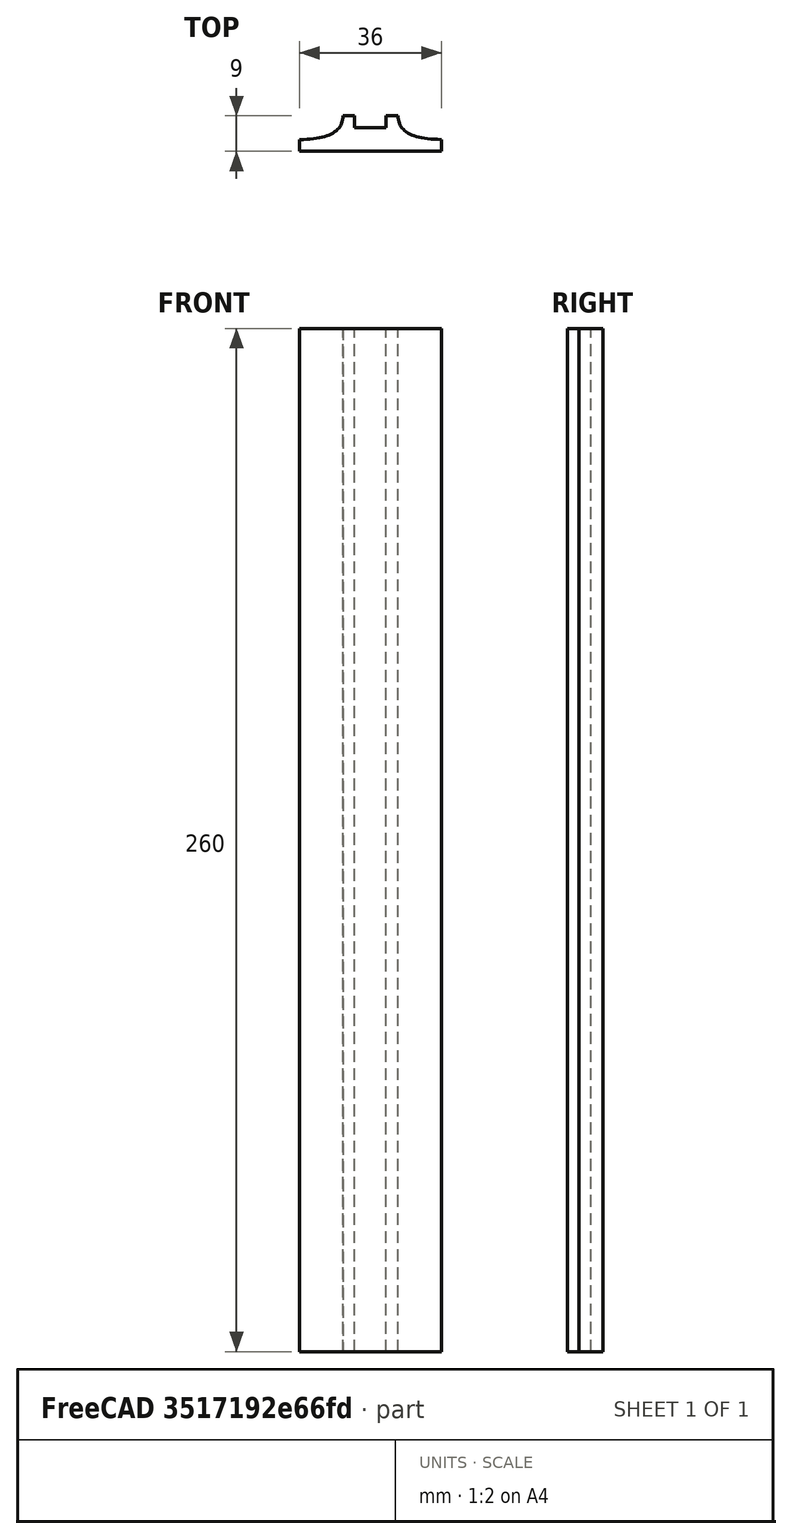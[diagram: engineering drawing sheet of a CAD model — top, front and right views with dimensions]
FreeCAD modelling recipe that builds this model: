
FCSTD DOCUMENT  (FreeCAD 0.19R0.19.2)
Label: laptopStand295.FCStd
License: All rights reserved
LicenseURL: http://en.wikipedia.org/wiki/All_rights_reserved
objects: Sketcher::SketchObject×10, Part::Extrusion×1
note: 11 computed .brp shape members not serialized (recipe doc carries the construction recipe); baked Part::Feature solids carry a one-line shape summary decoded from their .brp

FEATURE [Sketcher::SketchObject] Sketch001  label="legTop"
  FullyConstrained = true
  MapMode = 4
  Placement = pos=(0,0,0) rot=(0.57735,0.57735,0.57735;2.0944rad)
  sketch-geometry (41):
    g0: BSplineCurve PolesCount=3 KnotsCount=2 Degree=2 IsPeriodic=0
    g1: ArcOfCircle CenterX=73.1223 CenterY=-32.291 CenterZ=0 NormalX=0 NormalY=0 NormalZ=1 AngleXU=0 Radius=13 StartAngle=5.92268 EndAngle=9.06428
    g2: ArcOfCircle CenterX=66.7816 CenterY=-49.1439 CenterZ=0 NormalX=0 NormalY=0 NormalZ=1 AngleXU=0 Radius=13 StartAngle=2.78068 EndAngle=5.92131
    g3-g6: Circle x4 (B-spline internal-alignment scaffolding for g7; pole/knot coordinates omitted)
    g7: BSplineCurve PolesCount=4 KnotsCount=2 Degree=3 IsPeriodic=0
    g8: GeomPoint X=28.8094 Y=-19.0875 Z=0
    g9: GeomPoint X=47.0443 Y=-50.4712 Z=0
    g10: Circle CenterX=53.5586 CenterY=-23.2695 CenterZ=0 NormalX=0 NormalY=0 NormalZ=1 AngleXU=0 Radius=3.24518
    g11: LineSegment StartX=117.223 StartY=-19.0875 StartZ=0 EndX=117.223 EndY=-16.0875 EndZ=0
    g12: LineSegment StartX=117.223 StartY=-16.0875 StartZ=0 EndX=17.2232 EndY=-16.0875 EndZ=0
    g13: LineSegment StartX=17.2232 StartY=-16.0875 StartZ=0 EndX=17.2232 EndY=-19.0875 EndZ=0
    g14: LineSegment StartX=28.8094 StartY=-19.0875 StartZ=0 EndX=17.2232 EndY=-19.0875 EndZ=0
    g15: LineSegment StartX=85.2866 StartY=-36.8766 StartZ=0 EndX=78.9396 EndY=-53.7463 EndZ=0
    g16: LineSegment StartX=60.9579 StartY=-27.7053 StartZ=0 EndX=54.6191 EndY=-44.5532 EndZ=0
    g17: ArcOfCircle CenterX=17.2475 CenterY=-181.166 CenterZ=0 NormalX=0 NormalY=0 NormalZ=1 AngleXU=0 Radius=13 StartAngle=5.92268 EndAngle=7.49361
    g18: ArcOfCircle CenterX=29.5716 CenterY=-148.408 CenterZ=0 NormalX=0 NormalY=0 NormalZ=1 AngleXU=0 Radius=13 StartAngle=4.35228 EndAngle=5.92131
    g19: ArcOfCircle CenterX=35.8967 CenterY=-131.555 CenterZ=0 NormalX=0 NormalY=0 NormalZ=1 AngleXU=0 Radius=13 StartAngle=5.92268 EndAngle=7.49902
    g20: ArcOfCircle CenterX=48.1805 CenterY=-98.7782 CenterZ=0 NormalX=0 NormalY=0 NormalZ=1 AngleXU=0 Radius=13 StartAngle=4.34921 EndAngle=5.92131
    g21: ArcOfCircle CenterX=54.5183 CenterY=-81.9247 CenterZ=0 NormalX=0 NormalY=0 NormalZ=1 AngleXU=0 Radius=13 StartAngle=5.92268 EndAngle=8.70432
    g22: LineSegment StartX=66.6827 StartY=-86.5104 StartZ=0 EndX=60.3386 EndY=-103.381 EndZ=0
    g23: LineSegment StartX=48.061 StartY=-136.14 StartZ=0 EndX=41.7296 EndY=-153.01 EndZ=0
    g24: ArcOfCircle CenterX=20.184 CenterY=-217.506 CenterZ=0 NormalX=0 NormalY=0 NormalZ=1 AngleXU=0 Radius=3.81084 StartAngle=1.88136 EndAngle=6.80465
    g25: LineSegment StartX=38.4753 StartY=-115.966 StartZ=0 EndX=41.2852 EndY=-117.017 EndZ=0
    g26: ArcOfCircle CenterX=36.3663 CenterY=-113.042 CenterZ=0 NormalX=0 NormalY=0 NormalZ=1 AngleXU=0 Radius=3.60555 StartAngle=0.230024 EndAngle=5.3372
    g27: LineSegment StartX=39.8769 StartY=-112.22 StartZ=0 EndX=42.6867 EndY=-113.271 EndZ=0
    g28: LineSegment StartX=42.6867 StartY=-113.271 StartZ=0 EndX=43.5628 EndY=-110.929 EndZ=0
    g29: LineSegment StartX=19.9036 StartY=-165.61 StartZ=0 EndX=22.7134 EndY=-166.661 EndZ=0
    g30: ArcOfCircle CenterX=17.7945 CenterY=-162.686 CenterZ=0 NormalX=0 NormalY=0 NormalZ=1 AngleXU=0 Radius=3.60555 StartAngle=0.230024 EndAngle=5.3372
    g31: LineSegment StartX=21.3051 StartY=-161.864 StartZ=0 EndX=24.1149 EndY=-162.915 EndZ=0
    g32: LineSegment StartX=24.1149 StartY=-162.915 StartZ=0 EndX=24.991 EndY=-160.573 EndZ=0
    g33: LineSegment StartX=41.085 StartY=-66.3176 StartZ=0 EndX=46.0385 EndY=-62.5254 EndZ=0
    g34: LineSegment StartX=48.9563 StartY=-66.3367 StartZ=0 EndX=44.7488 EndY=-73.3482 EndZ=0
    g35: ArcOfCircle CenterX=49.8795 CenterY=-62.6074 CenterZ=0 NormalX=0 NormalY=0 NormalZ=1 AngleXU=0 Radius=3.84187 StartAngle=4.46973 EndAngle=9.40343
    g36: LineSegment StartX=41.085 StartY=-66.3176 StartZ=0 EndX=47.0443 EndY=-50.4712 EndZ=0
    g37: LineSegment StartX=29.4118 StartY=-185.752 StartZ=0 EndX=19.0195 EndY=-213.878 EndZ=0
    g38: LineSegment StartX=41.2852 StartY=-117.017 StartZ=0 EndX=40.4148 EndY=-119.365 EndZ=0
    g39: LineSegment StartX=21.8316 StartY=-169.001 StartZ=0 EndX=22.7134 EndY=-166.661 EndZ=0
    g40: LineSegment StartX=23.4884 StartY=-215.608 StartZ=0 EndX=94.6579 EndY=-26.1359 EndZ=0
  constraints (70):
    c: Block(g0)
    c: Block(g1)
    c: Block(g2)
    c: Weight(g3) = 1
    c: Equal(g3,g4)
    c: Equal(g3,g5)
    c: Equal(g3,g6)
    c: InternalAlignment(g3-g6 -> g7) x4
    c: InternalAlignment(g8,g7)
    c: InternalAlignment(g9,g7)
    c: Block(g10)
    c: Block(g7)
    c: Coincident(g11,g0)
    c: Vertical(g11)
    c: Coincident(g12,g11)
    c: Horizontal(g12)
    c: Coincident(g13,g12)
    c: Vertical(g13)
    c: Block(g12)
    c: Coincident(g14,g7)
    c: Coincident(g14,g13)
    c: Horizontal(g14)
    c: Coincident(g15,g1)
    c: Coincident(g15,g2)
    c: Coincident(g16,g1)
    c: Coincident(g16,g2)
    c: Distance(g12) = 100
    c: Block(g17)
    c: Block(g18)
    c: Block(g19)
    c: Block(g20)
    c: Block(g21)
    c: Coincident(g22,g21)
    c: Coincident(g22,g20)
    c: Coincident(g23,g19)
    c: Coincident(g23,g18)
    c: Block(g24)
    c: Block(g26)
    c: Coincident(g27,g26)
    c: Coincident(g25,g26)
    c: Parallel(g27,g25)
    c: Coincident(g28,g27)
    c: Block(g28)
    c: Block(g25)
    c: Block(g27)
    c: Block(g30)
    c: Coincident(g31,g30)
    c: Coincident(g29,g30)
    c: Parallel(g31,g29)
    c: Coincident(g32,g31)
    c: Block(g32)
    c: Block(g29)
    c: Block(g31)
    c: Block(g33)
    c: Coincident(g35,g33)
    c: Coincident(g35,g34)
    c: Block(g35)
    c: Coincident(g36,g33)
    c: Coincident(g36,g7)
    c: Coincident(g37,g17)
    c: Coincident(g37,g24)
    c: PointOnObject(g20,g28)
    c: PointOnObject(g18,g32)
    c: Coincident(g38,g25)
    c: Coincident(g38,g19)
    c: Coincident(g39,g29)
    c: Coincident(g17,g39)
    c: Coincident(g40,g24)
    c: Coincident(g40,g0)
    c: Coincident(g21,g34)
FEATURE [Sketcher::SketchObject] Sketch002
  FullyConstrained = true
  sketch-geometry (20):
    g0: LineSegment StartX=-2.77179 StartY=-200.304 StartZ=0 EndX=5.22821 EndY=-200.304 EndZ=0
    g1: LineSegment StartX=5.22821 StartY=-200.304 StartZ=0 EndX=5.22821 EndY=-197.304 EndZ=0
    g2: LineSegment StartX=-2.77179 StartY=-200.304 StartZ=0 EndX=-2.77179 EndY=-197.304 EndZ=0
    g3: LineSegment StartX=5.22821 StartY=-197.304 StartZ=0 EndX=8.22821 EndY=-197.304 EndZ=0
    g4: LineSegment StartX=-2.77179 StartY=-197.304 StartZ=0 EndX=-5.77179 EndY=-197.304 EndZ=0
    g5: LineSegment StartX=19.2282 StartY=-203.304 StartZ=0 EndX=19.2282 EndY=-206.304 EndZ=0
    g6: LineSegment StartX=-16.7718 StartY=-203.304 StartZ=0 EndX=-16.7718 EndY=-206.304 EndZ=0
    g7: LineSegment StartX=-16.7718 StartY=-206.304 StartZ=0 EndX=19.2282 EndY=-206.304 EndZ=0
    g8: Circle CenterX=-16.7718 CenterY=-203.304 CenterZ=0 NormalX=0 NormalY=0 NormalZ=1 AngleXU=0 Radius=1
    g9: Circle CenterX=-5.77179 CenterY=-203.304 CenterZ=0 NormalX=0 NormalY=0 NormalZ=1 AngleXU=0 Radius=1
    g10: Circle CenterX=-5.77179 CenterY=-197.304 CenterZ=0 NormalX=0 NormalY=0 NormalZ=1 AngleXU=0 Radius=1
    g11: BSplineCurve PolesCount=3 KnotsCount=2 Degree=2 IsPeriodic=0
    g12: GeomPoint X=-16.7718 Y=-203.304 Z=0
    g13: GeomPoint X=-5.77179 Y=-197.304 Z=0
    g14: Circle CenterX=19.2282 CenterY=-203.304 CenterZ=0 NormalX=0 NormalY=0 NormalZ=1 AngleXU=0 Radius=1
    g15: Circle CenterX=8.22821 CenterY=-203.304 CenterZ=0 NormalX=0 NormalY=0 NormalZ=1 AngleXU=0 Radius=1
    g16: Circle CenterX=8.22821 CenterY=-197.304 CenterZ=0 NormalX=0 NormalY=0 NormalZ=1 AngleXU=0 Radius=1
    g17: BSplineCurve PolesCount=3 KnotsCount=2 Degree=2 IsPeriodic=0
    g18: GeomPoint X=19.2282 Y=-203.304 Z=0
    g19: GeomPoint X=8.22821 Y=-197.304 Z=0
  constraints (41):
    c: Horizontal(g0)
    c: Distance(g0) = 8
    c: Coincident(g1,g0)
    c: Vertical(g1)
    c: Distance(g1) = 3
    c: Coincident(g2,g0)
    c: Vertical(g2)
    c: Distance(g2) = 3
    c: Coincident(g3,g1)
    c: Horizontal(g3)
    c: Distance(g3) = 3
    c: Coincident(g4,g2)
    c: Horizontal(g4)
    c: Distance(g4) = 3
    c: Vertical(g5)
    c: Vertical(g6)
    c: Coincident(g7,g6)
    c: Coincident(g7,g5)
    c: Weight(g8) = 1
    c: Equal(g8,g9)
    c: Equal(g8,g10)
    c: Coincident(g11,g4)
    c: InternalAlignment(g8,g11)
    c: InternalAlignment(g9,g11)
    c: InternalAlignment(g10,g11)
    c: InternalAlignment(g12,g11)
    c: InternalAlignment(g13,g11)
    c: Coincident(g17,g5)
    c: Weight(g14) = 1
    c: Equal(g14,g15)
    c: Equal(g14,g16)
    c: Coincident(g17,g3)
    c: InternalAlignment(g14,g17)
    c: InternalAlignment(g15,g17)
    c: InternalAlignment(g16,g17)
    c: InternalAlignment(g18,g17)
    c: InternalAlignment(g19,g17)
    c: Block(g7)
    c: Block(g17)
    c: Block(g11)
    c: Block(g6)
FEATURE [Part::Extrusion] Extrude003
  Base = -> Sketch002
  Dir = (0,0,1)
  DirMode = 2
  FaceMakerClass = Part::FaceMakerBullseye
  LengthFwd = 260
  LengthRev = 0
  Solid = true
  Symmetric = false
FEATURE [Sketcher::SketchObject] Sketch003  label="original"
  FullyConstrained = false
  sketch-geometry (469):
    g0: LineSegment StartX=-42.9272 StartY=136.221 StartZ=0 EndX=-42.9272 EndY=-103.779 EndZ=0
    g1: LineSegment StartX=407.073 StartY=136.221 StartZ=0 EndX=407.073 EndY=-103.779 EndZ=0
    g2: ArcOfCircle CenterX=-26.9272 CenterY=-83.7794 CenterZ=0 NormalX=0 NormalY=0 NormalZ=1 AngleXU=0 Radius=8 StartAngle=3.14159 EndAngle=6.28319
    g3: ArcOfCircle CenterX=391.073 CenterY=-83.7794 CenterZ=0 NormalX=0 NormalY=0 NormalZ=1 AngleXU=0 Radius=8 StartAngle=3.14159 EndAngle=6.28319
    g4: Circle CenterX=175.022 CenterY=27.0628 CenterZ=0 NormalX=0 NormalY=0 NormalZ=1 AngleXU=0 Radius=1
    g5: Circle CenterX=179.022 CenterY=24.8665 CenterZ=0 NormalX=0 NormalY=0 NormalZ=1 AngleXU=0 Radius=1
    g6: Circle CenterX=179.022 CenterY=27.0628 CenterZ=0 NormalX=0 NormalY=0 NormalZ=1 AngleXU=0 Radius=1
    g7: BSplineCurve PolesCount=3 KnotsCount=2 Degree=2 IsPeriodic=0
    g8: GeomPoint X=175.022 Y=27.0628 Z=0
    g9: GeomPoint X=179.022 Y=27.0628 Z=0
    g10: Circle CenterX=189.124 CenterY=27.0628 CenterZ=0 NormalX=0 NormalY=0 NormalZ=1 AngleXU=0 Radius=1
    g11: Circle CenterX=185.124 CenterY=24.8665 CenterZ=0 NormalX=0 NormalY=0 NormalZ=1 AngleXU=0 Radius=1
    g12: Circle CenterX=185.124 CenterY=27.0628 CenterZ=0 NormalX=0 NormalY=0 NormalZ=1 AngleXU=0 Radius=1
    g13: BSplineCurve PolesCount=3 KnotsCount=2 Degree=2 IsPeriodic=0
    g14: GeomPoint X=189.124 Y=27.0628 Z=0
    g15: GeomPoint X=185.124 Y=27.0628 Z=0
    g16: Circle CenterX=175.022 CenterY=5.37834 CenterZ=0 NormalX=0 NormalY=0 NormalZ=1 AngleXU=0 Radius=1
    g17: Circle CenterX=179.022 CenterY=7.57463 CenterZ=0 NormalX=0 NormalY=0 NormalZ=1 AngleXU=0 Radius=1
    g18: Circle CenterX=179.022 CenterY=5.34704 CenterZ=0 NormalX=0 NormalY=0 NormalZ=1 AngleXU=0 Radius=1
    g19: BSplineCurve PolesCount=3 KnotsCount=2 Degree=2 IsPeriodic=0
    g20: GeomPoint X=175.022 Y=5.37834 Z=0
    g21: GeomPoint X=179.022 Y=5.34704 Z=0
    g22: Circle CenterX=189.124 CenterY=5.37834 CenterZ=0 NormalX=0 NormalY=0 NormalZ=1 AngleXU=0 Radius=1
    g23: Circle CenterX=185.124 CenterY=7.57463 CenterZ=0 NormalX=0 NormalY=0 NormalZ=1 AngleXU=0 Radius=1
    g24: Circle CenterX=185.124 CenterY=5.34704 CenterZ=0 NormalX=0 NormalY=0 NormalZ=1 AngleXU=0 Radius=1
    g25: BSplineCurve PolesCount=3 KnotsCount=2 Degree=2 IsPeriodic=0
    g26: GeomPoint X=189.124 Y=5.37834 Z=0
    g27: GeomPoint X=185.124 Y=5.34704 Z=0
    g28: Circle CenterX=165.871 CenterY=18.1458 CenterZ=0 NormalX=0 NormalY=0 NormalZ=1 AngleXU=0 Radius=1
    g29: Circle CenterX=169.377 CenterY=16.2206 CenterZ=0 NormalX=0 NormalY=0 NormalZ=1 AngleXU=0 Radius=1
    g30: Circle CenterX=165.871 CenterY=14.2956 CenterZ=0 NormalX=0 NormalY=0 NormalZ=1 AngleXU=0 Radius=1
    g31: BSplineCurve PolesCount=3 KnotsCount=2 Degree=2 IsPeriodic=0
    g32: GeomPoint X=165.871 Y=18.1458 Z=0
    g33: GeomPoint X=165.871 Y=14.2956 Z=0
    g34: Circle CenterX=198.275 CenterY=18.1318 CenterZ=0 NormalX=0 NormalY=0 NormalZ=1 AngleXU=0 Radius=1
    g35: Circle CenterX=194.768 CenterY=16.2206 CenterZ=0 NormalX=0 NormalY=0 NormalZ=1 AngleXU=0 Radius=1
    g36: Circle CenterX=198.264 CenterY=14.2963 CenterZ=0 NormalX=0 NormalY=0 NormalZ=1 AngleXU=0 Radius=1
    g37: BSplineCurve PolesCount=3 KnotsCount=2 Degree=2 IsPeriodic=0
    g38: GeomPoint X=198.275 Y=18.1318 Z=0
    g39: GeomPoint X=198.264 Y=14.2963 Z=0
    g40: LineSegment StartX=407.073 StartY=-103.779 StartZ=0 EndX=-42.9272 EndY=-103.779 EndZ=0
    g41: Circle CenterX=125.607 CenterY=54.1951 CenterZ=0 NormalX=0 NormalY=0 NormalZ=1 AngleXU=0 Radius=1
    g42: Circle CenterX=139.632 CenterY=46.4944 CenterZ=0 NormalX=0 NormalY=0 NormalZ=1 AngleXU=0 Radius=1
    g43: Circle CenterX=127.326 CenterY=56.7187 CenterZ=0 NormalX=0 NormalY=0 NormalZ=1 AngleXU=0 Radius=1
    g44: BSplineCurve PolesCount=3 KnotsCount=2 Degree=2 IsPeriodic=0
    g45: GeomPoint X=125.607 Y=54.1951 Z=0
    g46: GeomPoint X=127.326 Y=56.7187 Z=0
    g47: Circle CenterX=236.824 CenterY=56.7187 CenterZ=0 NormalX=0 NormalY=0 NormalZ=1 AngleXU=0 Radius=1
    g48: Circle CenterX=224.513 CenterY=46.4944 CenterZ=0 NormalX=0 NormalY=0 NormalZ=1 AngleXU=0 Radius=1
    g49: Circle CenterX=238.538 CenterY=54.1951 CenterZ=0 NormalX=0 NormalY=0 NormalZ=1 AngleXU=0 Radius=1
    g50: BSplineCurve PolesCount=3 KnotsCount=2 Degree=2 IsPeriodic=0
    g51: GeomPoint X=236.824 Y=56.7187 Z=0
    g52: GeomPoint X=238.538 Y=54.1951 Z=0
    g53: Circle CenterX=238.538 CenterY=-21.7516 CenterZ=0 NormalX=0 NormalY=0 NormalZ=1 AngleXU=0 Radius=1
    g54: Circle CenterX=224.513 CenterY=-14.0532 CenterZ=0 NormalX=0 NormalY=0 NormalZ=1 AngleXU=0 Radius=1
    g55: Circle CenterX=236.584 CenterY=-24.2775 CenterZ=0 NormalX=0 NormalY=0 NormalZ=1 AngleXU=0 Radius=1
    g56: BSplineCurve PolesCount=3 KnotsCount=2 Degree=2 IsPeriodic=0
    g57: GeomPoint X=238.538 Y=-21.7516 Z=0
    g58: GeomPoint X=236.584 Y=-24.2775 Z=0
    g59: Circle CenterX=125.607 CenterY=-21.7539 CenterZ=0 NormalX=0 NormalY=0 NormalZ=1 AngleXU=0 Radius=1
    g60: Circle CenterX=139.632 CenterY=-14.0532 CenterZ=0 NormalX=0 NormalY=0 NormalZ=1 AngleXU=0 Radius=1
    g61: Circle CenterX=127.325 CenterY=-24.2775 CenterZ=0 NormalX=0 NormalY=0 NormalZ=1 AngleXU=0 Radius=1
    g62: BSplineCurve PolesCount=3 KnotsCount=2 Degree=2 IsPeriodic=0
    g63: GeomPoint X=125.607 Y=-21.7539 Z=0
    g64: GeomPoint X=127.325 Y=-24.2775 Z=0
    g65: Circle CenterX=302.996 CenterY=111.695 CenterZ=0 NormalX=0 NormalY=0 NormalZ=1 AngleXU=0 Radius=1
    g66: Circle CenterX=306.073 CenterY=114.251 CenterZ=0 NormalX=0 NormalY=0 NormalZ=1 AngleXU=0 Radius=1
    g67: Circle CenterX=306.073 CenterY=110.251 CenterZ=0 NormalX=0 NormalY=0 NormalZ=1 AngleXU=0 Radius=1
    g68: BSplineCurve PolesCount=3 KnotsCount=2 Degree=2 IsPeriodic=0
    g69: GeomPoint X=302.996 Y=111.695 Z=0
    g70: GeomPoint X=306.073 Y=110.251 Z=0
    g71: Circle CenterX=306.073 CenterY=95.2763 CenterZ=0 NormalX=0 NormalY=0 NormalZ=1 AngleXU=0 Radius=1
    g72: Circle CenterX=306.073 CenterY=91.2763 CenterZ=0 NormalX=0 NormalY=0 NormalZ=1 AngleXU=0 Radius=1
    g73: Circle CenterX=302.567 CenterY=89.3511 CenterZ=0 NormalX=0 NormalY=0 NormalZ=1 AngleXU=0 Radius=1
    g74: BSplineCurve PolesCount=3 KnotsCount=2 Degree=2 IsPeriodic=0
    g75: GeomPoint X=306.073 Y=95.2763 Z=0
    g76: GeomPoint X=302.567 Y=89.3511 Z=0
    g77: LineSegment StartX=306.073 StartY=110.251 StartZ=0 EndX=306.073 EndY=95.2763 EndZ=0
    g78: LineSegment StartX=302.996 StartY=111.695 StartZ=0 EndX=236.824 EndY=56.7187 EndZ=0
    g79: LineSegment StartX=238.538 StartY=54.1951 StartZ=0 EndX=302.567 EndY=89.3511 EndZ=0
    g80: Circle CenterX=61.1496 CenterY=111.695 CenterZ=0 NormalX=0 NormalY=0 NormalZ=1 AngleXU=0 Radius=1
    g81: Circle CenterX=58.0728 CenterY=114.251 CenterZ=0 NormalX=0 NormalY=0 NormalZ=1 AngleXU=0 Radius=1
    g82: Circle CenterX=58.0728 CenterY=110.251 CenterZ=0 NormalX=0 NormalY=0 NormalZ=1 AngleXU=0 Radius=1
    g83: BSplineCurve PolesCount=3 KnotsCount=2 Degree=2 IsPeriodic=0
    g84: GeomPoint X=61.1496 Y=111.695 Z=0
    g85: GeomPoint X=58.0728 Y=110.251 Z=0
    g86: Circle CenterX=61.5791 CenterY=89.3511 CenterZ=0 NormalX=0 NormalY=0 NormalZ=1 AngleXU=0 Radius=1
    g87: Circle CenterX=58.0728 CenterY=91.2763 CenterZ=0 NormalX=0 NormalY=0 NormalZ=1 AngleXU=0 Radius=1
    g88: Circle CenterX=58.0728 CenterY=95.2763 CenterZ=0 NormalX=0 NormalY=0 NormalZ=1 AngleXU=0 Radius=1
    g89: BSplineCurve PolesCount=3 KnotsCount=2 Degree=2 IsPeriodic=0
    g90: GeomPoint X=61.5791 Y=89.3511 Z=0
    g91: GeomPoint X=58.0728 Y=95.2763 Z=0
    g92: LineSegment StartX=58.0728 StartY=110.251 StartZ=0 EndX=58.0728 EndY=95.2763 EndZ=0
    g93: LineSegment StartX=61.1496 StartY=111.695 StartZ=0 EndX=127.326 EndY=56.7187 EndZ=0
    g94: LineSegment StartX=125.607 StartY=54.1951 StartZ=0 EndX=61.5791 EndY=89.3511 EndZ=0
    g95: Circle CenterX=61.5791 CenterY=-56.9099 CenterZ=0 NormalX=0 NormalY=0 NormalZ=1 AngleXU=0 Radius=1
    g96: Circle CenterX=58.0728 CenterY=-58.8351 CenterZ=0 NormalX=0 NormalY=0 NormalZ=1 AngleXU=0 Radius=1
    g97: Circle CenterX=58.0728 CenterY=-62.8351 CenterZ=0 NormalX=0 NormalY=0 NormalZ=1 AngleXU=0 Radius=1
    g98: BSplineCurve PolesCount=3 KnotsCount=2 Degree=2 IsPeriodic=0
    g99: GeomPoint X=61.5791 Y=-56.9099 Z=0
    g100: GeomPoint X=58.0728 Y=-62.8351 Z=0
    g101: Circle CenterX=58.0728 CenterY=-77.8102 CenterZ=0 NormalX=0 NormalY=0 NormalZ=1 AngleXU=0 Radius=1
    g102: Circle CenterX=58.0728 CenterY=-81.8102 CenterZ=0 NormalX=0 NormalY=0 NormalZ=1 AngleXU=0 Radius=1
    g103: Circle CenterX=61.1496 CenterY=-79.2541 CenterZ=0 NormalX=0 NormalY=0 NormalZ=1 AngleXU=0 Radius=1
    g104: BSplineCurve PolesCount=3 KnotsCount=2 Degree=2 IsPeriodic=0
    g105: GeomPoint X=58.0728 Y=-77.8102 Z=0
    g106: GeomPoint X=61.1496 Y=-79.2541 Z=0
    g107: LineSegment StartX=58.0728 StartY=-62.8351 StartZ=0 EndX=58.0728 EndY=-77.8102 EndZ=0
    g108: LineSegment StartX=61.1496 StartY=-79.2541 StartZ=0 EndX=127.325 EndY=-24.2775 EndZ=0
    g109: LineSegment StartX=125.607 StartY=-21.7539 StartZ=0 EndX=61.5791 EndY=-56.9099 EndZ=0
    g110: Circle CenterX=302.567 CenterY=-56.9099 CenterZ=0 NormalX=0 NormalY=0 NormalZ=1 AngleXU=0 Radius=1
    g111: Circle CenterX=306.073 CenterY=-58.8351 CenterZ=0 NormalX=0 NormalY=0 NormalZ=1 AngleXU=0 Radius=1
    g112: Circle CenterX=306.073 CenterY=-62.8351 CenterZ=0 NormalX=0 NormalY=0 NormalZ=1 AngleXU=0 Radius=1
    g113: BSplineCurve PolesCount=3 KnotsCount=2 Degree=2 IsPeriodic=0
    g114: GeomPoint X=302.567 Y=-56.9099 Z=0
    g115: GeomPoint X=306.073 Y=-62.8351 Z=0
    g116: Circle CenterX=302.996 CenterY=-79.2541 CenterZ=0 NormalX=0 NormalY=0 NormalZ=1 AngleXU=0 Radius=1
    g117: Circle CenterX=306.073 CenterY=-81.8102 CenterZ=0 NormalX=0 NormalY=0 NormalZ=1 AngleXU=0 Radius=1
    g118: Circle CenterX=306.073 CenterY=-77.8102 CenterZ=0 NormalX=0 NormalY=0 NormalZ=1 AngleXU=0 Radius=1
    g119: BSplineCurve PolesCount=3 KnotsCount=2 Degree=2 IsPeriodic=0
    g120: GeomPoint X=302.996 Y=-79.2541 Z=0
    g121: GeomPoint X=306.073 Y=-77.8102 Z=0
    g122: LineSegment StartX=306.073 StartY=-62.8351 StartZ=0 EndX=306.073 EndY=-77.8102 EndZ=0
    g123: LineSegment StartX=302.996 StartY=-79.2541 StartZ=0 EndX=236.584 EndY=-24.2775 EndZ=0
    g124: LineSegment StartX=238.538 StartY=-21.7516 StartZ=0 EndX=302.567 EndY=-56.9099 EndZ=0
    g125: Circle CenterX=61.6457 CenterY=-88.8112 CenterZ=0 NormalX=0 NormalY=0 NormalZ=1 AngleXU=0 Radius=1
    g126: Circle CenterX=58.0728 CenterY=-91.7794 CenterZ=0 NormalX=0 NormalY=0 NormalZ=1 AngleXU=0 Radius=1
    g127: Circle CenterX=63.9135 CenterY=-91.7791 CenterZ=0 NormalX=0 NormalY=0 NormalZ=1 AngleXU=0 Radius=1
    g128: BSplineCurve PolesCount=3 KnotsCount=2 Degree=2 IsPeriodic=0
    g129: GeomPoint X=61.6457 Y=-88.8112 Z=0
    g130: GeomPoint X=63.9135 Y=-91.7791 Z=0
    g131: Circle CenterX=179.022 CenterY=-85.8163 CenterZ=0 NormalX=0 NormalY=0 NormalZ=1 AngleXU=0 Radius=1
    g132: Circle CenterX=179.022 CenterY=-91.7794 CenterZ=0 NormalX=0 NormalY=0 NormalZ=1 AngleXU=0 Radius=1
    g133: Circle CenterX=171.895 CenterY=-91.7791 CenterZ=0 NormalX=0 NormalY=0 NormalZ=1 AngleXU=0 Radius=1
    g134: BSplineCurve PolesCount=3 KnotsCount=2 Degree=2 IsPeriodic=0
    g135: GeomPoint X=179.022 Y=-85.8163 Z=0
    g136: GeomPoint X=171.895 Y=-91.7791 Z=0
    g137: Circle CenterX=185.124 CenterY=-86.2028 CenterZ=0 NormalX=0 NormalY=0 NormalZ=1 AngleXU=0 Radius=1
    g138: Circle CenterX=185.124 CenterY=-91.7794 CenterZ=0 NormalX=0 NormalY=0 NormalZ=1 AngleXU=0 Radius=1
    g139: Circle CenterX=191.747 CenterY=-91.7794 CenterZ=0 NormalX=0 NormalY=0 NormalZ=1 AngleXU=0 Radius=1
    g140: BSplineCurve PolesCount=3 KnotsCount=2 Degree=2 IsPeriodic=0
    g141: GeomPoint X=185.124 Y=-86.2028 Z=0
    g142: GeomPoint X=191.747 Y=-91.7794 Z=0
    g143: Circle CenterX=299.888 CenterY=-86.6413 CenterZ=0 NormalX=0 NormalY=0 NormalZ=1 AngleXU=0 Radius=1
    g144: Circle CenterX=306.073 CenterY=-91.7794 CenterZ=0 NormalX=0 NormalY=0 NormalZ=1 AngleXU=0 Radius=1
    g145: Circle CenterX=298.776 CenterY=-91.7794 CenterZ=0 NormalX=0 NormalY=0 NormalZ=1 AngleXU=0 Radius=1
    g146: BSplineCurve PolesCount=3 KnotsCount=2 Degree=2 IsPeriodic=0
    g147: GeomPoint X=299.888 Y=-86.6413 Z=0
    g148: GeomPoint X=298.776 Y=-91.7794 Z=0
    g149: LineSegment StartX=189.124 StartY=5.37834 StartZ=0 EndX=299.888 EndY=-86.6413 EndZ=0
    g150: LineSegment StartX=298.776 StartY=-91.7794 StartZ=0 EndX=191.747 EndY=-91.7794 EndZ=0
    g151: LineSegment StartX=185.124 StartY=-86.2028 StartZ=0 EndX=185.124 EndY=5.34704 EndZ=0
    g152: LineSegment StartX=179.022 StartY=5.34704 StartZ=0 EndX=179.022 EndY=-85.8163 EndZ=0
    g153: LineSegment StartX=171.895 StartY=-91.7791 StartZ=0 EndX=63.9135 EndY=-91.7791 EndZ=0
    g154: LineSegment StartX=61.6457 StartY=-88.8112 StartZ=0 EndX=175.022 EndY=5.37834 EndZ=0
    g155: Circle CenterX=302.073 CenterY=124.221 CenterZ=0 NormalX=0 NormalY=0 NormalZ=1 AngleXU=0 Radius=1
    g156: Circle CenterX=306.073 CenterY=124.221 CenterZ=0 NormalX=0 NormalY=0 NormalZ=1 AngleXU=0 Radius=1
    g157: Circle CenterX=302.996 CenterY=121.665 CenterZ=0 NormalX=0 NormalY=0 NormalZ=1 AngleXU=0 Radius=1
    g158: BSplineCurve PolesCount=3 KnotsCount=2 Degree=2 IsPeriodic=0
    g159: GeomPoint X=302.073 Y=124.221 Z=0
    g160: GeomPoint X=302.996 Y=121.665 Z=0
    g161: Circle CenterX=189.124 CenterY=124.221 CenterZ=0 NormalX=0 NormalY=0 NormalZ=1 AngleXU=0 Radius=1
    g162: Circle CenterX=185.124 CenterY=124.221 CenterZ=0 NormalX=0 NormalY=0 NormalZ=1 AngleXU=0 Radius=1
    g163: Circle CenterX=185.124 CenterY=120.221 CenterZ=0 NormalX=0 NormalY=0 NormalZ=1 AngleXU=0 Radius=1
    g164: BSplineCurve PolesCount=3 KnotsCount=2 Degree=2 IsPeriodic=0
    g165: GeomPoint X=189.124 Y=124.221 Z=0
    g166: GeomPoint X=185.124 Y=120.221 Z=0
    g167: Circle CenterX=175.022 CenterY=124.221 CenterZ=0 NormalX=0 NormalY=0 NormalZ=1 AngleXU=0 Radius=1
    g168: Circle CenterX=179.022 CenterY=124.221 CenterZ=0 NormalX=0 NormalY=0 NormalZ=1 AngleXU=0 Radius=1
    g169: Circle CenterX=179.022 CenterY=120.221 CenterZ=0 NormalX=0 NormalY=0 NormalZ=1 AngleXU=0 Radius=1
    g170: BSplineCurve PolesCount=3 KnotsCount=2 Degree=2 IsPeriodic=0
    g171: GeomPoint X=175.022 Y=124.221 Z=0
    g172: GeomPoint X=179.022 Y=120.221 Z=0
    g173: Circle CenterX=62.0728 CenterY=124.221 CenterZ=0 NormalX=0 NormalY=0 NormalZ=1 AngleXU=0 Radius=1
    g174: Circle CenterX=58.0728 CenterY=124.221 CenterZ=0 NormalX=0 NormalY=0 NormalZ=1 AngleXU=0 Radius=1
    g175: Circle CenterX=61.1496 CenterY=121.665 CenterZ=0 NormalX=0 NormalY=0 NormalZ=1 AngleXU=0 Radius=1
    g176: BSplineCurve PolesCount=3 KnotsCount=2 Degree=2 IsPeriodic=0
    g177: GeomPoint X=62.0728 Y=124.221 Z=0
    g178: GeomPoint X=61.1496 Y=121.665 Z=0
    g179: LineSegment StartX=179.022 StartY=120.221 StartZ=0 EndX=179.022 EndY=27.0628 EndZ=0
    g180: LineSegment StartX=185.124 StartY=27.0628 StartZ=0 EndX=185.124 EndY=120.221 EndZ=0
    g181: LineSegment StartX=302.996 StartY=121.665 StartZ=0 EndX=189.124 EndY=27.0628 EndZ=0
    g182: LineSegment StartX=175.022 StartY=27.0628 StartZ=0 EndX=61.1496 EndY=121.665 EndZ=0
    g183: Circle CenterX=61.5791 CenterY=75.4095 CenterZ=0 NormalX=0 NormalY=0 NormalZ=1 AngleXU=0 Radius=1
    g184: Circle CenterX=58.0728 CenterY=77.3346 CenterZ=0 NormalX=0 NormalY=0 NormalZ=1 AngleXU=0 Radius=1
    g185: Circle CenterX=58.0728 CenterY=73.3346 CenterZ=0 NormalX=0 NormalY=0 NormalZ=1 AngleXU=0 Radius=1
    g186: BSplineCurve PolesCount=3 KnotsCount=2 Degree=2 IsPeriodic=0
    g187: GeomPoint X=61.5791 Y=75.4095 Z=0
    g188: GeomPoint X=58.0728 Y=73.3346 Z=0
    g189: Circle CenterX=58.0728 CenterY=-40.8935 CenterZ=0 NormalX=0 NormalY=0 NormalZ=1 AngleXU=0 Radius=1
    g190: Circle CenterX=58.0728 CenterY=-44.8935 CenterZ=0 NormalX=0 NormalY=0 NormalZ=1 AngleXU=0 Radius=1
    g191: Circle CenterX=61.5791 CenterY=-42.9683 CenterZ=0 NormalX=0 NormalY=0 NormalZ=1 AngleXU=0 Radius=1
    g192: BSplineCurve PolesCount=3 KnotsCount=2 Degree=2 IsPeriodic=0
    g193: GeomPoint X=58.0728 Y=-40.8935 Z=0
    g194: GeomPoint X=61.5791 Y=-42.9683 Z=0
    g195: LineSegment StartX=61.5791 StartY=-42.9683 StartZ=0 EndX=165.871 EndY=14.2956 EndZ=0
    g196: LineSegment StartX=165.871 StartY=18.1458 StartZ=0 EndX=61.5791 EndY=75.4095 EndZ=0
    g197: LineSegment StartX=58.0728 StartY=73.3346 StartZ=0 EndX=58.0728 EndY=-40.8935 EndZ=0
    g198: Circle CenterX=302.567 CenterY=-42.9683 CenterZ=0 NormalX=0 NormalY=0 NormalZ=1 AngleXU=0 Radius=1
    g199: Circle CenterX=306.073 CenterY=-44.8935 CenterZ=0 NormalX=0 NormalY=0 NormalZ=1 AngleXU=0 Radius=1
    g200: Circle CenterX=306.073 CenterY=-40.8935 CenterZ=0 NormalX=0 NormalY=0 NormalZ=1 AngleXU=0 Radius=1
    g201: BSplineCurve PolesCount=3 KnotsCount=2 Degree=2 IsPeriodic=0
    g202: GeomPoint X=302.567 Y=-42.9683 Z=0
    g203: GeomPoint X=306.073 Y=-40.8935 Z=0
    g204: Circle CenterX=306.073 CenterY=73.3346 CenterZ=0 NormalX=0 NormalY=0 NormalZ=1 AngleXU=0 Radius=1
    g205: Circle CenterX=306.073 CenterY=77.3346 CenterZ=0 NormalX=0 NormalY=0 NormalZ=1 AngleXU=0 Radius=1
    g206: Circle CenterX=302.535 CenterY=75.4095 CenterZ=0 NormalX=0 NormalY=0 NormalZ=1 AngleXU=0 Radius=1
    g207: BSplineCurve PolesCount=3 KnotsCount=2 Degree=2 IsPeriodic=0
    g208: GeomPoint X=306.073 Y=73.3346 Z=0
    g209: GeomPoint X=302.535 Y=75.4095 Z=0
    g210: LineSegment StartX=302.567 StartY=-42.9683 StartZ=0 EndX=198.264 EndY=14.2963 EndZ=0
    g211: LineSegment StartX=198.275 StartY=18.1318 StartZ=0 EndX=302.535 EndY=75.4095 EndZ=0
    g212: LineSegment StartX=306.073 StartY=73.3346 StartZ=0 EndX=306.073 EndY=-40.8935 EndZ=0
    g213: LineSegment StartX=322.073 StartY=105.865 StartZ=0 EndX=328.643 EndY=105.865 EndZ=0
    g214: LineSegment StartX=318.073 StartY=120.221 StartZ=0 EndX=318.073 EndY=109.865 EndZ=0
    g215: LineSegment StartX=336.157 StartY=107.779 StartZ=0 EndX=362.567 EndY=122.294 EndZ=0
    g216: Circle CenterX=362.073 CenterY=124.221 CenterZ=0 NormalX=0 NormalY=0 NormalZ=1 AngleXU=0 Radius=1
    g217: Circle CenterX=366.073 CenterY=124.221 CenterZ=0 NormalX=0 NormalY=0 NormalZ=1 AngleXU=0 Radius=1
    g218: Circle CenterX=362.567 CenterY=122.294 CenterZ=0 NormalX=0 NormalY=0 NormalZ=1 AngleXU=0 Radius=1
    g219: BSplineCurve PolesCount=3 KnotsCount=2 Degree=2 IsPeriodic=0
    g220: GeomPoint X=362.073 Y=124.221 Z=0
    g221: GeomPoint X=362.567 Y=122.294 Z=0
    g222: Circle CenterX=322.073 CenterY=124.221 CenterZ=0 NormalX=0 NormalY=0 NormalZ=1 AngleXU=0 Radius=1
    g223: Circle CenterX=318.073 CenterY=124.221 CenterZ=0 NormalX=0 NormalY=0 NormalZ=1 AngleXU=0 Radius=1
    g224: Circle CenterX=318.073 CenterY=120.221 CenterZ=0 NormalX=0 NormalY=0 NormalZ=1 AngleXU=0 Radius=1
    g225: BSplineCurve PolesCount=3 KnotsCount=2 Degree=2 IsPeriodic=0
    g226: GeomPoint X=322.073 Y=124.221 Z=0
    g227: GeomPoint X=318.073 Y=120.221 Z=0
    g228: Circle CenterX=322.073 CenterY=105.865 CenterZ=0 NormalX=0 NormalY=0 NormalZ=1 AngleXU=0 Radius=1
    g229: Circle CenterX=318.073 CenterY=105.865 CenterZ=0 NormalX=0 NormalY=0 NormalZ=1 AngleXU=0 Radius=1
    g230: Circle CenterX=318.073 CenterY=109.865 CenterZ=0 NormalX=0 NormalY=0 NormalZ=1 AngleXU=0 Radius=1
    g231: BSplineCurve PolesCount=3 KnotsCount=2 Degree=2 IsPeriodic=0
    g232: GeomPoint X=322.073 Y=105.865 Z=0
    g233: GeomPoint X=318.073 Y=109.865 Z=0
    g234: Circle CenterX=336.157 CenterY=107.779 CenterZ=0 NormalX=0 NormalY=0 NormalZ=1 AngleXU=0 Radius=1
    g235: Circle CenterX=332.651 CenterY=105.853 CenterZ=0 NormalX=0 NormalY=0 NormalZ=1 AngleXU=0 Radius=1
    g236: Circle CenterX=328.643 CenterY=105.865 CenterZ=0 NormalX=0 NormalY=0 NormalZ=1 AngleXU=0 Radius=1
    g237: BSplineCurve PolesCount=3 KnotsCount=2 Degree=2 IsPeriodic=0
    g238: GeomPoint X=336.157 Y=107.779 Z=0
    g239: GeomPoint X=328.643 Y=105.865 Z=0
    g240: LineSegment StartX=322.073 StartY=124.221 StartZ=0 EndX=362.073 EndY=124.221 EndZ=0
    g241: Circle CenterX=371.567 CenterY=-80.8644 CenterZ=0 NormalX=0 NormalY=0 NormalZ=1 AngleXU=0 Radius=1
    g242: Circle CenterX=375.073 CenterY=-82.7896 CenterZ=0 NormalX=0 NormalY=0 NormalZ=1 AngleXU=0 Radius=1
    g243: Circle CenterX=375.073 CenterY=-78.7896 CenterZ=0 NormalX=0 NormalY=0 NormalZ=1 AngleXU=0 Radius=1
    g244: BSplineCurve PolesCount=3 KnotsCount=2 Degree=2 IsPeriodic=0
    g245: GeomPoint X=371.567 Y=-80.8644 Z=0
    g246: GeomPoint X=375.073 Y=-78.7896 Z=0
    g247: Circle CenterX=321.579 CenterY=-53.4075 CenterZ=0 NormalX=0 NormalY=0 NormalZ=1 AngleXU=0 Radius=1
    g248: Circle CenterX=318.073 CenterY=-51.4823 CenterZ=0 NormalX=0 NormalY=0 NormalZ=1 AngleXU=0 Radius=1
    g249: Circle CenterX=318.073 CenterY=-47.4805 CenterZ=0 NormalX=0 NormalY=0 NormalZ=1 AngleXU=0 Radius=1
    g250: BSplineCurve PolesCount=3 KnotsCount=2 Degree=2 IsPeriodic=0
    g251: GeomPoint X=321.579 Y=-53.4075 Z=0
    g252: GeomPoint X=318.073 Y=-47.4805 Z=0
    g253: LineSegment StartX=371.567 StartY=-80.8644 StartZ=0 EndX=321.579 EndY=-53.4075 EndZ=0
    g254: Circle CenterX=321.579 CenterY=-67.3492 CenterZ=0 NormalX=0 NormalY=0 NormalZ=1 AngleXU=0 Radius=1
    g255: Circle CenterX=318.073 CenterY=-65.424 CenterZ=0 NormalX=0 NormalY=0 NormalZ=1 AngleXU=0 Radius=1
    g256: Circle CenterX=318.073 CenterY=-69.424 CenterZ=0 NormalX=0 NormalY=0 NormalZ=1 AngleXU=0 Radius=1
    g257: BSplineCurve PolesCount=3 KnotsCount=2 Degree=2 IsPeriodic=0
    g258: GeomPoint X=321.579 Y=-67.3492 Z=0
    g259: GeomPoint X=318.073 Y=-69.424 Z=0
    g260: Circle CenterX=362.567 CenterY=-89.8542 CenterZ=0 NormalX=0 NormalY=0 NormalZ=1 AngleXU=0 Radius=1
    g261: Circle CenterX=366.073 CenterY=-91.7794 CenterZ=0 NormalX=0 NormalY=0 NormalZ=1 AngleXU=0 Radius=1
    g262: Circle CenterX=362.073 CenterY=-91.7794 CenterZ=0 NormalX=0 NormalY=0 NormalZ=1 AngleXU=0 Radius=1
    g263: BSplineCurve PolesCount=3 KnotsCount=2 Degree=2 IsPeriodic=0
    g264: GeomPoint X=362.567 Y=-89.8542 Z=0
    g265: GeomPoint X=362.073 Y=-91.7794 Z=0
    g266: Circle CenterX=322.073 CenterY=-91.7794 CenterZ=0 NormalX=0 NormalY=0 NormalZ=1 AngleXU=0 Radius=1
    g267: Circle CenterX=318.073 CenterY=-91.7794 CenterZ=0 NormalX=0 NormalY=0 NormalZ=1 AngleXU=0 Radius=1
    g268: Circle CenterX=318.073 CenterY=-87.7794 CenterZ=0 NormalX=0 NormalY=0 NormalZ=1 AngleXU=0 Radius=1
    g269: BSplineCurve PolesCount=3 KnotsCount=2 Degree=2 IsPeriodic=0
    g270: GeomPoint X=322.073 Y=-91.7794 Z=0
    g271: GeomPoint X=318.073 Y=-87.7794 Z=0
    g272: LineSegment StartX=362.567 StartY=-89.8542 StartZ=0 EndX=321.579 EndY=-67.3492 EndZ=0
    g273: LineSegment StartX=318.073 StartY=-69.424 StartZ=0 EndX=318.073 EndY=-87.7794 EndZ=0
    g274: LineSegment StartX=322.073 StartY=-91.7794 StartZ=0 EndX=362.073 EndY=-91.7794 EndZ=0
    g275: Circle CenterX=2.07281 CenterY=124.221 CenterZ=0 NormalX=0 NormalY=0 NormalZ=1 AngleXU=0 Radius=1
    g276: Circle CenterX=1.57905 CenterY=122.295 CenterZ=0 NormalX=0 NormalY=0 NormalZ=1 AngleXU=0 Radius=1
    g277: BSplineCurve PolesCount=3 KnotsCount=2 Degree=2 IsPeriodic=0
    g278: GeomPoint X=2.07281 Y=124.221 Z=0
    g279: GeomPoint X=1.57905 Y=122.295 Z=0
    g280: Circle CenterX=42.0728 CenterY=124.221 CenterZ=0 NormalX=0 NormalY=0 NormalZ=1 AngleXU=0 Radius=1
    g281: Circle CenterX=46.0728 CenterY=124.221 CenterZ=0 NormalX=0 NormalY=0 NormalZ=1 AngleXU=0 Radius=1
    g282: Circle CenterX=46.0728 CenterY=120.221 CenterZ=0 NormalX=0 NormalY=0 NormalZ=1 AngleXU=0 Radius=1
    g283: BSplineCurve PolesCount=3 KnotsCount=2 Degree=2 IsPeriodic=0
    g284: GeomPoint X=42.0728 Y=124.221 Z=0
    g285: GeomPoint X=46.0728 Y=120.221 Z=0
    g286: Circle CenterX=46.0728 CenterY=109.865 CenterZ=0 NormalX=0 NormalY=0 NormalZ=1 AngleXU=0 Radius=1
    g287: Circle CenterX=46.0728 CenterY=105.865 CenterZ=0 NormalX=0 NormalY=0 NormalZ=1 AngleXU=0 Radius=1
    g288: Circle CenterX=42.0728 CenterY=105.865 CenterZ=0 NormalX=0 NormalY=0 NormalZ=1 AngleXU=0 Radius=1
    g289: BSplineCurve PolesCount=3 KnotsCount=2 Degree=2 IsPeriodic=0
    g290: GeomPoint X=46.0728 Y=109.865 Z=0
    g291: GeomPoint X=42.0728 Y=105.865 Z=0
    g292: Circle CenterX=35.5028 CenterY=105.865 CenterZ=0 NormalX=0 NormalY=0 NormalZ=1 AngleXU=0 Radius=1
    g293: Circle CenterX=31.5028 CenterY=105.865 CenterZ=0 NormalX=0 NormalY=0 NormalZ=1 AngleXU=0 Radius=1
    g294: Circle CenterX=27.9965 CenterY=107.79 CenterZ=0 NormalX=0 NormalY=0 NormalZ=1 AngleXU=0 Radius=1
    g295: BSplineCurve PolesCount=3 KnotsCount=2 Degree=2 IsPeriodic=0
    g296: GeomPoint X=35.5028 Y=105.865 Z=0
    g297: GeomPoint X=27.9965 Y=107.79 Z=0
    g298: LineSegment StartX=2.07281 StartY=124.221 StartZ=0 EndX=42.0728 EndY=124.221 EndZ=0
    g299: LineSegment StartX=46.0728 StartY=120.221 StartZ=0 EndX=46.0728 EndY=109.865 EndZ=0
    g300: LineSegment StartX=42.0728 StartY=105.865 StartZ=0 EndX=35.5028 EndY=105.865 EndZ=0
    g301: LineSegment StartX=27.9965 StartY=107.79 StartZ=0 EndX=1.57905 EndY=122.295 EndZ=0
    g302: Circle CenterX=42.5666 CenterY=-67.3492 CenterZ=0 NormalX=0 NormalY=0 NormalZ=1 AngleXU=0 Radius=1
    g303: Circle CenterX=46.0728 CenterY=-65.424 CenterZ=0 NormalX=0 NormalY=0 NormalZ=1 AngleXU=0 Radius=1
    g304: Circle CenterX=46.0728 CenterY=-69.424 CenterZ=0 NormalX=0 NormalY=0 NormalZ=1 AngleXU=0 Radius=1
    g305: BSplineCurve PolesCount=3 KnotsCount=2 Degree=2 IsPeriodic=0
    g306: GeomPoint X=42.5666 Y=-67.3492 Z=0
    g307: GeomPoint X=46.0728 Y=-69.424 Z=0
    g308: Circle CenterX=46.0728 CenterY=-87.7794 CenterZ=0 NormalX=0 NormalY=0 NormalZ=1 AngleXU=0 Radius=1
    g309: Circle CenterX=46.0728 CenterY=-91.7794 CenterZ=0 NormalX=0 NormalY=0 NormalZ=1 AngleXU=0 Radius=1
    g310: Circle CenterX=42.0728 CenterY=-91.7794 CenterZ=0 NormalX=0 NormalY=0 NormalZ=1 AngleXU=0 Radius=1
    g311: BSplineCurve PolesCount=3 KnotsCount=2 Degree=2 IsPeriodic=0
    g312: GeomPoint X=46.0728 Y=-87.7794 Z=0
    g313: GeomPoint X=42.0728 Y=-91.7794 Z=0
    g314: Circle CenterX=2.07281 CenterY=-91.7794 CenterZ=0 NormalX=0 NormalY=0 NormalZ=1 AngleXU=0 Radius=1
    g315: Circle CenterX=-1.92719 CenterY=-91.7794 CenterZ=0 NormalX=0 NormalY=0 NormalZ=1 AngleXU=0 Radius=1
    g316: Circle CenterX=1.57905 CenterY=-89.8542 CenterZ=0 NormalX=0 NormalY=0 NormalZ=1 AngleXU=0 Radius=1
    g317: BSplineCurve PolesCount=3 KnotsCount=2 Degree=2 IsPeriodic=0
    g318: GeomPoint X=2.07281 Y=-91.7794 Z=0
    g319: GeomPoint X=1.57905 Y=-89.8542 Z=0
    g320: LineSegment StartX=2.07281 StartY=-91.7794 StartZ=0 EndX=42.0728 EndY=-91.7794 EndZ=0
    g321: LineSegment StartX=46.0728 StartY=-87.7794 StartZ=0 EndX=46.0728 EndY=-69.424 EndZ=0
    g322: LineSegment StartX=42.5666 StartY=-67.3492 StartZ=0 EndX=1.57905 EndY=-89.8542 EndZ=0
    g323: Circle CenterX=322.073 CenterY=76.4095 CenterZ=0 NormalX=0 NormalY=0 NormalZ=1 AngleXU=0 Radius=4
    g324: BSplineCurve PolesCount=3 KnotsCount=2 Degree=2 IsPeriodic=0
    g325: GeomPoint X=318.073 Y=72.4095 Z=0
    g326: GeomPoint X=322.073 Y=76.4095 Z=0
    g327: Circle CenterX=375.073 CenterY=72.4095 CenterZ=0 NormalX=0 NormalY=0 NormalZ=1 AngleXU=0 Radius=1
    g328: Circle CenterX=375.073 CenterY=76.4095 CenterZ=0 NormalX=0 NormalY=0 NormalZ=1 AngleXU=0 Radius=1
    g329: Circle CenterX=371.073 CenterY=76.4095 CenterZ=0 NormalX=0 NormalY=0 NormalZ=1 AngleXU=0 Radius=1
    g330: BSplineCurve PolesCount=3 KnotsCount=2 Degree=2 IsPeriodic=0
    g331: GeomPoint X=375.073 Y=72.4095 Z=0
    g332: GeomPoint X=371.073 Y=76.4095 Z=0
    g333: LineSegment StartX=322.073 StartY=76.4095 StartZ=0 EndX=371.073 EndY=76.4095 EndZ=0
    g334: LineSegment StartX=318.073 StartY=72.4095 StartZ=0 EndX=318.073 EndY=-47.4805 EndZ=0
    g335: LineSegment StartX=375.073 StartY=72.4095 StartZ=0 EndX=375.073 EndY=-78.7896 EndZ=0
    g336: ArcOfCircle CenterX=-26.9272 CenterY=22.1087 CenterZ=0 NormalX=0 NormalY=0 NormalZ=1 AngleXU=0 Radius=4 StartAngle=5e-16 EndAngle=3.14159
    g337: LineSegment StartX=-22.9272 StartY=22.1087 StartZ=0 EndX=-18.9272 EndY=-83.7794 EndZ=0
    g338: LineSegment StartX=-34.9272 StartY=-83.7794 StartZ=0 EndX=-30.9272 EndY=22.1087 EndZ=0
    g339: ArcOfCircle CenterX=391.073 CenterY=22.1087 CenterZ=0 NormalX=0 NormalY=0 NormalZ=1 AngleXU=0 Radius=4 StartAngle=0 EndAngle=3.14159
    g340: LineSegment StartX=387.073 StartY=22.1087 StartZ=0 EndX=383.073 EndY=-83.7794 EndZ=0
    g341: LineSegment StartX=395.073 StartY=22.1087 StartZ=0 EndX=399.073 EndY=-83.7794 EndZ=0
    g342: Circle CenterX=-10.9272 CenterY=-78.7794 CenterZ=0 NormalX=0 NormalY=0 NormalZ=1 AngleXU=0 Radius=1
    g343: Circle CenterX=-10.9272 CenterY=-82.7794 CenterZ=0 NormalX=0 NormalY=0 NormalZ=1 AngleXU=0 Radius=1
    g344: Circle CenterX=-7.42095 CenterY=-80.8542 CenterZ=0 NormalX=0 NormalY=0 NormalZ=1 AngleXU=0 Radius=1
    g345: BSplineCurve PolesCount=3 KnotsCount=2 Degree=2 IsPeriodic=0
    g346: GeomPoint X=-10.9272 Y=-78.7794 Z=0
    g347: GeomPoint X=-7.42095 Y=-80.8542 Z=0
    g348: Circle CenterX=42.5666 CenterY=-53.4075 CenterZ=0 NormalX=0 NormalY=0 NormalZ=1 AngleXU=0 Radius=1
    g349: Circle CenterX=46.0728 CenterY=-51.4823 CenterZ=0 NormalX=0 NormalY=0 NormalZ=1 AngleXU=0 Radius=1
    g350: Circle CenterX=46.0728 CenterY=-47.4823 CenterZ=0 NormalX=0 NormalY=0 NormalZ=1 AngleXU=0 Radius=1
    g351: BSplineCurve PolesCount=3 KnotsCount=2 Degree=2 IsPeriodic=0
    g352: GeomPoint X=42.5666 Y=-53.4075 Z=0
    g353: GeomPoint X=46.0728 Y=-47.4823 Z=0
    g354: Circle CenterX=46.0728 CenterY=72.4095 CenterZ=0 NormalX=0 NormalY=0 NormalZ=1 AngleXU=0 Radius=1
    g355: Circle CenterX=46.0728 CenterY=76.4095 CenterZ=0 NormalX=0 NormalY=0 NormalZ=1 AngleXU=0 Radius=1
    g356: Circle CenterX=42.0728 CenterY=76.4095 CenterZ=0 NormalX=0 NormalY=0 NormalZ=1 AngleXU=0 Radius=1
    g357: BSplineCurve PolesCount=3 KnotsCount=2 Degree=2 IsPeriodic=0
    g358: GeomPoint X=46.0728 Y=72.4095 Z=0
    g359: GeomPoint X=42.0728 Y=76.4095 Z=0
    g360: Circle CenterX=-6.92719 CenterY=76.4095 CenterZ=0 NormalX=0 NormalY=0 NormalZ=1 AngleXU=0 Radius=1
    g361: Circle CenterX=-10.9272 CenterY=76.4095 CenterZ=0 NormalX=0 NormalY=0 NormalZ=1 AngleXU=0 Radius=1
    g362: Circle CenterX=-10.9272 CenterY=72.4095 CenterZ=0 NormalX=0 NormalY=0 NormalZ=1 AngleXU=0 Radius=1
    g363: BSplineCurve PolesCount=3 KnotsCount=2 Degree=2 IsPeriodic=0
    g364: GeomPoint X=-6.92719 Y=76.4095 Z=0
    g365: GeomPoint X=-10.9272 Y=72.4095 Z=0
    g366: LineSegment StartX=-10.9272 StartY=72.4095 StartZ=0 EndX=-10.9272 EndY=-78.7794 EndZ=0
    g367: LineSegment StartX=-7.42095 StartY=-80.8542 StartZ=0 EndX=42.5666 EndY=-53.4075 EndZ=0
    g368: LineSegment StartX=46.0728 StartY=-47.4823 StartZ=0 EndX=46.0728 EndY=72.4095 EndZ=0
    g369: LineSegment StartX=42.0728 StartY=76.4095 StartZ=0 EndX=-6.92719 EndY=76.4095 EndZ=0
    g370: LineSegment StartX=-42.9272 StartY=136.221 StartZ=0 EndX=407.073 EndY=136.221 EndZ=0
    g371: LineSegment StartX=232.072 StartY=136.221 StartZ=0 EndX=220.072 EndY=136.221 EndZ=0
    g372: LineSegment StartX=232.072 StartY=136.221 StartZ=0 EndX=232.072 EndY=124.221 EndZ=0
    g373: LineSegment StartX=220.072 StartY=136.221 StartZ=0 EndX=220.072 EndY=124.221 EndZ=0
    g374: LineSegment StartX=220.072 StartY=136.221 StartZ=0 EndX=226.072 EndY=136.221 EndZ=0
    g375: LineSegment StartX=220.072 StartY=136.221 StartZ=0 EndX=220.072 EndY=130.221 EndZ=0
    g376: LineSegment StartX=220.072 StartY=124.221 StartZ=0 EndX=226.072 EndY=124.221 EndZ=0
    g377: LineSegment StartX=232.072 StartY=124.221 StartZ=0 EndX=232.072 EndY=127.221 EndZ=0
    g378: LineSegment StartX=232.072 StartY=136.221 StartZ=0 EndX=232.072 EndY=133.221 EndZ=0
    g379-g383: Circle x5 (B-spline internal-alignment scaffolding for g384; pole/knot coordinates omitted)
    g384: BSplineCurve PolesCount=5 KnotsCount=3 Degree=3 IsPeriodic=0
    g385: GeomPoint X=232.072 Y=133.221 Z=0
    g386: GeomPoint X=223.072 Y=130.221 Z=0
    g387: GeomPoint X=232.072 Y=127.221 Z=0
    g388: LineSegment StartX=189.124 StartY=124.221 StartZ=0 EndX=302.073 EndY=124.221 EndZ=0
    g389: LineSegment StartX=132.072 StartY=136.221 StartZ=0 EndX=132.072 EndY=124.221 EndZ=0
    g390: LineSegment StartX=132.072 StartY=136.221 StartZ=0 EndX=144.072 EndY=136.221 EndZ=0
    g391: LineSegment StartX=144.072 StartY=136.221 StartZ=0 EndX=144.072 EndY=124.221 EndZ=0
    g392: LineSegment StartX=144.072 StartY=136.221 StartZ=0 EndX=138.072 EndY=136.221 EndZ=0
    g393: LineSegment StartX=144.072 StartY=136.221 StartZ=0 EndX=144.072 EndY=130.221 EndZ=0
    g394: LineSegment StartX=132.072 StartY=136.221 StartZ=0 EndX=132.072 EndY=133.221 EndZ=0
    g395: LineSegment StartX=132.072 StartY=133.221 StartZ=0 EndX=132.072 EndY=127.221 EndZ=0
    g396-g400: Circle x5 (B-spline internal-alignment scaffolding for g401; pole/knot coordinates omitted)
    g401: BSplineCurve PolesCount=5 KnotsCount=3 Degree=3 IsPeriodic=0
    g402: GeomPoint X=132.072 Y=133.221 Z=0
    g403: GeomPoint X=141.072 Y=130.221 Z=0
    g404: GeomPoint X=132.072 Y=127.221 Z=0
    g405: LineSegment StartX=132.072 StartY=124.221 StartZ=0 EndX=175.022 EndY=124.221 EndZ=0
    g406: LineSegment StartX=62.0728 StartY=124.221 StartZ=0 EndX=132.072 EndY=124.221 EndZ=0
    g407: LineSegment StartX=132.072 StartY=136.221 StartZ=0 EndX=131.457 EndY=138.832 EndZ=0
    ... +61 more geometry lines
  constraints (808):
    c: Vertical(g0)
    c: Vertical(g1)
    c: Block(g1)
    c: Block(g0)
    c: Weight(g4) = 1
    c: Equal(g4,g5)
    c: Equal(g4,g6)
    c: InternalAlignment(g4,g7)
    c: InternalAlignment(g5,g7)
    c: InternalAlignment(g6,g7)
    c: InternalAlignment(g8,g7)
    c: InternalAlignment(g9,g7)
    c: Weight(g10) = 1
    c: Equal(g10,g11)
    c: Equal(g10,g12)
    c: InternalAlignment(g10,g13)
    c: InternalAlignment(g11,g13)
    c: InternalAlignment(g12,g13)
    c: InternalAlignment(g14,g13)
    c: InternalAlignment(g15,g13)
    c: Block(g13)
    c: Block(g7)
    c: Weight(g16) = 1
    c: Equal(g16,g17)
    c: Equal(g16,g18)
    c: InternalAlignment(g16,g19)
    c: InternalAlignment(g17,g19)
    c: InternalAlignment(g18,g19)
    c: InternalAlignment(g20,g19)
    c: InternalAlignment(g21,g19)
    c: Weight(g22) = 1
    c: Equal(g22,g23)
    c: Equal(g22,g24)
    c: InternalAlignment(g22,g25)
    c: InternalAlignment(g23,g25)
    c: InternalAlignment(g24,g25)
    c: InternalAlignment(g26,g25)
    c: InternalAlignment(g27,g25)
    c: Block(g25)
    c: Block(g19)
    c: Weight(g28) = 1
    c: Equal(g28,g29)
    c: Equal(g28,g30)
    c: InternalAlignment(g28,g31)
    c: InternalAlignment(g29,g31)
    c: InternalAlignment(g30,g31)
    c: InternalAlignment(g32,g31)
    c: InternalAlignment(g33,g31)
    c: Weight(g34) = 1
    c: Equal(g34,g35)
    c: Equal(g34,g36)
    c: InternalAlignment(g34,g37)
    c: InternalAlignment(g35,g37)
    c: InternalAlignment(g36,g37)
    c: InternalAlignment(g38,g37)
    c: InternalAlignment(g39,g37)
    c: Block(g31)
    c: Block(g37)
    c: Coincident(g40,g1)
    c: Coincident(g40,g0)
    c: Horizontal(g40)
    c: Distance(g40) = 450
    c: Weight(g41) = 1
    c: Equal(g41,g42)
    c: Equal(g41,g43)
    c: InternalAlignment(g41,g44)
    c: InternalAlignment(g42,g44)
    c: InternalAlignment(g43,g44)
    c: InternalAlignment(g45,g44)
    c: InternalAlignment(g46,g44)
    c: Block(g44)
    c: Weight(g47) = 1
    c: Equal(g47,g48)
    c: Equal(g47,g49)
    c: InternalAlignment(g47,g50)
    c: InternalAlignment(g48,g50)
    c: InternalAlignment(g49,g50)
    c: InternalAlignment(g51,g50)
    c: InternalAlignment(g52,g50)
    c: Block(g50)
    c: Weight(g53) = 1
    c: Equal(g53,g54)
    c: Equal(g53,g55)
    c: InternalAlignment(g53,g56)
    c: InternalAlignment(g54,g56)
    c: InternalAlignment(g55,g56)
    c: InternalAlignment(g57,g56)
    c: InternalAlignment(g58,g56)
    c: Block(g56)
    c: Weight(g59) = 1
    c: Equal(g59,g60)
    c: Equal(g59,g61)
    c: InternalAlignment(g59,g62)
    c: InternalAlignment(g60,g62)
    c: InternalAlignment(g61,g62)
    c: InternalAlignment(g63,g62)
    c: InternalAlignment(g64,g62)
    c: Block(g62)
    c: Weight(g65) = 1
    c: Equal(g65,g66)
    c: Equal(g65,g67)
    c: InternalAlignment(g65,g68)
    c: InternalAlignment(g66,g68)
    c: InternalAlignment(g67,g68)
    c: InternalAlignment(g69,g68)
    c: InternalAlignment(g70,g68)
    c: Weight(g71) = 1
    c: Equal(g71,g72)
    c: Equal(g71,g73)
    c: InternalAlignment(g71,g74)
    c: InternalAlignment(g72,g74)
    c: InternalAlignment(g73,g74)
    c: InternalAlignment(g75,g74)
    c: InternalAlignment(g76,g74)
    c: Block(g68)
    c: Block(g74)
    c: Coincident(g77,g68)
    c: Coincident(g77,g74)
    c: Vertical(g77)
    c: Coincident(g78,g68)
    c: Coincident(g78,g50)
    c: Coincident(g79,g50)
    c: Coincident(g79,g74)
    c: Weight(g80) = 1
    c: Equal(g80,g81)
    c: Equal(g80,g82)
    c: InternalAlignment(g80,g83)
    c: InternalAlignment(g81,g83)
    c: InternalAlignment(g82,g83)
    c: InternalAlignment(g84,g83)
    c: InternalAlignment(g85,g83)
    c: Weight(g86) = 1
    c: Equal(g86,g87)
    c: Equal(g86,g88)
    c: InternalAlignment(g86,g89)
    c: InternalAlignment(g87,g89)
    c: InternalAlignment(g88,g89)
    c: InternalAlignment(g90,g89)
    c: InternalAlignment(g91,g89)
    c: Block(g83)
    c: Block(g89)
    c: Coincident(g92,g83)
    c: Coincident(g92,g89)
    c: Vertical(g92)
    c: Coincident(g93,g83)
    c: Coincident(g93,g44)
    c: Coincident(g94,g44)
    c: Coincident(g94,g89)
    c: Weight(g95) = 1
    c: Equal(g95,g96)
    c: Equal(g95,g97)
    c: InternalAlignment(g95,g98)
    c: InternalAlignment(g96,g98)
    c: InternalAlignment(g97,g98)
    c: InternalAlignment(g99,g98)
    c: InternalAlignment(g100,g98)
    c: Weight(g101) = 1
    c: Equal(g101,g102)
    c: Equal(g101,g103)
    c: InternalAlignment(g101,g104)
    c: InternalAlignment(g102,g104)
    c: InternalAlignment(g103,g104)
    c: InternalAlignment(g105,g104)
    c: InternalAlignment(g106,g104)
    c: Block(g98)
    c: Block(g104)
    c: Coincident(g107,g98)
    c: Coincident(g107,g104)
    c: Vertical(g107)
    c: Coincident(g108,g104)
    c: Coincident(g108,g62)
    c: Coincident(g109,g62)
    c: Coincident(g109,g98)
    c: Weight(g110) = 1
    c: Equal(g110,g111)
    c: Equal(g110,g112)
    c: InternalAlignment(g110,g113)
    c: InternalAlignment(g111,g113)
    c: InternalAlignment(g112,g113)
    c: InternalAlignment(g114,g113)
    c: InternalAlignment(g115,g113)
    c: Weight(g116) = 1
    c: Equal(g116,g117)
    c: Equal(g116,g118)
    c: InternalAlignment(g116,g119)
    c: InternalAlignment(g117,g119)
    c: InternalAlignment(g118,g119)
    c: InternalAlignment(g120,g119)
    c: InternalAlignment(g121,g119)
    c: Block(g113)
    c: Block(g119)
    c: Coincident(g122,g113)
    c: Coincident(g122,g119)
    c: Vertical(g122)
    c: Coincident(g123,g119)
    c: Coincident(g123,g56)
    c: Coincident(g124,g56)
    c: Coincident(g124,g113)
    c: Weight(g125) = 1
    c: Equal(g125,g126)
    c: Equal(g125,g127)
    c: InternalAlignment(g125,g128)
    c: InternalAlignment(g126,g128)
    c: InternalAlignment(g127,g128)
    c: InternalAlignment(g129,g128)
    c: InternalAlignment(g130,g128)
    c: Weight(g131) = 1
    c: Equal(g131,g132)
    c: Equal(g131,g133)
    c: InternalAlignment(g131,g134)
    c: InternalAlignment(g132,g134)
    c: InternalAlignment(g133,g134)
    c: InternalAlignment(g135,g134)
    c: InternalAlignment(g136,g134)
    c: Weight(g137) = 1
    c: Equal(g137,g138)
    c: Equal(g137,g139)
    c: InternalAlignment(g137,g140)
    c: InternalAlignment(g138,g140)
    c: InternalAlignment(g139,g140)
    c: InternalAlignment(g141,g140)
    c: InternalAlignment(g142,g140)
    c: Weight(g143) = 1
    c: Equal(g143,g144)
    c: Equal(g143,g145)
    c: InternalAlignment(g143,g146)
    c: InternalAlignment(g144,g146)
    c: InternalAlignment(g145,g146)
    c: InternalAlignment(g147,g146)
    c: InternalAlignment(g148,g146)
    c: Block(g146)
    c: Block(g140)
    c: Block(g134)
    c: Block(g128)
    c: Coincident(g149,g25)
    c: Coincident(g149,g146)
    c: Coincident(g150,g146)
    c: Coincident(g150,g140)
    c: Horizontal(g150)
    c: Coincident(g151,g140)
    c: Coincident(g151,g25)
    c: Vertical(g151)
    c: Coincident(g152,g19)
    c: Coincident(g152,g134)
    c: Vertical(g152)
    c: Coincident(g153,g134)
    c: Coincident(g153,g128)
    c: Horizontal(g153)
    c: Coincident(g154,g128)
    c: Coincident(g154,g19)
    c: Weight(g155) = 1
    c: Equal(g155,g156)
    c: Equal(g155,g157)
    c: InternalAlignment(g155,g158)
    c: InternalAlignment(g156,g158)
    c: InternalAlignment(g157,g158)
    c: InternalAlignment(g159,g158)
    c: InternalAlignment(g160,g158)
    c: Weight(g161) = 1
    c: Equal(g161,g162)
    c: Equal(g161,g163)
    c: InternalAlignment(g161,g164)
    c: InternalAlignment(g162,g164)
    c: InternalAlignment(g163,g164)
    c: InternalAlignment(g165,g164)
    c: InternalAlignment(g166,g164)
    c: Weight(g167) = 1
    c: Equal(g167,g168)
    c: Equal(g167,g169)
    c: InternalAlignment(g167,g170)
    c: InternalAlignment(g168,g170)
    c: InternalAlignment(g169,g170)
    c: InternalAlignment(g171,g170)
    c: InternalAlignment(g172,g170)
    c: Weight(g173) = 1
    c: Equal(g173,g174)
    c: Equal(g173,g175)
    c: InternalAlignment(g173,g176)
    c: InternalAlignment(g174,g176)
    c: InternalAlignment(g175,g176)
    c: InternalAlignment(g177,g176)
    c: InternalAlignment(g178,g176)
    c: Block(g176)
    c: Block(g170)
    c: Block(g164)
    c: Block(g158)
    c: Coincident(g179,g170)
    c: Coincident(g179,g7)
    c: Vertical(g179)
    c: Coincident(g180,g13)
    c: Coincident(g180,g164)
    c: Vertical(g180)
    c: Coincident(g181,g158)
    c: Coincident(g181,g13)
    c: Coincident(g182,g7)
    c: Weight(g183) = 1
    c: Equal(g183,g184)
    c: Equal(g183,g185)
    c: InternalAlignment(g183,g186)
    c: InternalAlignment(g184,g186)
    c: InternalAlignment(g185,g186)
    c: InternalAlignment(g187,g186)
    c: InternalAlignment(g188,g186)
    c: Weight(g189) = 1
    c: Equal(g189,g190)
    c: Equal(g189,g191)
    c: InternalAlignment(g189,g192)
    c: InternalAlignment(g190,g192)
    c: InternalAlignment(g191,g192)
    c: InternalAlignment(g193,g192)
    c: InternalAlignment(g194,g192)
    c: Block(g192)
    c: Block(g186)
    c: Coincident(g195,g192)
    c: Coincident(g195,g31)
    c: Coincident(g196,g31)
    c: Coincident(g196,g186)
    c: Coincident(g197,g186)
    c: Coincident(g197,g192)
    c: Vertical(g197)
    c: Weight(g198) = 1
    c: Equal(g198,g199)
    c: Equal(g198,g200)
    c: InternalAlignment(g198,g201)
    c: InternalAlignment(g199,g201)
    c: InternalAlignment(g200,g201)
    c: InternalAlignment(g202,g201)
    c: InternalAlignment(g203,g201)
    c: Weight(g204) = 1
    c: Equal(g204,g205)
    c: Equal(g204,g206)
    c: InternalAlignment(g204,g207)
    c: InternalAlignment(g205,g207)
    c: InternalAlignment(g206,g207)
    c: InternalAlignment(g208,g207)
    c: InternalAlignment(g209,g207)
    c: Block(g207)
    c: Block(g201)
    c: Coincident(g210,g201)
    c: Coincident(g210,g37)
    c: Coincident(g211,g37)
    c: Coincident(g211,g207)
    c: Coincident(g212,g207)
    c: Coincident(g212,g201)
    c: Vertical(g212)
    c: Horizontal(g213)
    c: Block(g213)
    c: Vertical(g214)
    c: Block(g214)
    c: Block(g215)
    c: Weight(g216) = 1
    c: Equal(g216,g217)
    c: Equal(g216,g218)
    c: InternalAlignment(g216,g219)
    c: InternalAlignment(g217,g219)
    c: InternalAlignment(g218,g219)
    c: InternalAlignment(g220,g219)
    c: InternalAlignment(g221,g219)
    c: Weight(g222) = 1
    c: Equal(g222,g223)
    c: Equal(g222,g224)
    c: InternalAlignment(g222,g225)
    c: InternalAlignment(g223,g225)
    c: InternalAlignment(g224,g225)
    c: InternalAlignment(g226,g225)
    c: InternalAlignment(g227,g225)
    c: Weight(g228) = 1
    c: Equal(g228,g229)
    c: Equal(g228,g230)
    c: InternalAlignment(g228,g231)
    c: InternalAlignment(g229,g231)
    c: InternalAlignment(g230,g231)
    c: InternalAlignment(g232,g231)
    c: InternalAlignment(g233,g231)
    c: Weight(g234) = 1
    c: Equal(g234,g235)
    c: Equal(g234,g236)
    c: InternalAlignment(g234,g237)
    c: InternalAlignment(g235,g237)
    c: InternalAlignment(g236,g237)
    c: InternalAlignment(g238,g237)
    c: InternalAlignment(g239,g237)
    c: Block(g219)
    c: Block(g225)
    c: Block(g231)
    c: Block(g237)
    c: Coincident(g240,g225)
    c: Coincident(g240,g219)
    c: Horizontal(g240)
    c: Block(g182)
    c: Weight(g241) = 1
    c: Equal(g241,g242)
    c: Equal(g241,g243)
    c: InternalAlignment(g241,g244)
    c: InternalAlignment(g242,g244)
    c: InternalAlignment(g243,g244)
    c: InternalAlignment(g245,g244)
    c: InternalAlignment(g246,g244)
    c: Weight(g247) = 1
    c: Equal(g247,g248)
    c: Equal(g247,g249)
    c: InternalAlignment(g247,g250)
    c: InternalAlignment(g248,g250)
    c: InternalAlignment(g249,g250)
    c: InternalAlignment(g251,g250)
    c: InternalAlignment(g252,g250)
    c: Block(g244)
    c: Block(g250)
    c: Coincident(g253,g244)
    c: Coincident(g253,g250)
    c: Weight(g254) = 1
    c: Equal(g254,g255)
    c: Equal(g254,g256)
    c: InternalAlignment(g254,g257)
    c: InternalAlignment(g255,g257)
    c: InternalAlignment(g256,g257)
    c: InternalAlignment(g258,g257)
    c: InternalAlignment(g259,g257)
    c: Weight(g260) = 1
    c: Equal(g260,g261)
    c: Equal(g260,g262)
    c: InternalAlignment(g260,g263)
    c: InternalAlignment(g261,g263)
    c: InternalAlignment(g262,g263)
    c: InternalAlignment(g264,g263)
    c: InternalAlignment(g265,g263)
    c: Weight(g266) = 1
    c: Equal(g266,g267)
    c: Equal(g266,g268)
    c: InternalAlignment(g266,g269)
    c: InternalAlignment(g267,g269)
    c: InternalAlignment(g268,g269)
    c: InternalAlignment(g270,g269)
    c: InternalAlignment(g271,g269)
    c: Block(g269)
    c: Block(g263)
    c: Block(g257)
    c: Coincident(g272,g263)
    c: Coincident(g272,g257)
    c: Coincident(g273,g257)
    c: Coincident(g273,g269)
    c: Vertical(g273)
    c: Coincident(g274,g269)
    c: Coincident(g274,g263)
    c: Horizontal(g274)
    c: Weight(g275) = 1
    c: Equal(g275,g276)
    c: InternalAlignment(g275,g277)
    c: InternalAlignment(g276,g277)
    c: InternalAlignment(g278,g277)
    c: InternalAlignment(g279,g277)
    c: Weight(g280) = 1
    c: InternalAlignment(g281,g283)
    c: InternalAlignment(g282,g283)
    c: InternalAlignment(g284,g283)
    c: InternalAlignment(g285,g283)
    c: Weight(g286) = 1
    c: Equal(g286,g287)
    c: Equal(g286,g288)
    c: InternalAlignment(g286,g289)
    c: InternalAlignment(g287,g289)
    c: InternalAlignment(g288,g289)
    c: InternalAlignment(g290,g289)
    c: InternalAlignment(g291,g289)
    c: Equal(g292,g293)
    c: Equal(g292,g294)
    c: InternalAlignment(g292,g295)
    c: InternalAlignment(g293,g295)
    c: InternalAlignment(g294,g295)
    c: InternalAlignment(g296,g295)
    c: InternalAlignment(g297,g295)
    c: Block(g283)
    c: Block(g289)
    c: Block(g295)
    c: Block(g277)
    c: Coincident(g298,g277)
    c: Coincident(g298,g283)
    c: Horizontal(g298)
    c: Coincident(g299,g283)
    c: Coincident(g299,g289)
    c: Vertical(g299)
    c: Coincident(g300,g289)
    c: Coincident(g300,g295)
    c: Horizontal(g300)
    c: Coincident(g301,g295)
    c: Coincident(g301,g277)
    c: Weight(g302) = 1
    c: Equal(g302,g303)
    c: Equal(g302,g304)
    c: InternalAlignment(g302,g305)
    c: InternalAlignment(g303,g305)
    c: InternalAlignment(g304,g305)
    c: InternalAlignment(g306,g305)
    c: InternalAlignment(g307,g305)
    c: Weight(g308) = 1
    c: Equal(g308,g309)
    c: Equal(g308,g310)
    c: InternalAlignment(g308,g311)
    c: InternalAlignment(g309,g311)
    c: InternalAlignment(g310,g311)
    c: InternalAlignment(g312,g311)
    c: Weight(g314) = 1
    c: Equal(g314,g315)
    c: Equal(g314,g316)
    c: InternalAlignment(g314,g317)
    c: InternalAlignment(g315,g317)
    c: InternalAlignment(g316,g317)
    c: InternalAlignment(g318,g317)
    c: InternalAlignment(g319,g317)
    c: Block(g317)
    c: Block(g311)
    c: Block(g305)
    c: Coincident(g320,g317)
    c: Coincident(g320,g311)
    c: Horizontal(g320)
    c: Coincident(g321,g311)
    c: Coincident(g321,g305)
    c: Vertical(g321)
    c: Coincident(g322,g305)
    c: Coincident(g322,g317)
    c: InternalAlignment(g323,g324)
    c: InternalAlignment(g325,g324)
    c: InternalAlignment(g326,g324)
    c: Block(g324)
    c: Equal(g327,g328)
    c: Equal(g327,g329)
    c: InternalAlignment(g327,g330)
    c: InternalAlignment(g328,g330)
    c: InternalAlignment(g329,g330)
    c: InternalAlignment(g331,g330)
    c: InternalAlignment(g332,g330)
    c: Block(g330)
    c: Coincident(g333,g324)
    c: Horizontal(g333)
    c: Block(g333)
    c: Coincident(g334,g324)
    c: Coincident(g334,g250)
    c: Vertical(g334)
    c: Coincident(g335,g330)
    c: Coincident(g335,g244)
    c: Vertical(g335)
    c: Block(g336)
    c: Block(g2)
    c: Distance(g334) = 119.89
    c: Coincident(g337,g336)
    c: Coincident(g337,g2)
    c: Coincident(g338,g2)
    c: Coincident(g338,g336)
    c: Block(g3)
    c: Block(g339)
    c: Coincident(g340,g339)
    c: Coincident(g340,g3)
    c: Coincident(g341,g339)
    c: Coincident(g341,g3)
    c: Block(g341)
    c: Block(g340)
    c: Weight(g342) = 1
    c: Equal(g342,g344)
    c: InternalAlignment(g342,g345)
    c: InternalAlignment(g343,g345)
    c: InternalAlignment(g344,g345)
    c: InternalAlignment(g346,g345)
    c: InternalAlignment(g347,g345)
    c: InternalAlignment(g352,g351)
    c: InternalAlignment(g353,g351)
    c: InternalAlignment(g355,g357)
    c: Horizontal(g369)
    c: Coincident(g370,g0)
    c: Horizontal(g370)
    c: Block(g370)
    c: Distance(g370) = 450
    c: Horizontal(g371)
    c: Distance(g371) = 12
    c: Coincident(g373,g371)
    c: Vertical(g373)
    c: Horizontal(g374)
    c: Vertical(g375)
    c: Distance(g375) = 6
    c: Coincident(g375,g371)
    c: Coincident(g374,g371)
    c: Block(g373)
    c: Coincident(g376,g373)
    c: Horizontal(g376)
    c: Distance(g376) = 6
    c: Vertical(g377)
    c: Distance(g377) = 3
    c: Vertical(g378)
    c: Distance(g378) = 3
    c: Coincident(g372,g377)
    c: Coincident(g384,g378)
    c: Weight(g379) = 1
    c: Equal(g379,g380)
    c: Coincident(g380,g374)
    c: Equal(g379,g381)
    c: Coincident(g381,g375)
    c: Equal(g379,g382)
    c: Coincident(g382,g376)
    c: Equal(g379,g383)
    c: Coincident(g384,g377)
    c: InternalAlignment(g379-g383 -> g384) x5
    c: InternalAlignment(g385,g384)
    c: InternalAlignment(g386,g384)
    c: InternalAlignment(g387,g384)
    c: Coincident(g388,g164)
    c: Coincident(g388,g158)
    c: Coincident(g392,g390)
    c: Vertical(g393)
    c: Distance(g393) = 6
    c: Coincident(g393,g390)
    c: Vertical(g394)
    c: Distance(g394) = 3
    c: Vertical(g395)
    c: Distance(g395) = 6
    c: Coincident(g395,g394)
    c: Coincident(g401,g394)
    c: Weight(g396) = 1
    c: Equal(g396,g397)
    c: Coincident(g397,g392)
    c: Equal(g396,g398)
    c: Coincident(g398,g393)
    c: Equal(g396,g399)
    c: Equal(g396,g400)
    c: Coincident(g401,g395)
    c: InternalAlignment(g396-g400 -> g401) x5
    c: InternalAlignment(g402,g401)
    c: InternalAlignment(g403,g401)
    c: InternalAlignment(g404,g401)
    c: Coincident(g405,g389)
    c: Coincident(g405,g170)
    c: Horizontal(g405)
    c: Block(g401)
    c: Coincident(g406,g176)
    c: Coincident(g406,g389)
    c: Horizontal(g406)
    c: Block(g405)
    c: Coincident(g408,g389)
    c: PointOnObject(g408,g153)
    c: Vertical(g408)
    c: Block(g409)
    c: Coincident(g410,g409)
    c: Vertical(g410)
    c: PointOnObject(g410,g40)
    c: Block(g410)
    c: Coincident(g411,g409)
    c: Vertical(g411)
    c: Block(g411)
    c: Vertical(g412)
    c: Distance(g412) = 3
    c: Equal(g379,g415) = 1
    c: Equal(g415,g416)
    c: InternalAlignment(g415,g417)
    c: InternalAlignment(g416,g417)
    c: InternalAlignment(g413,g417)
    c: InternalAlignment(g414,g417)
    c: InternalAlignment(g418,g417)
    c: Block(g417)
    c: Coincident(g418,g412)
    c: Coincident(g419,g417)
    c: PointOnObject(g419,g150)
    c: Vertical(g419)
    c: Distance(g420) = 3
    c: Block(g420)
    c: Distance(g421) = 3
    c: Parallel(g421,g420)
    c: Coincident(g421,g420)
    c: Coincident(g422,g420)
    c: Perpendicular(g422,g420)
    c: Distance(g422) = 3
    c: Coincident(g423,g421)
    c: Perpendicular(g423,g421)
    c: Distance(g423) = 3
    c: Coincident(g424,g420)
    c: Perpendicular(g424,g421)
    c: Distance(g424) = 6
    c: Coincident(g425,g424)
    c: PointOnObject(g423,g425)
    c: Coincident(g426,g420)
    c: PointOnObject(g426,g79)
    c: Block(g426)
    c: Distance(g427) = 2.76
    c: Coincident(g428,g427)
    c: Parallel(g427,g428)
    c: PointOnObject(g428,g181)
    c: Distance(g428) = 2.41
    c: Block(g428)
    c: Coincident(g429,g427)
    c: Distance(g429) = 6.6
    c: Perpendicular(g429,g428)
    c: Distance(g430) = 6.6
    c: Coincident(g431,g429)
    c: Coincident(g431,g430)
    c: Block(g432)
    c: Coincident(g433,g432)
    c: Vertical(g433)
    c: Distance(g433) = 3.6
    c: Coincident(g434,g427)
    c: Parallel(g427,g434)
    c: PointOnObject(g434,g78)
    c: Block(g434)
    c: Coincident(g435,g421)
    c: Parallel(g435,g421)
    c: PointOnObject(g435,g211)
    c: Block(g435)
    c: Coincident(g436,g435)
    c: Vertical(g436)
    c: PointOnObject(g436,g210)
    c: Coincident(g437,g436)
    c: Perpendicular(g437,g210)
    c: Distance(g437) = 3
    c: Coincident(g438,g437)
    c: Block(g437)
    c: Distance(g438) = 3
    c: Parallel(g437,g438)
    c: Coincident(g439,g438)
    c: Distance(g439) = 3
    c: Parallel(g438,g439)
    c: Coincident(g440,g439)
    c: Parallel(g440,g437)
    c: PointOnObject(g440,g124)
    c: PointOnObject(g441,g53)
    c: Tangent(g440,g441)
    c: Coincident(g442,g439)
    c: Perpendicular(g442,g439)
    c: Coincident(g443,g437)
    c: Parallel(g443,g442)
    c: Distance(g443) = 3
    c: Distance(g442) = 3
    c: PointOnObject(g442,g444)
    c: Block(g444)
    c: PointOnObject(g445,g123)
    c: Perpendicular(g123,g445)
    c: Distance(g445) = 2.41
    c: Block(g445)
    c: Coincident(g446,g445)
    c: Perpendicular(g123,g446)
    c: Distance(g446) = 2.76
    c: Coincident(g447,g446)
    c: Perpendicular(g123,g447)
    c: PointOnObject(g447,g149)
    c: Coincident(g448,g445)
    c: Parallel(g123,g448)
    c: Distance(g448) = 6.6
    c: Coincident(g449,g446)
    c: Parallel(g123,g449)
    c: Coincident(g450,g448)
    c: Distance(g449) = 6.6
    c: Coincident(g449,g450)
    c: Block(g149)
    c: Block(g124)
    c: Block(g211)
    c: Block(g181)
    c: Block(g78)
    c: Block(g79)
    c: Block(g430)
    c: Coincident(g451,g447)
    c: Distance(g451) = 46
    c: Parallel(g149,g451)
    c: Coincident(g452,g451)
    c: Horizontal(g452)
    c: PointOnObject(g452,g154)
    c: Coincident(g453,g451)
    c: Vertical(g453)
    c: Distance(g453) = 9
    c: Block(g452)
    c: PointOnObject(g454,g93)
    c: Distance(g455) = 6.6
    c: Distance(g456) = 6.6
    c: Block(g454)
    c: Coincident(g457,g456)
    c: Coincident(g457,g455)
    c: Perpendicular(g457,g182)
    c: Coincident(g458,g455)
    c: Perpendicular(g458,g182)
    c: PointOnObject(g458,g182)
    c: Block(g458)
    c: Block(g457)
    c: Block(g456)
    c: PointOnObject(g459,g196)
    c: Perpendicular(g196,g459)
    c: Distance(g459) = 3
    c: Coincident(g460,g459)
    c: Perpendicular(g196,g460)
    c: Distance(g460) = 3
    c: Coincident(g461,g460)
    c: Perpendicular(g196,g461)
    c: Distance(g461) = 3
    c: Coincident(g462,g461)
    c: Tangent(g462,g41)
    c: PointOnObject(g462,g94)
    c: Block(g462)
    c: Block(g459)
    c: Coincident(g463,g459)
    c: Parallel(g196,g463)
    c: Distance(g463) = 3
    c: Coincident(g464,g461)
    c: Distance(g464) = 3
    c: Parallel(g196,g464)
    c: Coincident(g465,g460)
    c: Distance(g465) = 6
    c: Parallel(g465,g196)
    c: Coincident(g466,g465)
    c: PointOnObject(g464,g466)
    c: Block(g466)
    c: Coincident(g467,g458)
    c: Vertical(g467)
    c: PointOnObject(g467,g195)
    c: Coincident(g468,g467)
    c: Perpendicular(g195,g468)
FEATURE [Sketcher::SketchObject] Sketch004  label="rightSideBottom"
  FullyConstrained = false
  sketch-geometry (91):
    g0: ArcOfCircle CenterX=391.073 CenterY=-83.7794 CenterZ=0 NormalX=0 NormalY=0 NormalZ=1 AngleXU=0 Radius=8 StartAngle=3.14159 EndAngle=6.28319
    g1: Circle CenterX=306.073 CenterY=-81.8102 CenterZ=0 NormalX=0 NormalY=0 NormalZ=1 AngleXU=0 Radius=1
    g2: Circle CenterX=306.073 CenterY=-77.8102 CenterZ=0 NormalX=0 NormalY=0 NormalZ=1 AngleXU=0 Radius=1
    g3: Circle CenterX=302.567 CenterY=-42.9683 CenterZ=0 NormalX=0 NormalY=0 NormalZ=1 AngleXU=0 Radius=1
    g4: Circle CenterX=306.073 CenterY=-44.8935 CenterZ=0 NormalX=0 NormalY=0 NormalZ=1 AngleXU=0 Radius=1
    g5: Circle CenterX=306.073 CenterY=-40.8935 CenterZ=0 NormalX=0 NormalY=0 NormalZ=1 AngleXU=0 Radius=1
    g6: BSplineCurve PolesCount=3 KnotsCount=2 Degree=2 IsPeriodic=0
    g7: GeomPoint X=302.567 Y=-42.9683 Z=0
    g8: GeomPoint X=306.073 Y=-40.8935 Z=0
    g9: Circle CenterX=371.567 CenterY=-80.8644 CenterZ=0 NormalX=0 NormalY=0 NormalZ=1 AngleXU=0 Radius=1
    g10: Circle CenterX=375.073 CenterY=-82.7896 CenterZ=0 NormalX=0 NormalY=0 NormalZ=1 AngleXU=0 Radius=1
    g11: Circle CenterX=375.073 CenterY=-78.7896 CenterZ=0 NormalX=0 NormalY=0 NormalZ=1 AngleXU=0 Radius=1
    g12: GeomPoint X=371.567 Y=-80.8644 Z=0
    g13: GeomPoint X=375.073 Y=-78.7896 Z=0
    g14: Circle CenterX=318.073 CenterY=-51.4823 CenterZ=0 NormalX=0 NormalY=0 NormalZ=1 AngleXU=0 Radius=1
    g15: Circle CenterX=318.073 CenterY=-47.4805 CenterZ=0 NormalX=0 NormalY=0 NormalZ=1 AngleXU=0 Radius=1
    g16: GeomPoint X=321.579 Y=-53.4075 Z=0
    g17: GeomPoint X=318.073 Y=-47.4805 Z=0
    g18: Circle CenterX=321.579 CenterY=-67.3492 CenterZ=0 NormalX=0 NormalY=0 NormalZ=1 AngleXU=0 Radius=1
    g19: Circle CenterX=318.073 CenterY=-65.424 CenterZ=0 NormalX=0 NormalY=0 NormalZ=1 AngleXU=0 Radius=1
    g20: Circle CenterX=318.073 CenterY=-69.424 CenterZ=0 NormalX=0 NormalY=0 NormalZ=1 AngleXU=0 Radius=1
    g21: GeomPoint X=321.579 Y=-67.3492 Z=0
    g22: GeomPoint X=318.073 Y=-69.424 Z=0
    g23: Circle CenterX=362.567 CenterY=-89.8542 CenterZ=0 NormalX=0 NormalY=0 NormalZ=1 AngleXU=0 Radius=1
    g24: Circle CenterX=366.073 CenterY=-91.7794 CenterZ=0 NormalX=0 NormalY=0 NormalZ=1 AngleXU=0 Radius=1
    g25: Circle CenterX=362.073 CenterY=-91.7794 CenterZ=0 NormalX=0 NormalY=0 NormalZ=1 AngleXU=0 Radius=1
    g26: GeomPoint X=362.567 Y=-89.8542 Z=0
    g27: GeomPoint X=362.073 Y=-91.7794 Z=0
    g28: Circle CenterX=322.073 CenterY=-91.7794 CenterZ=0 NormalX=0 NormalY=0 NormalZ=1 AngleXU=0 Radius=1
    g29: Circle CenterX=318.073 CenterY=-91.7794 CenterZ=0 NormalX=0 NormalY=0 NormalZ=1 AngleXU=0 Radius=1
    g30: Circle CenterX=318.073 CenterY=-87.7794 CenterZ=0 NormalX=0 NormalY=0 NormalZ=1 AngleXU=0 Radius=1
    g31: GeomPoint X=322.073 Y=-91.7794 Z=0
    g32: GeomPoint X=318.073 Y=-87.7794 Z=0
    g33: ArcOfCircle CenterX=391.073 CenterY=22.1087 CenterZ=0 NormalX=0 NormalY=0 NormalZ=1 AngleXU=0 Radius=4 StartAngle=0 EndAngle=3.14159
    g34: LineSegment StartX=387.073 StartY=22.1087 StartZ=0 EndX=383.073 EndY=-83.7794 EndZ=0
    g35: LineSegment StartX=395.073 StartY=22.1087 StartZ=0 EndX=399.073 EndY=-83.7794 EndZ=0
    g36: LineSegment StartX=232.072 StartY=-103.779 StartZ=0 EndX=232.072 EndY=-100.779 EndZ=0
    g37: GeomPoint X=232.072 Y=-94.7794 Z=0
    g38: GeomPoint X=223.072 Y=-97.7794 Z=0
    g39: Circle CenterX=232.072 CenterY=-94.7794 CenterZ=0 NormalX=0 NormalY=0 NormalZ=1 AngleXU=0 Radius=1
    g40: Circle CenterX=232.072 CenterY=-100.779 CenterZ=0 NormalX=0 NormalY=0 NormalZ=1 AngleXU=0 Radius=1
    g41: BSplineCurve PolesCount=5 KnotsCount=3 Degree=3 IsPeriodic=0
    g42: GeomPoint X=232.072 Y=-100.779 Z=0
    g43: LineSegment StartX=232.072 StartY=-94.7794 StartZ=0 EndX=232.072 EndY=-91.7794 EndZ=0
    g44: LineSegment StartX=245.072 StartY=-31.3037 StartZ=0 EndX=243.535 EndY=-33.1602 EndZ=0
    g45: LineSegment StartX=241.775 StartY=-35.2862 StartZ=0 EndX=240.266 EndY=-37.1092 EndZ=0
    g46: LineSegment StartX=243.535 StartY=-33.1602 StartZ=0 EndX=248.619 EndY=-37.3688 EndZ=0
    g47: LineSegment StartX=241.775 StartY=-35.2862 StartZ=0 EndX=246.859 EndY=-39.4949 EndZ=0
    g48: LineSegment StartX=248.619 StartY=-37.3688 StartZ=0 EndX=246.859 EndY=-39.4949 EndZ=0
    g49: LineSegment StartX=232.072 StartY=-103.779 StartZ=0 EndX=407.073 EndY=-103.779 EndZ=0
    g50: LineSegment StartX=299.888 StartY=-86.6413 StartZ=0 EndX=240.266 EndY=-37.1092 EndZ=0
    g51: LineSegment StartX=245.072 StartY=-11.4025 StartZ=0 EndX=302.567 EndY=-42.9683 EndZ=0
    g52: BSplineCurve PolesCount=3 KnotsCount=2 Degree=2 IsPeriodic=0
    g53: BSplineCurve PolesCount=3 KnotsCount=2 Degree=2 IsPeriodic=0
    g54: LineSegment StartX=321.579 StartY=-53.4075 StartZ=0 EndX=371.567 EndY=-80.8644 EndZ=0
    g55: BSplineCurve PolesCount=3 KnotsCount=2 Degree=2 IsPeriodic=0
    g56: BSplineCurve PolesCount=3 KnotsCount=2 Degree=2 IsPeriodic=0
    g57: BSplineCurve PolesCount=3 KnotsCount=2 Degree=2 IsPeriodic=0
    g58: LineSegment StartX=318.073 StartY=-69.424 StartZ=0 EndX=318.073 EndY=-87.7794 EndZ=0
    g59: LineSegment StartX=321.579 StartY=-67.3492 StartZ=0 EndX=362.567 EndY=-89.8542 EndZ=0
    g60: LineSegment StartX=362.073 StartY=-91.7794 StartZ=0 EndX=322.073 EndY=-91.7794 EndZ=0
    g61: BSplineCurve PolesCount=3 KnotsCount=2 Degree=2 IsPeriodic=0
    g62: BSplineCurve PolesCount=3 KnotsCount=2 Degree=2 IsPeriodic=0
    g63: LineSegment StartX=245.072 StartY=-31.3037 StartZ=0 EndX=302.996 EndY=-79.2541 EndZ=0
    g64: LineSegment StartX=302.567 StartY=-56.9099 StartZ=0 EndX=239.193 EndY=-22.1109 EndZ=0
    g65: LineSegment StartX=306.073 StartY=-62.8351 StartZ=0 EndX=306.073 EndY=-77.8102 EndZ=0
    g66: BSplineCurve PolesCount=3 KnotsCount=2 Degree=2 IsPeriodic=0
    g67: LineSegment StartX=298.776 StartY=-91.7794 StartZ=0 EndX=232.072 EndY=-91.7794 EndZ=0
    g68: LineSegment StartX=245.072 StartY=-11.4025 StartZ=0 EndX=243.628 EndY=-14.0323 EndZ=0
    g69: LineSegment StartX=240.741 StartY=-19.2917 StartZ=0 EndX=239.193 EndY=-22.1109 EndZ=0
    g70: LineSegment StartX=243.628 StartY=-14.0323 StartZ=0 EndX=246.258 EndY=-15.476 EndZ=0
    g71: LineSegment StartX=240.741 StartY=-19.2917 StartZ=0 EndX=243.37 EndY=-20.7355 EndZ=0
    g72: ArcOfCircle CenterX=247.444 CenterY=-19.5495 CenterZ=0 NormalX=0 NormalY=0 NormalZ=1 AngleXU=0 Radius=4.24264 StartAngle=3.4249 EndAngle=8.13729
    g73: LineSegment StartX=407.073 StartY=-103.779 StartZ=0 EndX=407.073 EndY=48.2206 EndZ=0
    g74: LineSegment StartX=375.073 StartY=48.2206 StartZ=0 EndX=375.073 EndY=-78.7896 EndZ=0
    g75: LineSegment StartX=375.073 StartY=48.2206 StartZ=0 EndX=382.073 EndY=48.2206 EndZ=0
    g76: LineSegment StartX=407.073 StartY=48.2206 StartZ=0 EndX=400.073 EndY=48.2206 EndZ=0
    g77: LineSegment StartX=394.073 StartY=48.2206 StartZ=0 EndX=394.073 EndY=52.2206 EndZ=0
    g78: LineSegment StartX=388.073 StartY=48.2206 StartZ=0 EndX=388.073 EndY=58.2206 EndZ=0
    g79: ArcOfCircle CenterX=385.073 CenterY=61.2206 CenterZ=0 NormalX=0 NormalY=0 NormalZ=1 AngleXU=0 Radius=4.24264 StartAngle=5.49779 EndAngle=10.2102
    g80: ArcOfCircle CenterX=397.073 CenterY=55.2206 CenterZ=0 NormalX=0 NormalY=0 NormalZ=1 AngleXU=0 Radius=4.24264 StartAngle=5.49779 EndAngle=10.2102
    g81: LineSegment StartX=382.073 StartY=58.2206 StartZ=0 EndX=382.073 EndY=48.2206 EndZ=0
    g82: LineSegment StartX=400.073 StartY=52.2206 StartZ=0 EndX=400.073 EndY=48.2206 EndZ=0
    g83: LineSegment StartX=394.073 StartY=48.2206 StartZ=0 EndX=388.073 EndY=48.2206 EndZ=0
    g84: LineSegment StartX=306.073 StartY=-40.8935 StartZ=0 EndX=306.073 EndY=-27.5935 EndZ=0
    g85: LineSegment StartX=318.073 StartY=-27.5935 StartZ=0 EndX=318.073 EndY=-47.4805 EndZ=0
    g86: LineSegment StartX=306.073 StartY=-27.5935 StartZ=0 EndX=310.073 EndY=-27.5935 EndZ=0
    g87: LineSegment StartX=318.073 StartY=-27.5935 StartZ=0 EndX=314.073 EndY=-27.5935 EndZ=0
    g88: LineSegment StartX=310.073 StartY=-27.5935 StartZ=0 EndX=310.073 EndY=-31.5935 EndZ=0
    g89: LineSegment StartX=314.073 StartY=-27.5935 StartZ=0 EndX=314.073 EndY=-31.5935 EndZ=0
    g90: ArcOfCircle CenterX=312.073 CenterY=-33.5935 CenterZ=0 NormalX=0 NormalY=0 NormalZ=1 AngleXU=0 Radius=2.82843 StartAngle=2.35619 EndAngle=7.06858
  constraints (121):
    c: Distance(g44) = 2.41
    c: Block(g44)
    c: Coincident(g46,g44)
    c: Coincident(g49,g36)
    c: Horizontal(g49)
    c: Block(g49)
    c: Coincident(g50,g45)
    c: Block(g50)
    c: Coincident(g51,g6)
    c: Block(g51)
    c: Coincident(g54,g52)
    c: Coincident(g54,g53)
    c: Coincident(g58,g56)
    c: Coincident(g58,g57)
    c: Vertical(g58)
    c: Coincident(g59,g56)
    c: Coincident(g59,g55)
    c: Coincident(g60,g55)
    c: Coincident(g60,g57)
    c: Horizontal(g60)
    c: Block(g61)
    c: Block(g62)
    c: Coincident(g63,g44)
    c: Coincident(g63,g62)
    c: Coincident(g64,g61)
    c: Coincident(g65,g61)
    c: Coincident(g65,g62)
    c: Vertical(g65)
    c: Block(g66)
    c: Coincident(g66,g50)
    c: Coincident(g67,g66)
    c: Coincident(g67,g43)
    c: Horizontal(g67)
    c: Coincident(g68,g51)
    c: Perpendicular(g68,g51)
    c: Coincident(g69,g64)
    c: Coincident(g70,g68)
    c: Distance(g70) = 3
    c: Distance(g71) = 3
    c: Perpendicular(g68,g70)
    c: Coincident(g72,g70)
    c: Coincident(g72,g71)
    c: Block(g72)
    c: Block(g69)
    c: Block(g71)
    c: Block(g54)
    c: Block(g59)
    c: Block(g58)
    c: Block(g60)
    c: Block(g67)
    c: Block(g43)
    c: Block(g36)
    c: Block(g48)
    c: Block(g46)
    c: Block(g47)
    c: Block(g45)
    c: Block(g35)
    c: Block(g34)
    c: Block(g0)
    c: Block(g33)
    c: Block(g52)
    c: Block(g6)
    c: Block(g41)
    c: Block(g57)
    c: Block(g55)
    c: Block(g53)
    c: Block(g68)
    c: Distance(g48) = 2.76
    c: Distance(g47) = 6.6
    c: Distance(g45) = 2.36657
    c: Coincident(g73,g49)
    c: Vertical(g73)
    c: Distance(g73) = 152
    c: Coincident(g74,g53)
    c: Vertical(g74)
    c: Block(g74)
    c: Coincident(g75,g74)
    c: Horizontal(g75)
    c: Distance(g75) = 7
    c: Horizontal(g76)
    c: Distance(g76) = 7
    c: Coincident(g76,g73)
    c: Vertical(g77)
    c: Distance(g77) = 4
    c: Vertical(g78)
    c: Distance(g78) = 10
    c: Coincident(g79,g78)
    c: Coincident(g80,g77)
    c: Block(g80)
    c: Block(g79)
    c: Coincident(g81,g79)
    c: Coincident(g81,g75)
    c: Vertical(g81)
    c: Coincident(g82,g80)
    c: Coincident(g82,g76)
    c: Vertical(g82)
    c: Coincident(g83,g77)
    c: Coincident(g83,g78)
    c: Horizontal(g83)
    c: Coincident(g84,g6)
    c: Vertical(g84)
    c: Distance(g84) = 13.3
    c: Coincident(g85,g52)
    c: Vertical(g85)
    c: Block(g85)
    c: Coincident(g86,g84)
    c: Horizontal(g86)
    c: Distance(g86) = 4
    c: Coincident(g87,g85)
    c: Horizontal(g87)
    c: Distance(g87) = 4
    c: Coincident(g88,g86)
    c: Vertical(g88)
    c: Coincident(g89,g87)
    c: Vertical(g89)
    c: Distance(g88) = 4
    c: Distance(g89) = 4
    c: Coincident(g90,g88)
    c: Coincident(g90,g89)
    c: Block(g90)
    c: Block(g56)
FEATURE [Sketcher::SketchObject] Sketch005  label="middleTop"
  FullyConstrained = true
  sketch-geometry (133):
    g0: Circle CenterX=175.025 CenterY=27.0667 CenterZ=0 NormalX=0 NormalY=0 NormalZ=1 AngleXU=0 Radius=1
    g1: Circle CenterX=179.022 CenterY=24.8665 CenterZ=0 NormalX=0 NormalY=0 NormalZ=1 AngleXU=0 Radius=1
    g2: Circle CenterX=179.022 CenterY=27.0606 CenterZ=0 NormalX=0 NormalY=0 NormalZ=1 AngleXU=0 Radius=1
    g3: BSplineCurve PolesCount=3 KnotsCount=2 Degree=2 IsPeriodic=0
    g4: GeomPoint X=175.025 Y=27.0667 Z=0
    g5: GeomPoint X=179.022 Y=27.0606 Z=0
    g6: Circle CenterX=189.124 CenterY=27.0628 CenterZ=0 NormalX=0 NormalY=0 NormalZ=1 AngleXU=0 Radius=1
    g7: Circle CenterX=185.124 CenterY=24.8665 CenterZ=0 NormalX=0 NormalY=0 NormalZ=1 AngleXU=0 Radius=1
    g8: Circle CenterX=185.124 CenterY=27.0606 CenterZ=0 NormalX=0 NormalY=0 NormalZ=1 AngleXU=0 Radius=1
    g9: BSplineCurve PolesCount=3 KnotsCount=2 Degree=2 IsPeriodic=0
    g10: GeomPoint X=189.124 Y=27.0628 Z=0
    g11: GeomPoint X=185.124 Y=27.0606 Z=0
    g12: Circle CenterX=165.871 CenterY=18.1458 CenterZ=0 NormalX=0 NormalY=0 NormalZ=1 AngleXU=0 Radius=1
    g13: Circle CenterX=169.377 CenterY=16.2206 CenterZ=0 NormalX=0 NormalY=0 NormalZ=1 AngleXU=0 Radius=1
    g14: Circle CenterX=165.871 CenterY=14.2956 CenterZ=0 NormalX=0 NormalY=0 NormalZ=1 AngleXU=0 Radius=1
    g15: BSplineCurve PolesCount=3 KnotsCount=2 Degree=2 IsPeriodic=0
    g16: GeomPoint X=165.871 Y=18.1458 Z=0
    g17: GeomPoint X=165.871 Y=14.2956 Z=0
    g18: Circle CenterX=198.275 CenterY=18.1318 CenterZ=0 NormalX=0 NormalY=0 NormalZ=1 AngleXU=0 Radius=1
    g19: Circle CenterX=194.768 CenterY=16.2206 CenterZ=0 NormalX=0 NormalY=0 NormalZ=1 AngleXU=0 Radius=1
    g20: Circle CenterX=198.264 CenterY=14.2963 CenterZ=0 NormalX=0 NormalY=0 NormalZ=1 AngleXU=0 Radius=1
    g21: BSplineCurve PolesCount=3 KnotsCount=2 Degree=2 IsPeriodic=0
    g22: GeomPoint X=198.275 Y=18.1318 Z=0
    g23: GeomPoint X=198.264 Y=14.2963 Z=0
    g24: Circle CenterX=125.607 CenterY=54.1951 CenterZ=0 NormalX=0 NormalY=0 NormalZ=1 AngleXU=0 Radius=1
    g25: Circle CenterX=139.632 CenterY=46.4944 CenterZ=0 NormalX=0 NormalY=0 NormalZ=1 AngleXU=0 Radius=1
    g26: Circle CenterX=127.326 CenterY=56.7187 CenterZ=0 NormalX=0 NormalY=0 NormalZ=1 AngleXU=0 Radius=1
    g27: BSplineCurve PolesCount=3 KnotsCount=2 Degree=2 IsPeriodic=0
    g28: GeomPoint X=125.607 Y=54.1951 Z=0
    g29: GeomPoint X=127.326 Y=56.7187 Z=0
    g30: Circle CenterX=236.824 CenterY=56.7187 CenterZ=0 NormalX=0 NormalY=0 NormalZ=1 AngleXU=0 Radius=1
    g31: Circle CenterX=224.513 CenterY=46.4944 CenterZ=0 NormalX=0 NormalY=0 NormalZ=1 AngleXU=0 Radius=1
    g32: Circle CenterX=238.538 CenterY=54.1951 CenterZ=0 NormalX=0 NormalY=0 NormalZ=1 AngleXU=0 Radius=1
    g33: BSplineCurve PolesCount=3 KnotsCount=2 Degree=2 IsPeriodic=0
    g34: GeomPoint X=236.824 Y=56.7187 Z=0
    g35: GeomPoint X=238.538 Y=54.1951 Z=0
    g36: Circle CenterX=189.121 CenterY=124.221 CenterZ=0 NormalX=0 NormalY=0 NormalZ=1 AngleXU=0 Radius=1
    g37: Circle CenterX=185.124 CenterY=124.221 CenterZ=0 NormalX=0 NormalY=0 NormalZ=1 AngleXU=0 Radius=1
    g38: Circle CenterX=185.124 CenterY=120.221 CenterZ=0 NormalX=0 NormalY=0 NormalZ=1 AngleXU=0 Radius=1
    g39: BSplineCurve PolesCount=3 KnotsCount=2 Degree=2 IsPeriodic=0
    g40: GeomPoint X=189.121 Y=124.221 Z=0
    g41: GeomPoint X=185.124 Y=120.221 Z=0
    g42: Circle CenterX=175.022 CenterY=124.221 CenterZ=0 NormalX=0 NormalY=0 NormalZ=1 AngleXU=0 Radius=1
    g43: Circle CenterX=179.022 CenterY=124.221 CenterZ=0 NormalX=0 NormalY=0 NormalZ=1 AngleXU=0 Radius=1
    g44: Circle CenterX=179.022 CenterY=120.221 CenterZ=0 NormalX=0 NormalY=0 NormalZ=1 AngleXU=0 Radius=1
    g45: BSplineCurve PolesCount=3 KnotsCount=2 Degree=2 IsPeriodic=0
    g46: GeomPoint X=175.022 Y=124.221 Z=0
    g47: GeomPoint X=179.022 Y=120.221 Z=0
    g48: LineSegment StartX=232.071 StartY=124.221 StartZ=0 EndX=232.071 EndY=127.221 EndZ=0
    g49-g52: Circle x4 (B-spline internal-alignment scaffolding for g53; pole/knot coordinates omitted)
    g53: BSplineCurve PolesCount=5 KnotsCount=3 Degree=3 IsPeriodic=0
    g54: GeomPoint X=232.072 Y=133.221 Z=0
    g55: GeomPoint X=223.072 Y=130.221 Z=0
    g56: GeomPoint X=232.071 Y=127.221 Z=0
    g57-g61: Circle x5 (B-spline internal-alignment scaffolding for g62; pole/knot coordinates omitted)
    g62: BSplineCurve PolesCount=5 KnotsCount=3 Degree=3 IsPeriodic=0
    g63: GeomPoint X=132.072 Y=133.221 Z=0
    g64: GeomPoint X=141.072 Y=130.221 Z=0
    g65: GeomPoint X=132.072 Y=127.221 Z=0
    g66: ArcOfCircle CenterX=247.391 CenterY=52.0843 CenterZ=0 NormalX=0 NormalY=0 NormalZ=1 AngleXU=0 Radius=4.24264 StartAngle=4.42912 EndAngle=9.14151
    g67: LineSegment StartX=240.687 StartY=51.8263 StartZ=0 EndX=239.192 EndY=54.5542 EndZ=0
    g68: LineSegment StartX=243.575 StartY=46.5669 StartZ=0 EndX=245.072 EndY=43.8408 EndZ=0
    g69: LineSegment StartX=240.168 StartY=69.471 StartZ=0 EndX=241.708 EndY=67.6172 EndZ=0
    g70: LineSegment StartX=246.783 StartY=71.8328 StartZ=0 EndX=248.546 EndY=69.7098 EndZ=0
    g71: LineSegment StartX=245.073 StartY=63.5726 StartZ=0 EndX=243.476 EndY=65.4955 EndZ=0
    g72: LineSegment StartX=123.967 StartY=69.4706 StartZ=0 EndX=122.37 EndY=67.5474 EndZ=0
    g73: LineSegment StartX=232.072 StartY=133.221 StartZ=0 EndX=232.072 EndY=136.221 EndZ=0
    g74: LineSegment StartX=232.072 StartY=136.221 StartZ=0 EndX=132.072 EndY=136.221 EndZ=0
    g75: LineSegment StartX=132.072 StartY=136.221 StartZ=0 EndX=132.072 EndY=133.221 EndZ=0
    g76: LineSegment StartX=132.072 StartY=127.221 StartZ=0 EndX=132.072 EndY=124.221 EndZ=0
    g77: LineSegment StartX=132.072 StartY=124.221 StartZ=0 EndX=175.022 EndY=124.221 EndZ=0
    g78: LineSegment StartX=189.121 StartY=124.221 StartZ=0 EndX=232.071 EndY=124.221 EndZ=0
    g79: LineSegment StartX=185.124 StartY=120.221 StartZ=0 EndX=185.124 EndY=27.0606 EndZ=0
    g80: LineSegment StartX=189.124 StartY=27.0628 StartZ=0 EndX=240.168 EndY=69.471 EndZ=0
    g81: LineSegment StartX=241.708 StartY=67.6172 StartZ=0 EndX=246.783 EndY=71.8328 EndZ=0
    g82: LineSegment StartX=248.546 StartY=69.7098 StartZ=0 EndX=243.476 EndY=65.4955 EndZ=0
    g83: LineSegment StartX=245.073 StartY=63.5726 StartZ=0 EndX=236.824 EndY=56.7187 EndZ=0
    g84: LineSegment StartX=238.538 StartY=54.1951 StartZ=0 EndX=239.192 EndY=54.5542 EndZ=0
    g85: LineSegment StartX=240.687 StartY=51.8263 StartZ=0 EndX=243.317 EndY=53.2701 EndZ=0
    g86: LineSegment StartX=246.205 StartY=48.0108 StartZ=0 EndX=243.575 EndY=46.5669 EndZ=0
    g87: LineSegment StartX=245.072 StartY=43.8408 StartZ=0 EndX=198.275 EndY=18.1318 EndZ=0
    g88: LineSegment StartX=165.871 StartY=18.1458 StartZ=0 EndX=118.934 EndY=43.9178 EndZ=0
    g89: LineSegment StartX=118.934 StartY=43.9178 StartZ=0 EndX=120.377 EndY=46.5474 EndZ=0
    g90: LineSegment StartX=117.748 StartY=47.9913 StartZ=0 EndX=120.377 EndY=46.5474 EndZ=0
    g91: LineSegment StartX=120.635 StartY=53.2507 StartZ=0 EndX=123.265 EndY=51.8068 EndZ=0
    g92: LineSegment StartX=123.265 StartY=51.8068 StartZ=0 EndX=124.73 EndY=54.6766 EndZ=0
    g93: ArcOfCircle CenterX=116.562 CenterY=52.0649 CenterZ=0 NormalX=0 NormalY=0 NormalZ=1 AngleXU=0 Radius=4.24264 StartAngle=0.283267 EndAngle=4.99566
    g94: LineSegment StartX=124.73 StartY=54.6766 StartZ=0 EndX=125.607 EndY=54.1951 EndZ=0
    g95: LineSegment StartX=127.326 StartY=56.7187 StartZ=0 EndX=119.072 EndY=63.5741 EndZ=0
    g96: LineSegment StartX=119.072 StartY=63.5741 StartZ=0 EndX=120.669 EndY=65.4973 EndZ=0
    g97: LineSegment StartX=120.669 StartY=65.4973 StartZ=0 EndX=115.591 EndY=69.7147 EndZ=0
    g98: LineSegment StartX=115.591 StartY=69.7147 StartZ=0 EndX=117.293 EndY=71.7641 EndZ=0
    g99: LineSegment StartX=117.293 StartY=71.7641 StartZ=0 EndX=122.37 EndY=67.5474 EndZ=0
    g100: LineSegment StartX=123.967 StartY=69.4706 StartZ=0 EndX=175.025 EndY=27.0667 EndZ=0
    g101: LineSegment StartX=179.022 StartY=27.0606 StartZ=0 EndX=179.022 EndY=120.221 EndZ=0
    g102-g117: Circle x16 (B-spline internal-alignment scaffolding for g118; pole/knot coordinates omitted)
    g118: BSplineCurve PolesCount=16 KnotsCount=14 Degree=3 IsPeriodic=0
    g119-g132: GeomPoint x14 (B-spline internal-alignment scaffolding for g118; pole/knot coordinates omitted)
  constraints (180):
    c: Weight(g0) = 1
    c: Equal(g0,g1)
    c: Equal(g0,g2)
    c: InternalAlignment(g0,g3)
    c: InternalAlignment(g1,g3)
    c: InternalAlignment(g2,g3)
    c: InternalAlignment(g4,g3)
    c: InternalAlignment(g5,g3)
    c: Weight(g6) = 1
    c: Equal(g6,g7)
    c: Equal(g6,g8)
    c: InternalAlignment(g6,g9)
    c: InternalAlignment(g7,g9)
    c: InternalAlignment(g8,g9)
    c: InternalAlignment(g10,g9)
    c: InternalAlignment(g11,g9)
    c: Block(g9)
    c: Block(g3)
    c: Weight(g12) = 1
    c: Equal(g12,g13)
    c: Equal(g12,g14)
    c: InternalAlignment(g12,g15)
    c: InternalAlignment(g13,g15)
    c: InternalAlignment(g14,g15)
    c: InternalAlignment(g16,g15)
    c: InternalAlignment(g17,g15)
    c: Weight(g18) = 1
    c: Equal(g18,g19)
    c: Equal(g18,g20)
    c: InternalAlignment(g18,g21)
    c: InternalAlignment(g19,g21)
    c: InternalAlignment(g20,g21)
    c: InternalAlignment(g22,g21)
    c: InternalAlignment(g23,g21)
    c: Block(g15)
    c: Block(g21)
    c: Weight(g24) = 1
    c: Equal(g24,g25)
    c: Equal(g24,g26)
    c: InternalAlignment(g24,g27)
    c: InternalAlignment(g25,g27)
    c: InternalAlignment(g26,g27)
    c: InternalAlignment(g28,g27)
    c: InternalAlignment(g29,g27)
    c: Block(g27)
    c: Weight(g30) = 1
    c: Equal(g30,g31)
    c: Equal(g30,g32)
    c: InternalAlignment(g30,g33)
    c: InternalAlignment(g31,g33)
    c: InternalAlignment(g32,g33)
    c: InternalAlignment(g34,g33)
    c: InternalAlignment(g35,g33)
    c: Block(g33)
    c: Weight(g36) = 1
    c: Equal(g36,g37)
    c: Equal(g36,g38)
    c: InternalAlignment(g36,g39)
    c: InternalAlignment(g37,g39)
    c: InternalAlignment(g38,g39)
    c: InternalAlignment(g40,g39)
    c: InternalAlignment(g41,g39)
    c: Weight(g42) = 1
    c: Equal(g42,g43)
    c: Equal(g42,g44)
    c: InternalAlignment(g42,g45)
    c: InternalAlignment(g43,g45)
    c: InternalAlignment(g44,g45)
    c: InternalAlignment(g46,g45)
    c: InternalAlignment(g47,g45)
    c: Block(g45)
    c: Block(g39)
    c: Vertical(g48)
    c: Distance(g48) = 3
    c: Weight(g49) = 1
    c: Equal(g49,g50)
    c: Equal(g49,g51)
    c: Equal(g49,g52)
    c: Coincident(g53,g48)
    c: InternalAlignment(g49-g52 -> g53) x4
    c: InternalAlignment(g54,g53)
    c: InternalAlignment(g55,g53)
    c: InternalAlignment(g56,g53)
    c: Weight(g57) = 1
    c: Equal(g57, g58-g61) x4
    c: InternalAlignment(g57-g61 -> g62) x5
    c: InternalAlignment(g63,g62)
    c: InternalAlignment(g64,g62)
    c: InternalAlignment(g65,g62)
    c: Block(g62)
    c: Block(g67)
    c: Block(g68)
    c: Distance(g69) = 2.41
    c: Distance(g70) = 2.76
    c: Distance(g71) = 2.5
    c: Distance(g72) = 2.5
    c: Block(g66)
    c: Block(g48)
    c: Block(g53)
    c: Coincident(g73,g53)
    c: Vertical(g73)
    c: Distance(g73) = 3
    c: Coincident(g74,g73)
    c: Horizontal(g74)
    c: Distance(g74) = 100
    c: Coincident(g75,g74)
    c: Coincident(g75,g62)
    c: Vertical(g75)
    c: Distance(g75) = 3
    c: Coincident(g76,g62)
    c: Vertical(g76)
    c: Distance(g76) = 3
    c: Coincident(g77,g76)
    c: Coincident(g77,g45)
    c: Horizontal(g77)
    c: Distance(g77) = 42.95
    c: Coincident(g78,g39)
    c: Coincident(g78,g48)
    c: Horizontal(g78)
    c: Distance(g78) = 42.95
    c: Coincident(g79,g39)
    c: Coincident(g79,g9)
    c: Vertical(g79)
    c: Distance(g79) = 93.16
    c: Coincident(g80,g9)
    c: Coincident(g80,g69)
    c: Angle(g80) = 0.693245
    c: Block(g80)
    c: Coincident(g81,g69)
    c: Coincident(g81,g70)
    c: Block(g81)
    c: Coincident(g82,g70)
    c: Coincident(g82,g71)
    c: Block(g82)
    c: Coincident(g83,g71)
    c: Coincident(g83,g33)
    c: Block(g71)
    c: Coincident(g84,g33)
    c: Coincident(g84,g67)
    c: Coincident(g85,g67)
    c: Coincident(g85,g66)
    c: Coincident(g86,g66)
    c: Coincident(g86,g68)
    c: Coincident(g87,g68)
    c: Coincident(g87,g21)
    c: Coincident(g88,g15)
    c: Coincident(g89,g88)
    c: Block(g89)
    c: Coincident(g90,g89)
    c: Block(g90)
    c: Block(g91)
    c: Coincident(g92,g91)
    c: Block(g92)
    c: Coincident(g93,g91)
    c: Coincident(g93,g90)
    c: Block(g93)
    c: Coincident(g94,g92)
    c: Coincident(g94,g27)
    c: Coincident(g95,g27)
    c: Block(g95)
    c: Coincident(g96,g95)
    c: Coincident(g97,g96)
    c: Coincident(g98,g97)
    c: Coincident(g99,g98)
    c: Coincident(g99,g72)
    c: Block(g98)
    c: Block(g96)
    c: Block(g72)
    c: Coincident(g100,g72)
    c: Coincident(g100,g3)
    c: Coincident(g101,g3)
    c: Coincident(g101,g45)
    c: Vertical(g101)
    c: Coincident(g118,g21)
    c: Weight(g102) = 1
    c: Equal(g102, g103-g117) x15
    c: Coincident(g118,g15)
    c: InternalAlignment(g102-g117 -> g118) x16
    c: InternalAlignment(g119-g132 -> g118) x14
    c: Block(g118)
FEATURE [Sketcher::SketchObject] Sketch006  label="leftSideTop"
  FullyConstrained = true
  sketch-geometry (99):
    g0: Circle CenterX=61.1495 CenterY=111.695 CenterZ=0 NormalX=0 NormalY=0 NormalZ=1 AngleXU=0 Radius=1
    g1: Circle CenterX=58.0728 CenterY=114.251 CenterZ=0 NormalX=0 NormalY=0 NormalZ=1 AngleXU=0 Radius=1
    g2: Circle CenterX=58.0728 CenterY=110.251 CenterZ=0 NormalX=0 NormalY=0 NormalZ=1 AngleXU=0 Radius=1
    g3: BSplineCurve PolesCount=3 KnotsCount=2 Degree=2 IsPeriodic=0
    g4: GeomPoint X=61.1495 Y=111.695 Z=0
    g5: GeomPoint X=58.0728 Y=110.251 Z=0
    g6: Circle CenterX=61.5791 CenterY=89.3511 CenterZ=0 NormalX=0 NormalY=0 NormalZ=1 AngleXU=0 Radius=1
    g7: Circle CenterX=58.0728 CenterY=91.2763 CenterZ=0 NormalX=0 NormalY=0 NormalZ=1 AngleXU=0 Radius=1
    g8: Circle CenterX=58.0728 CenterY=95.2763 CenterZ=0 NormalX=0 NormalY=0 NormalZ=1 AngleXU=0 Radius=1
    g9: BSplineCurve PolesCount=3 KnotsCount=2 Degree=2 IsPeriodic=0
    g10: GeomPoint X=61.5791 Y=89.3511 Z=0
    g11: GeomPoint X=58.0728 Y=95.2763 Z=0
    g12: Circle CenterX=62.0728 CenterY=124.221 CenterZ=0 NormalX=0 NormalY=0 NormalZ=1 AngleXU=0 Radius=1
    g13: Circle CenterX=58.0728 CenterY=124.221 CenterZ=0 NormalX=0 NormalY=0 NormalZ=1 AngleXU=0 Radius=1
    g14: Circle CenterX=61.1496 CenterY=121.665 CenterZ=0 NormalX=0 NormalY=0 NormalZ=1 AngleXU=0 Radius=1
    g15: BSplineCurve PolesCount=3 KnotsCount=2 Degree=2 IsPeriodic=0
    g16: GeomPoint X=62.0728 Y=124.221 Z=0
    g17: GeomPoint X=61.1496 Y=121.665 Z=0
    g18: Circle CenterX=61.5791 CenterY=75.4095 CenterZ=0 NormalX=0 NormalY=0 NormalZ=1 AngleXU=0 Radius=1
    g19: Circle CenterX=58.0728 CenterY=77.3346 CenterZ=0 NormalX=0 NormalY=0 NormalZ=1 AngleXU=0 Radius=1
    g20: Circle CenterX=58.0728 CenterY=73.3346 CenterZ=0 NormalX=0 NormalY=0 NormalZ=1 AngleXU=0 Radius=1
    g21: BSplineCurve PolesCount=3 KnotsCount=2 Degree=2 IsPeriodic=0
    g22: GeomPoint X=61.5791 Y=75.4095 Z=0
    g23: GeomPoint X=58.0728 Y=73.3346 Z=0
    g24: Circle CenterX=2.07281 CenterY=124.221 CenterZ=0 NormalX=0 NormalY=0 NormalZ=1 AngleXU=0 Radius=1
    g25: Circle CenterX=1.57905 CenterY=122.295 CenterZ=0 NormalX=0 NormalY=0 NormalZ=1 AngleXU=0 Radius=1
    g26: BSplineCurve PolesCount=3 KnotsCount=2 Degree=2 IsPeriodic=0
    g27: GeomPoint X=2.07281 Y=124.221 Z=0
    g28: GeomPoint X=1.57905 Y=122.295 Z=0
    g29: Circle CenterX=46.0728 CenterY=124.221 CenterZ=0 NormalX=0 NormalY=0 NormalZ=1 AngleXU=0 Radius=1
    g30: Circle CenterX=46.0728 CenterY=120.221 CenterZ=0 NormalX=0 NormalY=0 NormalZ=1 AngleXU=0 Radius=1
    g31: BSplineCurve PolesCount=3 KnotsCount=2 Degree=2 IsPeriodic=0
    g32: GeomPoint X=42.0728 Y=124.221 Z=0
    g33: GeomPoint X=46.0728 Y=120.221 Z=0
    g34: Circle CenterX=46.0728 CenterY=109.865 CenterZ=0 NormalX=0 NormalY=0 NormalZ=1 AngleXU=0 Radius=1
    g35: Circle CenterX=46.0728 CenterY=105.865 CenterZ=0 NormalX=0 NormalY=0 NormalZ=1 AngleXU=0 Radius=1
    g36: Circle CenterX=42.0728 CenterY=105.865 CenterZ=0 NormalX=0 NormalY=0 NormalZ=1 AngleXU=0 Radius=1
    g37: BSplineCurve PolesCount=3 KnotsCount=2 Degree=2 IsPeriodic=0
    g38: GeomPoint X=46.0728 Y=109.865 Z=0
    g39: GeomPoint X=42.0728 Y=105.865 Z=0
    g40: Circle CenterX=35.5028 CenterY=105.865 CenterZ=0 NormalX=0 NormalY=0 NormalZ=1 AngleXU=0 Radius=1
    g41: Circle CenterX=31.5028 CenterY=105.865 CenterZ=0 NormalX=0 NormalY=0 NormalZ=1 AngleXU=0 Radius=1
    g42: Circle CenterX=27.9965 CenterY=107.79 CenterZ=0 NormalX=0 NormalY=0 NormalZ=1 AngleXU=0 Radius=1
    g43: BSplineCurve PolesCount=3 KnotsCount=2 Degree=2 IsPeriodic=0
    g44: GeomPoint X=35.5028 Y=105.865 Z=0
    g45: GeomPoint X=27.9965 Y=107.79 Z=0
    g46-g50: Circle x5 (B-spline internal-alignment scaffolding for g51; pole/knot coordinates omitted)
    g51: BSplineCurve PolesCount=5 KnotsCount=3 Degree=3 IsPeriodic=0
    g52: GeomPoint X=132.072 Y=133.221 Z=0
    g53: GeomPoint X=141.072 Y=130.221 Z=0
    g54: GeomPoint X=132.072 Y=127.221 Z=0
    g55: ArcOfCircle CenterX=116.562 CenterY=52.0649 CenterZ=0 NormalX=0 NormalY=0 NormalZ=1 AngleXU=0 Radius=4.24264 StartAngle=0.283268 EndAngle=4.99566
    g56: LineSegment StartX=123.967 StartY=69.4706 StartZ=0 EndX=122.37 EndY=67.5474 EndZ=0
    g57: LineSegment StartX=117.293 StartY=71.7641 StartZ=0 EndX=115.591 EndY=69.7147 EndZ=0
    g58: LineSegment StartX=120.669 StartY=65.4973 StartZ=0 EndX=119.072 EndY=63.5741 EndZ=0
    g59: LineSegment StartX=124.73 StartY=54.6766 StartZ=0 EndX=123.265 EndY=51.8068 EndZ=0
    g60: LineSegment StartX=120.377 StartY=46.5474 StartZ=0 EndX=118.934 EndY=43.9178 EndZ=0
    g61: BSplineCurve PolesCount=3 KnotsCount=2 Degree=2 IsPeriodic=0
    g62: BSplineCurve PolesCount=3 KnotsCount=2 Degree=2 IsPeriodic=0
    g63: LineSegment StartX=61.5791 StartY=75.4095 StartZ=0 EndX=118.934 EndY=43.9178 EndZ=0
    g64: LineSegment StartX=117.748 StartY=47.9913 StartZ=0 EndX=120.377 EndY=46.5474 EndZ=0
    g65: LineSegment StartX=120.635 StartY=53.2507 StartZ=0 EndX=123.265 EndY=51.8068 EndZ=0
    g66: LineSegment StartX=124.73 StartY=54.6766 StartZ=0 EndX=61.5791 EndY=89.3511 EndZ=0
    g67: LineSegment StartX=58.0728 StartY=95.2763 StartZ=0 EndX=58.0728 EndY=110.251 EndZ=0
    g68: LineSegment StartX=61.1495 StartY=111.695 StartZ=0 EndX=119.072 EndY=63.5741 EndZ=0
    g69: LineSegment StartX=120.669 StartY=65.4973 StartZ=0 EndX=115.591 EndY=69.7147 EndZ=0
    g70: LineSegment StartX=117.293 StartY=71.7641 StartZ=0 EndX=122.37 EndY=67.5474 EndZ=0
    g71: LineSegment StartX=123.967 StartY=69.4706 StartZ=0 EndX=61.1496 EndY=121.665 EndZ=0
    g72: LineSegment StartX=62.0728 StartY=124.221 StartZ=0 EndX=132.072 EndY=124.221 EndZ=0
    g73: LineSegment StartX=132.072 StartY=127.221 StartZ=0 EndX=132.072 EndY=124.221 EndZ=0
    g74: LineSegment StartX=132.072 StartY=133.221 StartZ=0 EndX=132.072 EndY=136.221 EndZ=0
    g75: LineSegment StartX=132.072 StartY=136.221 StartZ=0 EndX=-42.9272 EndY=136.221 EndZ=0
    g76: LineSegment StartX=2.07281 StartY=124.221 StartZ=0 EndX=42.0728 EndY=124.221 EndZ=0
    g77: LineSegment StartX=46.0728 StartY=120.221 StartZ=0 EndX=46.0728 EndY=109.865 EndZ=0
    g78: LineSegment StartX=42.0728 StartY=105.865 StartZ=0 EndX=35.5028 EndY=105.865 EndZ=0
    g79: LineSegment StartX=27.9965 StartY=107.79 StartZ=0 EndX=1.57905 EndY=122.295 EndZ=0
    g80: LineSegment StartX=-6.92718 StartY=76.4095 StartZ=0 EndX=42.0728 EndY=76.4095 EndZ=0
    g81: LineSegment StartX=-17.9272 StartY=48.2206 StartZ=0 EndX=-17.9272 EndY=58.2206 EndZ=0
    g82: LineSegment StartX=-35.9272 StartY=48.2206 StartZ=0 EndX=-35.9272 EndY=52.2206 EndZ=0
    g83: LineSegment StartX=-29.9272 StartY=48.2206 StartZ=0 EndX=-29.9272 EndY=52.2206 EndZ=0
    g84: LineSegment StartX=-23.9272 StartY=48.2206 StartZ=0 EndX=-23.9272 EndY=58.2206 EndZ=0
    g85: ArcOfCircle CenterX=-32.9272 CenterY=55.2206 CenterZ=0 NormalX=0 NormalY=0 NormalZ=1 AngleXU=0 Radius=4.24264 StartAngle=5.49779 EndAngle=10.2102
    g86: ArcOfCircle CenterX=-20.9272 CenterY=61.2206 CenterZ=0 NormalX=0 NormalY=0 NormalZ=1 AngleXU=0 Radius=4.24264 StartAngle=5.49779 EndAngle=10.2102
    g87: LineSegment StartX=-10.9272 StartY=48.2206 StartZ=0 EndX=-10.9272 EndY=72.4095 EndZ=0
    g88: LineSegment StartX=-42.9272 StartY=48.2206 StartZ=0 EndX=-42.9272 EndY=136.221 EndZ=0
    g89: LineSegment StartX=46.0728 StartY=72.4095 StartZ=0 EndX=46.0728 EndY=-27.5905 EndZ=0
    g90: LineSegment StartX=58.0728 StartY=-27.5905 StartZ=0 EndX=58.0728 EndY=73.3346 EndZ=0
    g91: LineSegment StartX=50.0728 StartY=-27.5905 StartZ=0 EndX=50.0728 EndY=-31.5905 EndZ=0
    g92: LineSegment StartX=54.0728 StartY=-27.5905 StartZ=0 EndX=54.0728 EndY=-31.5905 EndZ=0
    g93: ArcOfCircle CenterX=52.0728 CenterY=-33.5905 CenterZ=0 NormalX=0 NormalY=0 NormalZ=1 AngleXU=0 Radius=2.82843 StartAngle=2.35619 EndAngle=7.06858
    g94: LineSegment StartX=46.0728 StartY=-27.5905 StartZ=0 EndX=50.0728 EndY=-27.5905 EndZ=0
    g95: LineSegment StartX=54.0728 StartY=-27.5905 StartZ=0 EndX=58.0728 EndY=-27.5905 EndZ=0
    g96: LineSegment StartX=-17.9272 StartY=48.2206 StartZ=0 EndX=-10.9272 EndY=48.2206 EndZ=0
    g97: LineSegment StartX=-29.9272 StartY=48.2206 StartZ=0 EndX=-23.9272 EndY=48.2206 EndZ=0
    g98: LineSegment StartX=-42.9272 StartY=48.2206 StartZ=0 EndX=-35.9272 EndY=48.2206 EndZ=0
  constraints (172):
    c: Weight(g0) = 1
    c: Equal(g0,g1)
    c: Equal(g0,g2)
    c: InternalAlignment(g0,g3)
    c: InternalAlignment(g1,g3)
    c: InternalAlignment(g2,g3)
    c: InternalAlignment(g4,g3)
    c: InternalAlignment(g5,g3)
    c: Weight(g6) = 1
    c: Equal(g6,g7)
    c: Equal(g6,g8)
    c: InternalAlignment(g6,g9)
    c: InternalAlignment(g7,g9)
    c: InternalAlignment(g8,g9)
    c: InternalAlignment(g10,g9)
    c: InternalAlignment(g11,g9)
    c: Block(g3)
    c: Block(g9)
    c: Weight(g12) = 1
    c: Equal(g12,g13)
    c: Equal(g12,g14)
    c: InternalAlignment(g12,g15)
    c: InternalAlignment(g13,g15)
    c: InternalAlignment(g14,g15)
    c: InternalAlignment(g16,g15)
    c: InternalAlignment(g17,g15)
    c: Block(g15)
    c: Weight(g18) = 1
    c: Equal(g18,g19)
    c: Equal(g18,g20)
    c: InternalAlignment(g18,g21)
    c: InternalAlignment(g19,g21)
    c: InternalAlignment(g20,g21)
    c: InternalAlignment(g22,g21)
    c: InternalAlignment(g23,g21)
    c: Block(g21)
    c: Weight(g24) = 1
    c: Equal(g24,g25)
    c: InternalAlignment(g24,g26)
    c: InternalAlignment(g25,g26)
    c: InternalAlignment(g27,g26)
    c: InternalAlignment(g28,g26)
    c: InternalAlignment(g29,g31)
    c: InternalAlignment(g30,g31)
    c: InternalAlignment(g32,g31)
    c: InternalAlignment(g33,g31)
    c: Weight(g34) = 1
    c: Equal(g34,g35)
    c: Equal(g34,g36)
    c: InternalAlignment(g34,g37)
    c: InternalAlignment(g35,g37)
    c: InternalAlignment(g36,g37)
    c: InternalAlignment(g38,g37)
    c: InternalAlignment(g39,g37)
    c: Equal(g40,g41)
    c: Equal(g40,g42)
    c: InternalAlignment(g40,g43)
    c: InternalAlignment(g41,g43)
    c: InternalAlignment(g42,g43)
    c: InternalAlignment(g44,g43)
    c: InternalAlignment(g45,g43)
    c: Block(g31)
    c: Block(g37)
    c: Block(g43)
    c: Block(g26)
    c: Weight(g46) = 1
    c: Equal(g46, g47-g50) x4
    c: InternalAlignment(g46-g50 -> g51) x5
    c: InternalAlignment(g52,g51)
    c: InternalAlignment(g53,g51)
    c: InternalAlignment(g54,g51)
    c: Block(g51)
    c: Block(g55)
    c: Block(g56)
    c: Block(g57)
    c: Block(g58)
    c: Block(g59)
    c: Block(g60)
    c: Block(g61)
    c: Block(g62)
    c: Coincident(g90,g21)
    c: Coincident(g63,g21)
    c: Coincident(g63,g60)
    c: Coincident(g64,g55)
    c: Coincident(g64,g60)
    c: Coincident(g65,g55)
    c: Coincident(g65,g59)
    c: Coincident(g66,g59)
    c: Coincident(g66,g9)
    c: Coincident(g67,g9)
    c: Coincident(g67,g3)
    c: Vertical(g67)
    c: Coincident(g68,g3)
    c: Coincident(g68,g58)
    c: Coincident(g69,g58)
    c: Coincident(g69,g57)
    c: Coincident(g70,g57)
    c: Coincident(g70,g56)
    c: Coincident(g71,g56)
    c: Coincident(g71,g15)
    c: Coincident(g72,g15)
    c: Horizontal(g72)
    c: Coincident(g73,g51)
    c: Coincident(g73,g72)
    c: Vertical(g73)
    c: Coincident(g74,g51)
    c: Vertical(g74)
    c: Coincident(g75,g74)
    c: Horizontal(g75)
    c: Coincident(g76,g26)
    c: Coincident(g76,g31)
    c: Horizontal(g76)
    c: Coincident(g77,g31)
    c: Coincident(g77,g37)
    c: Vertical(g77)
    c: Coincident(g78,g37)
    c: Coincident(g78,g43)
    c: Horizontal(g78)
    c: Coincident(g79,g43)
    c: Coincident(g79,g26)
    c: Coincident(g80,g62)
    c: Coincident(g80,g61)
    c: Horizontal(g80)
    c: Vertical(g81)
    c: Distance(g81) = 10
    c: Vertical(g82)
    c: Distance(g82) = 4
    c: Vertical(g83)
    c: Distance(g83) = 4
    c: Vertical(g84)
    c: Distance(g84) = 10
    c: Coincident(g85,g83)
    c: Coincident(g85,g82)
    c: Block(g85)
    c: Coincident(g86,g84)
    c: Coincident(g86,g81)
    c: Block(g86)
    c: Coincident(g87,g62)
    c: Vertical(g87)
    c: Coincident(g88,g75)
    c: Vertical(g88)
    c: Block(g75)
    c: Coincident(g89,g61)
    c: Vertical(g89)
    c: Distance(g89) = 100
    c: Block(g90)
    c: Vertical(g91)
    c: Distance(g91) = 4
    c: Vertical(g92)
    c: Distance(g92) = 4
    c: Coincident(g93,g91)
    c: Coincident(g93,g92)
    c: Block(g93)
    c: Coincident(g94,g89)
    c: Coincident(g94,g91)
    c: Horizontal(g94)
    c: Distance(g94) = 4
    c: Coincident(g95,g92)
    c: Coincident(g95,g90)
    c: Horizontal(g95)
    c: Distance(g95) = 4
    c: Block(g87)
    c: Block(g88)
    c: Coincident(g96,g81)
    c: Coincident(g96,g87)
    c: Horizontal(g96)
    c: Coincident(g97,g83)
    c: Coincident(g97,g84)
    c: Horizontal(g97)
    c: Coincident(g98,g88)
    c: Coincident(g98,g82)
    c: Horizontal(g98)
FEATURE [Sketcher::SketchObject] Sketch007  label="leftSideBottom"
  FullyConstrained = true
  sketch-geometry (92):
    g0: ArcOfCircle CenterX=-26.9272 CenterY=-83.7794 CenterZ=0 NormalX=0 NormalY=0 NormalZ=1 AngleXU=0 Radius=8 StartAngle=3.14159 EndAngle=6.28319
    g1: Circle CenterX=61.5791 CenterY=-56.9099 CenterZ=0 NormalX=0 NormalY=0 NormalZ=1 AngleXU=0 Radius=1
    g2: Circle CenterX=58.0728 CenterY=-58.8351 CenterZ=0 NormalX=0 NormalY=0 NormalZ=1 AngleXU=0 Radius=1
    g3: Circle CenterX=58.0728 CenterY=-62.8351 CenterZ=0 NormalX=0 NormalY=0 NormalZ=1 AngleXU=0 Radius=1
    g4: BSplineCurve PolesCount=3 KnotsCount=2 Degree=2 IsPeriodic=0
    g5: GeomPoint X=61.5791 Y=-56.9099 Z=0
    g6: GeomPoint X=58.0728 Y=-62.8351 Z=0
    g7: Circle CenterX=58.0728 CenterY=-77.8102 CenterZ=0 NormalX=0 NormalY=0 NormalZ=1 AngleXU=0 Radius=1
    g8: Circle CenterX=58.0728 CenterY=-81.8102 CenterZ=0 NormalX=0 NormalY=0 NormalZ=1 AngleXU=0 Radius=1
    g9: Circle CenterX=61.1496 CenterY=-79.2541 CenterZ=0 NormalX=0 NormalY=0 NormalZ=1 AngleXU=0 Radius=1
    g10: BSplineCurve PolesCount=3 KnotsCount=2 Degree=2 IsPeriodic=0
    g11: GeomPoint X=58.0728 Y=-77.8102 Z=0
    g12: GeomPoint X=61.1496 Y=-79.2541 Z=0
    g13: Circle CenterX=61.6457 CenterY=-88.8112 CenterZ=0 NormalX=0 NormalY=0 NormalZ=1 AngleXU=0 Radius=1
    g14: Circle CenterX=58.0728 CenterY=-91.7794 CenterZ=0 NormalX=0 NormalY=0 NormalZ=1 AngleXU=0 Radius=1
    g15: Circle CenterX=63.9135 CenterY=-91.8014 CenterZ=0 NormalX=0 NormalY=0 NormalZ=1 AngleXU=0 Radius=1
    g16: BSplineCurve PolesCount=3 KnotsCount=2 Degree=2 IsPeriodic=0
    g17: GeomPoint X=61.6457 Y=-88.8112 Z=0
    g18: GeomPoint X=63.9135 Y=-91.8014 Z=0
    g19: Circle CenterX=58.0728 CenterY=-40.8935 CenterZ=0 NormalX=0 NormalY=0 NormalZ=1 AngleXU=0 Radius=1
    g20: Circle CenterX=58.0728 CenterY=-44.8935 CenterZ=0 NormalX=0 NormalY=0 NormalZ=1 AngleXU=0 Radius=1
    g21: Circle CenterX=61.5791 CenterY=-42.9683 CenterZ=0 NormalX=0 NormalY=0 NormalZ=1 AngleXU=0 Radius=1
    g22: BSplineCurve PolesCount=3 KnotsCount=2 Degree=2 IsPeriodic=0
    g23: GeomPoint X=58.0728 Y=-40.8935 Z=0
    g24: GeomPoint X=61.5791 Y=-42.9683 Z=0
    g25: Circle CenterX=42.5666 CenterY=-67.3492 CenterZ=0 NormalX=0 NormalY=0 NormalZ=1 AngleXU=0 Radius=1
    g26: Circle CenterX=46.0728 CenterY=-65.424 CenterZ=0 NormalX=0 NormalY=0 NormalZ=1 AngleXU=0 Radius=1
    g27: Circle CenterX=46.0728 CenterY=-69.424 CenterZ=0 NormalX=0 NormalY=0 NormalZ=1 AngleXU=0 Radius=1
    g28: BSplineCurve PolesCount=3 KnotsCount=2 Degree=2 IsPeriodic=0
    g29: GeomPoint X=42.5666 Y=-67.3492 Z=0
    g30: GeomPoint X=46.0728 Y=-69.424 Z=0
    g31: Circle CenterX=2.07281 CenterY=-91.7794 CenterZ=0 NormalX=0 NormalY=0 NormalZ=1 AngleXU=0 Radius=1
    g32: Circle CenterX=-1.92719 CenterY=-91.7794 CenterZ=0 NormalX=0 NormalY=0 NormalZ=1 AngleXU=0 Radius=1
    g33: Circle CenterX=1.57905 CenterY=-89.8542 CenterZ=0 NormalX=0 NormalY=0 NormalZ=1 AngleXU=0 Radius=1
    g34: BSplineCurve PolesCount=3 KnotsCount=2 Degree=2 IsPeriodic=0
    g35: GeomPoint X=2.07281 Y=-91.7794 Z=0
    g36: GeomPoint X=1.57905 Y=-89.8542 Z=0
    g37: ArcOfCircle CenterX=-26.9272 CenterY=22.1087 CenterZ=0 NormalX=0 NormalY=0 NormalZ=1 AngleXU=0 Radius=4 StartAngle=5e-16 EndAngle=3.14159
    g38: Circle CenterX=-10.9272 CenterY=-78.7794 CenterZ=0 NormalX=0 NormalY=0 NormalZ=1 AngleXU=0 Radius=1
    g39: Circle CenterX=-10.9272 CenterY=-82.7794 CenterZ=0 NormalX=0 NormalY=0 NormalZ=1 AngleXU=0 Radius=1
    g40: Circle CenterX=-7.42095 CenterY=-80.8542 CenterZ=0 NormalX=0 NormalY=0 NormalZ=1 AngleXU=0 Radius=1
    g41: BSplineCurve PolesCount=3 KnotsCount=2 Degree=2 IsPeriodic=0
    g42: GeomPoint X=-10.9272 Y=-78.7794 Z=0
    g43: GeomPoint X=-7.42095 Y=-80.8542 Z=0
    g44: BSplineCurve PolesCount=3 KnotsCount=2 Degree=2 IsPeriodic=0
    g45: GeomPoint X=42.5666 Y=-53.4075 Z=0
    g46: GeomPoint X=46.0728 Y=-47.4823 Z=0
    g47: BSplineCurve PolesCount=5 KnotsCount=3 Degree=3 IsPeriodic=0
    g48: LineSegment StartX=124.814 StartY=-22.1885 StartZ=0 EndX=123.265 EndY=-19.3655 EndZ=0
    g49: ArcOfCircle CenterX=116.562 CenterY=-19.6236 CenterZ=0 NormalX=0 NormalY=0 NormalZ=1 AngleXU=0 Radius=4.24264 StartAngle=1.28753 EndAngle=6.00037
    g50: LineSegment StartX=-30.9272 StartY=22.1087 StartZ=0 EndX=-34.9272 EndY=-83.7794 EndZ=0
    g51: LineSegment StartX=-22.9272 StartY=22.1087 StartZ=0 EndX=-18.9272 EndY=-83.7794 EndZ=0
    g52: LineSegment StartX=118.934 StartY=-11.4765 StartZ=0 EndX=120.377 EndY=-14.1062 EndZ=0
    g53: LineSegment StartX=118.86 StartY=-31.3104 StartZ=0 EndX=120.377 EndY=-33.1447 EndZ=0
    g54: LineSegment StartX=115.291 StartY=-37.3514 StartZ=0 EndX=117.05 EndY=-39.4781 EndZ=0
    g55: LineSegment StartX=122.136 StartY=-35.2714 StartZ=0 EndX=123.656 EndY=-37.1092 EndZ=0
    g56: BSplineCurve PolesCount=3 KnotsCount=2 Degree=2 IsPeriodic=0
    g57: LineSegment StartX=132.072 StartY=-100.779 StartZ=0 EndX=132.072 EndY=-103.779 EndZ=0
    g58: LineSegment StartX=132.072 StartY=-91.8014 StartZ=0 EndX=132.072 EndY=-94.7791 EndZ=0
    g59: LineSegment StartX=63.9135 StartY=-91.8014 StartZ=0 EndX=132.072 EndY=-91.8014 EndZ=0
    g60: LineSegment StartX=61.6457 StartY=-88.8112 StartZ=0 EndX=123.656 EndY=-37.1092 EndZ=0
    g61: LineSegment StartX=122.136 StartY=-35.2714 StartZ=0 EndX=117.05 EndY=-39.4781 EndZ=0
    g62: LineSegment StartX=115.291 StartY=-37.3514 StartZ=0 EndX=120.377 EndY=-33.1447 EndZ=0
    g63: LineSegment StartX=118.86 StartY=-31.3104 StartZ=0 EndX=61.1496 EndY=-79.2541 EndZ=0
    g64: LineSegment StartX=58.0728 StartY=-77.8102 StartZ=0 EndX=58.0728 EndY=-62.8351 EndZ=0
    g65: LineSegment StartX=61.5791 StartY=-56.9099 StartZ=0 EndX=124.814 EndY=-22.1885 EndZ=0
    g66: LineSegment StartX=120.636 StartY=-20.8076 StartZ=0 EndX=123.265 EndY=-19.3655 EndZ=0
    g67: LineSegment StartX=117.748 StartY=-15.55 StartZ=0 EndX=120.377 EndY=-14.1062 EndZ=0
    g68: LineSegment StartX=118.934 StartY=-11.4765 StartZ=0 EndX=61.5791 EndY=-42.9683 EndZ=0
    g69: LineSegment StartX=-42.9272 StartY=-103.779 StartZ=0 EndX=132.072 EndY=-103.779 EndZ=0
    g70: LineSegment StartX=42.5666 StartY=-53.4075 StartZ=0 EndX=-7.42095 EndY=-80.8542 EndZ=0
    g71: LineSegment StartX=-10.9272 StartY=-78.7794 StartZ=0 EndX=-10.9272 EndY=48.2206 EndZ=0
    g72: LineSegment StartX=2.07281 StartY=-91.7794 StartZ=0 EndX=42.0728 EndY=-91.7794 EndZ=0
    g73: LineSegment StartX=46.0728 StartY=-87.7794 StartZ=0 EndX=46.0728 EndY=-69.424 EndZ=0
    g74: LineSegment StartX=42.5666 StartY=-67.3492 StartZ=0 EndX=1.57905 EndY=-89.8542 EndZ=0
    g75: LineSegment StartX=-42.9272 StartY=-103.779 StartZ=0 EndX=-42.9272 EndY=48.2206 EndZ=0
    g76: LineSegment StartX=-17.9272 StartY=48.2206 StartZ=0 EndX=-17.9272 EndY=58.2206 EndZ=0
    g77: LineSegment StartX=-35.9272 StartY=48.2206 StartZ=0 EndX=-35.9272 EndY=52.2206 EndZ=0
    g78: LineSegment StartX=-29.9272 StartY=48.2206 StartZ=0 EndX=-29.9272 EndY=52.2206 EndZ=0
    g79: LineSegment StartX=-23.9272 StartY=48.2206 StartZ=0 EndX=-23.9272 EndY=58.2206 EndZ=0
    g80: ArcOfCircle CenterX=-32.9272 CenterY=55.2206 CenterZ=0 NormalX=0 NormalY=0 NormalZ=1 AngleXU=0 Radius=4.24264 StartAngle=5.49779 EndAngle=10.2102
    g81: ArcOfCircle CenterX=-20.9272 CenterY=61.2206 CenterZ=0 NormalX=0 NormalY=0 NormalZ=1 AngleXU=0 Radius=4.24264 StartAngle=5.49779 EndAngle=10.2102
    g82: LineSegment StartX=-17.9272 StartY=48.2206 StartZ=0 EndX=-10.9272 EndY=48.2206 EndZ=0
    g83: LineSegment StartX=-42.9272 StartY=48.2206 StartZ=0 EndX=-35.9272 EndY=48.2206 EndZ=0
    g84: LineSegment StartX=50.0728 StartY=-27.5905 StartZ=0 EndX=50.0728 EndY=-31.5905 EndZ=0
    g85: LineSegment StartX=54.0728 StartY=-27.5905 StartZ=0 EndX=54.0728 EndY=-31.5905 EndZ=0
    g86: ArcOfCircle CenterX=52.0728 CenterY=-33.5905 CenterZ=0 NormalX=0 NormalY=0 NormalZ=1 AngleXU=0 Radius=2.82843 StartAngle=2.35619 EndAngle=7.06858
    g87: LineSegment StartX=46.0728 StartY=-27.5905 StartZ=0 EndX=50.0728 EndY=-27.5905 EndZ=0
    g88: LineSegment StartX=54.0728 StartY=-27.5905 StartZ=0 EndX=58.0728 EndY=-27.5905 EndZ=0
    g89: LineSegment StartX=46.0728 StartY=-27.5905 StartZ=0 EndX=46.0728 EndY=-47.4823 EndZ=0
    g90: LineSegment StartX=58.0728 StartY=-27.5905 StartZ=0 EndX=58.0728 EndY=-40.8935 EndZ=0
    g91: LineSegment StartX=-29.9272 StartY=48.2206 StartZ=0 EndX=-23.9272 EndY=48.2206 EndZ=0
  constraints (170):
    c: Weight(g1) = 1
    c: Equal(g1,g2)
    c: Equal(g1,g3)
    c: InternalAlignment(g1,g4)
    c: InternalAlignment(g2,g4)
    c: InternalAlignment(g3,g4)
    c: InternalAlignment(g5,g4)
    c: InternalAlignment(g6,g4)
    c: Weight(g7) = 1
    c: Equal(g7,g8)
    c: Equal(g7,g9)
    c: InternalAlignment(g7,g10)
    c: InternalAlignment(g8,g10)
    c: InternalAlignment(g9,g10)
    c: InternalAlignment(g11,g10)
    c: InternalAlignment(g12,g10)
    c: Block(g4)
    c: Block(g10)
    c: Weight(g13) = 1
    c: Equal(g13,g14)
    c: Equal(g13,g15)
    c: InternalAlignment(g13,g16)
    c: InternalAlignment(g14,g16)
    c: InternalAlignment(g15,g16)
    c: InternalAlignment(g17,g16)
    c: InternalAlignment(g18,g16)
    c: Block(g16)
    c: Weight(g19) = 1
    c: Equal(g19,g20)
    c: Equal(g19,g21)
    c: InternalAlignment(g19,g22)
    c: InternalAlignment(g20,g22)
    c: InternalAlignment(g21,g22)
    c: InternalAlignment(g23,g22)
    c: InternalAlignment(g24,g22)
    c: Block(g22)
    c: Weight(g25) = 1
    c: Equal(g25,g26)
    c: Equal(g25,g27)
    c: InternalAlignment(g25,g28)
    c: InternalAlignment(g26,g28)
    c: InternalAlignment(g27,g28)
    c: InternalAlignment(g29,g28)
    c: InternalAlignment(g30,g28)
    c: Weight(g31) = 1
    c: Equal(g31,g32)
    c: Equal(g31,g33)
    c: InternalAlignment(g31,g34)
    c: InternalAlignment(g32,g34)
    c: InternalAlignment(g33,g34)
    c: InternalAlignment(g35,g34)
    c: InternalAlignment(g36,g34)
    c: Block(g34)
    c: Block(g28)
    c: Block(g37)
    c: Block(g0)
    c: Weight(g38) = 1
    c: Equal(g38,g40)
    c: InternalAlignment(g38,g41)
    c: InternalAlignment(g39,g41)
    c: InternalAlignment(g40,g41)
    c: InternalAlignment(g42,g41)
    c: InternalAlignment(g43,g41)
    c: InternalAlignment(g45,g44)
    c: InternalAlignment(g46,g44)
    c: Block(g47)
    c: Block(g44)
    c: Block(g41)
    c: Block(g48)
    c: Block(g49)
    c: Coincident(g50,g37)
    c: Coincident(g50,g0)
    c: Coincident(g51,g37)
    c: Coincident(g51,g0)
    c: Block(g51)
    c: Block(g50)
    c: Block(g52)
    c: Block(g53)
    c: Block(g54)
    c: Block(g55)
    c: Block(g56)
    c: Coincident(g57,g47)
    c: Vertical(g57)
    c: Coincident(g58,g47)
    c: Vertical(g58)
    c: Coincident(g59,g16)
    c: Coincident(g59,g58)
    c: Horizontal(g59)
    c: Coincident(g60,g16)
    c: Coincident(g60,g55)
    c: Coincident(g61,g55)
    c: Coincident(g61,g54)
    c: Coincident(g62,g54)
    c: Coincident(g62,g53)
    c: Coincident(g63,g53)
    c: Coincident(g63,g10)
    c: Coincident(g64,g10)
    c: Coincident(g64,g4)
    c: Vertical(g64)
    c: Coincident(g65,g4)
    c: Coincident(g65,g48)
    c: Coincident(g66,g49)
    c: Coincident(g66,g48)
    c: Coincident(g67,g49)
    c: Coincident(g67,g52)
    c: Coincident(g68,g52)
    c: Coincident(g68,g22)
    c: Coincident(g69,g57)
    c: Horizontal(g69)
    c: Coincident(g70,g44)
    c: Coincident(g70,g41)
    c: Coincident(g71,g41)
    c: Vertical(g71)
    c: Coincident(g72,g34)
    c: Coincident(g72,g56)
    c: Horizontal(g72)
    c: Coincident(g73,g56)
    c: Coincident(g73,g28)
    c: Vertical(g73)
    c: Coincident(g74,g28)
    c: Coincident(g74,g34)
    c: Block(g69)
    c: Coincident(g75,g69)
    c: Vertical(g75)
    c: Distance(g75) = 152
    c: Block(g71)
    c: Vertical(g76)
    c: Distance(g76) = 10
    c: Vertical(g77)
    c: Distance(g77) = 4
    c: Vertical(g78)
    c: Distance(g78) = 4
    c: Vertical(g79)
    c: Distance(g79) = 10
    c: Coincident(g80,g78)
    c: Coincident(g80,g77)
    c: Block(g80)
    c: Coincident(g81,g79)
    c: Coincident(g81,g76)
    c: Block(g81)
    c: Coincident(g82,g76)
    c: Coincident(g82,g71)
    c: Horizontal(g82)
    c: Coincident(g83,g75)
    c: Coincident(g83,g77)
    c: Horizontal(g83)
    c: Distance(g83) = 7
    c: Distance(g82) = 7
    c: Vertical(g84)
    c: Distance(g84) = 4
    c: Vertical(g85)
    c: Distance(g85) = 4
    c: Coincident(g86,g84)
    c: Coincident(g86,g85)
    c: Block(g86)
    c: Coincident(g87,g84)
    c: Horizontal(g87)
    c: Distance(g87) = 4
    c: Coincident(g88,g85)
    c: Horizontal(g88)
    c: Distance(g88) = 4
    c: Coincident(g89,g87)
    c: Coincident(g89,g44)
    c: Vertical(g89)
    c: Coincident(g90,g88)
    c: Coincident(g90,g22)
    c: Vertical(g90)
    c: Coincident(g91,g78)
    c: Coincident(g91,g79)
    c: Horizontal(g91)
FEATURE [Sketcher::SketchObject] Sketch008  label="rightSideTop"
  FullyConstrained = false
  sketch-geometry (108):
    g0: Circle CenterX=302.996 CenterY=111.695 CenterZ=0 NormalX=0 NormalY=0 NormalZ=1 AngleXU=0 Radius=1
    g1: Circle CenterX=306.073 CenterY=114.251 CenterZ=0 NormalX=0 NormalY=0 NormalZ=1 AngleXU=0 Radius=1
    g2: Circle CenterX=306.073 CenterY=110.251 CenterZ=0 NormalX=0 NormalY=0 NormalZ=1 AngleXU=0 Radius=1
    g3: BSplineCurve PolesCount=3 KnotsCount=2 Degree=2 IsPeriodic=0
    g4: GeomPoint X=302.996 Y=111.695 Z=0
    g5: GeomPoint X=306.073 Y=110.251 Z=0
    g6: Circle CenterX=306.073 CenterY=95.2763 CenterZ=0 NormalX=0 NormalY=0 NormalZ=1 AngleXU=0 Radius=1
    g7: Circle CenterX=306.073 CenterY=91.2763 CenterZ=0 NormalX=0 NormalY=0 NormalZ=1 AngleXU=0 Radius=1
    g8: Circle CenterX=302.567 CenterY=89.3511 CenterZ=0 NormalX=0 NormalY=0 NormalZ=1 AngleXU=0 Radius=1
    g9: BSplineCurve PolesCount=3 KnotsCount=2 Degree=2 IsPeriodic=0
    g10: GeomPoint X=306.073 Y=95.2763 Z=0
    g11: GeomPoint X=302.567 Y=89.3511 Z=0
    g12: LineSegment StartX=306.073 StartY=110.251 StartZ=0 EndX=306.073 EndY=95.2763 EndZ=0
    g13: Circle CenterX=302.073 CenterY=124.221 CenterZ=0 NormalX=0 NormalY=0 NormalZ=1 AngleXU=0 Radius=1
    g14: Circle CenterX=306.073 CenterY=124.221 CenterZ=0 NormalX=0 NormalY=0 NormalZ=1 AngleXU=0 Radius=1
    g15: Circle CenterX=302.996 CenterY=121.665 CenterZ=0 NormalX=0 NormalY=0 NormalZ=1 AngleXU=0 Radius=1
    g16: BSplineCurve PolesCount=3 KnotsCount=2 Degree=2 IsPeriodic=0
    g17: GeomPoint X=302.073 Y=124.221 Z=0
    g18: GeomPoint X=302.996 Y=121.665 Z=0
    g19: Circle CenterX=306.073 CenterY=73.3346 CenterZ=0 NormalX=0 NormalY=0 NormalZ=1 AngleXU=0 Radius=1
    g20: Circle CenterX=306.073 CenterY=77.3346 CenterZ=0 NormalX=0 NormalY=0 NormalZ=1 AngleXU=0 Radius=1
    g21: Circle CenterX=302.535 CenterY=75.4095 CenterZ=0 NormalX=0 NormalY=0 NormalZ=1 AngleXU=0 Radius=1
    g22: BSplineCurve PolesCount=3 KnotsCount=2 Degree=2 IsPeriodic=0
    g23: GeomPoint X=306.073 Y=73.3346 Z=0
    g24: GeomPoint X=302.535 Y=75.4095 Z=0
    g25: Circle CenterX=362.073 CenterY=124.221 CenterZ=0 NormalX=0 NormalY=0 NormalZ=1 AngleXU=0 Radius=1
    g26: Circle CenterX=366.073 CenterY=124.221 CenterZ=0 NormalX=0 NormalY=0 NormalZ=1 AngleXU=0 Radius=1
    g27: Circle CenterX=362.567 CenterY=122.294 CenterZ=0 NormalX=0 NormalY=0 NormalZ=1 AngleXU=0 Radius=1
    g28: BSplineCurve PolesCount=3 KnotsCount=2 Degree=2 IsPeriodic=0
    g29: GeomPoint X=362.073 Y=124.221 Z=0
    g30: GeomPoint X=362.567 Y=122.294 Z=0
    g31: Circle CenterX=322.073 CenterY=124.221 CenterZ=0 NormalX=0 NormalY=0 NormalZ=1 AngleXU=0 Radius=1
    g32: Circle CenterX=318.073 CenterY=124.221 CenterZ=0 NormalX=0 NormalY=0 NormalZ=1 AngleXU=0 Radius=1
    g33: Circle CenterX=318.073 CenterY=120.221 CenterZ=0 NormalX=0 NormalY=0 NormalZ=1 AngleXU=0 Radius=1
    g34: BSplineCurve PolesCount=3 KnotsCount=2 Degree=2 IsPeriodic=0
    g35: GeomPoint X=322.073 Y=124.221 Z=0
    g36: GeomPoint X=318.073 Y=120.221 Z=0
    g37: Circle CenterX=322.073 CenterY=105.865 CenterZ=0 NormalX=0 NormalY=0 NormalZ=1 AngleXU=0 Radius=1
    g38: Circle CenterX=318.073 CenterY=105.865 CenterZ=0 NormalX=0 NormalY=0 NormalZ=1 AngleXU=0 Radius=1
    g39: Circle CenterX=318.073 CenterY=109.865 CenterZ=0 NormalX=0 NormalY=0 NormalZ=1 AngleXU=0 Radius=1
    g40: BSplineCurve PolesCount=3 KnotsCount=2 Degree=2 IsPeriodic=0
    g41: GeomPoint X=322.073 Y=105.865 Z=0
    g42: GeomPoint X=318.073 Y=109.865 Z=0
    g43: Circle CenterX=336.157 CenterY=107.779 CenterZ=0 NormalX=0 NormalY=0 NormalZ=1 AngleXU=0 Radius=1
    g44: Circle CenterX=332.651 CenterY=105.853 CenterZ=0 NormalX=0 NormalY=0 NormalZ=1 AngleXU=0 Radius=1
    g45: Circle CenterX=328.643 CenterY=105.865 CenterZ=0 NormalX=0 NormalY=0 NormalZ=1 AngleXU=0 Radius=1
    g46: BSplineCurve PolesCount=3 KnotsCount=2 Degree=2 IsPeriodic=0
    g47: GeomPoint X=336.157 Y=107.779 Z=0
    g48: GeomPoint X=328.643 Y=105.865 Z=0
    g49: Circle CenterX=322.073 CenterY=76.4095 CenterZ=0 NormalX=0 NormalY=0 NormalZ=1 AngleXU=0 Radius=4
    g50: BSplineCurve PolesCount=3 KnotsCount=2 Degree=2 IsPeriodic=0
    g51: GeomPoint X=318.073 Y=72.4095 Z=0
    g52: GeomPoint X=322.073 Y=76.4095 Z=0
    g53: Circle CenterX=375.073 CenterY=72.4095 CenterZ=0 NormalX=0 NormalY=0 NormalZ=1 AngleXU=0 Radius=1
    g54: Circle CenterX=375.073 CenterY=76.4095 CenterZ=0 NormalX=0 NormalY=0 NormalZ=1 AngleXU=0 Radius=1
    g55: Circle CenterX=371.073 CenterY=76.4095 CenterZ=0 NormalX=0 NormalY=0 NormalZ=1 AngleXU=0 Radius=1
    g56: BSplineCurve PolesCount=3 KnotsCount=2 Degree=2 IsPeriodic=0
    g57: GeomPoint X=375.073 Y=72.4095 Z=0
    g58: GeomPoint X=371.073 Y=76.4095 Z=0
    g59: LineSegment StartX=322.073 StartY=76.4095 StartZ=0 EndX=371.073 EndY=76.4095 EndZ=0
    g60: Circle CenterX=232.072 CenterY=133.221 CenterZ=0 NormalX=0 NormalY=0 NormalZ=1 AngleXU=0 Radius=1
    g61: Circle CenterX=226.072 CenterY=136.221 CenterZ=0 NormalX=0 NormalY=0 NormalZ=1 AngleXU=0 Radius=1
    g62: Circle CenterX=226.072 CenterY=124.221 CenterZ=0 NormalX=0 NormalY=0 NormalZ=1 AngleXU=0 Radius=1
    g63: Circle CenterX=232.072 CenterY=127.221 CenterZ=0 NormalX=0 NormalY=0 NormalZ=1 AngleXU=0 Radius=1
    g64: BSplineCurve PolesCount=5 KnotsCount=3 Degree=3 IsPeriodic=0
    g65: GeomPoint X=232.072 Y=133.221 Z=0
    g66: GeomPoint X=223.072 Y=130.221 Z=0
    g67: GeomPoint X=232.072 Y=127.221 Z=0
    g68: LineSegment StartX=240.687 StartY=51.8263 StartZ=0 EndX=243.317 EndY=53.2701 EndZ=0
    g69: LineSegment StartX=243.575 StartY=46.5669 StartZ=0 EndX=246.205 EndY=48.0108 EndZ=0
    g70: ArcOfCircle CenterX=247.391 CenterY=52.0843 CenterZ=0 NormalX=0 NormalY=0 NormalZ=1 AngleXU=0 Radius=4.24264 StartAngle=4.42912 EndAngle=9.14151
    g71: LineSegment StartX=243.475 StartY=65.4951 StartZ=0 EndX=245.073 EndY=63.5726 EndZ=0
    g72: LineSegment StartX=243.575 StartY=46.5669 StartZ=0 EndX=245.072 EndY=43.8408 EndZ=0
    g73: LineSegment StartX=245.072 StartY=43.8408 StartZ=0 EndX=302.535 EndY=75.4095 EndZ=0
    g74: LineSegment StartX=239.192 StartY=54.5542 StartZ=0 EndX=302.567 EndY=89.3511 EndZ=0
    g75: LineSegment StartX=232.072 StartY=127.221 StartZ=0 EndX=232.072 EndY=124.221 EndZ=0
    g76: LineSegment StartX=232.072 StartY=136.221 StartZ=0 EndX=232.072 EndY=133.221 EndZ=0
    g77: LineSegment StartX=232.072 StartY=136.221 StartZ=0 EndX=407.073 EndY=136.221 EndZ=0
    g78: LineSegment StartX=322.073 StartY=124.221 StartZ=0 EndX=362.073 EndY=124.221 EndZ=0
    g79: LineSegment StartX=362.567 StartY=122.294 StartZ=0 EndX=336.157 EndY=107.779 EndZ=0
    g80: LineSegment StartX=322.073 StartY=105.865 StartZ=0 EndX=328.643 EndY=105.865 EndZ=0
    g81: LineSegment StartX=318.073 StartY=120.221 StartZ=0 EndX=318.073 EndY=109.865 EndZ=0
    g82: LineSegment StartX=232.072 StartY=124.221 StartZ=0 EndX=302.073 EndY=124.221 EndZ=0
    g83: LineSegment StartX=302.996 StartY=121.665 StartZ=0 EndX=240.171 EndY=69.471 EndZ=0
    g84: LineSegment StartX=240.171 StartY=69.471 StartZ=0 EndX=241.711 EndY=67.6177 EndZ=0
    g85: LineSegment StartX=241.711 StartY=67.6177 StartZ=0 EndX=246.787 EndY=71.8365 EndZ=0
    g86: LineSegment StartX=246.787 StartY=71.8365 StartZ=0 EndX=248.551 EndY=69.712 EndZ=0
    g87: LineSegment StartX=248.551 StartY=69.712 StartZ=0 EndX=243.475 EndY=65.4951 EndZ=0
    g88: LineSegment StartX=245.073 StartY=63.5726 StartZ=0 EndX=302.996 EndY=111.695 EndZ=0
    g89: LineSegment StartX=239.192 StartY=54.5542 StartZ=0 EndX=240.687 EndY=51.8263 EndZ=0
    g90: LineSegment StartX=375.073 StartY=48.2206 StartZ=0 EndX=382.073 EndY=48.2206 EndZ=0
    g91: LineSegment StartX=407.073 StartY=48.2206 StartZ=0 EndX=400.073 EndY=48.2206 EndZ=0
    g92: LineSegment StartX=394.073 StartY=48.2206 StartZ=0 EndX=394.073 EndY=52.2206 EndZ=0
    g93: LineSegment StartX=388.073 StartY=48.2206 StartZ=0 EndX=388.073 EndY=58.2206 EndZ=0
    g94: ArcOfCircle CenterX=385.073 CenterY=61.2206 CenterZ=0 NormalX=0 NormalY=0 NormalZ=1 AngleXU=0 Radius=4.24264 StartAngle=5.49779 EndAngle=10.2102
    g95: ArcOfCircle CenterX=397.073 CenterY=55.2206 CenterZ=0 NormalX=0 NormalY=0 NormalZ=1 AngleXU=0 Radius=4.24264 StartAngle=5.49779 EndAngle=10.2102
    g96: LineSegment StartX=382.073 StartY=58.2206 StartZ=0 EndX=382.073 EndY=48.2206 EndZ=0
    g97: LineSegment StartX=400.073 StartY=52.2206 StartZ=0 EndX=400.073 EndY=48.2206 EndZ=0
    g98: LineSegment StartX=394.073 StartY=48.2206 StartZ=0 EndX=388.073 EndY=48.2206 EndZ=0
    g99: LineSegment StartX=306.073 StartY=-27.5935 StartZ=0 EndX=310.073 EndY=-27.5935 EndZ=0
    g100: LineSegment StartX=318.073 StartY=-27.5935 StartZ=0 EndX=314.073 EndY=-27.5935 EndZ=0
    g101: LineSegment StartX=310.073 StartY=-27.5935 StartZ=0 EndX=310.073 EndY=-31.5935 EndZ=0
    g102: LineSegment StartX=314.073 StartY=-27.5935 StartZ=0 EndX=314.073 EndY=-31.5935 EndZ=0
    g103: ArcOfCircle CenterX=312.073 CenterY=-33.5935 CenterZ=0 NormalX=0 NormalY=0 NormalZ=1 AngleXU=0 Radius=2.82843 StartAngle=2.35619 EndAngle=7.06858
    g104: LineSegment StartX=375.073 StartY=72.4095 StartZ=0 EndX=375.073 EndY=48.2206 EndZ=0
    g105: LineSegment StartX=407.073 StartY=48.2206 StartZ=0 EndX=407.073 EndY=136.221 EndZ=0
    g106: LineSegment StartX=318.073 StartY=-27.5935 StartZ=0 EndX=318.073 EndY=72.4095 EndZ=0
    g107: LineSegment StartX=306.073 StartY=73.3346 StartZ=0 EndX=306.073 EndY=-27.5935 EndZ=0
  constraints (136):
    c: Weight(g0) = 1
    c: Equal(g0,g1)
    c: Equal(g0,g2)
    c: InternalAlignment(g0,g3)
    c: InternalAlignment(g1,g3)
    c: InternalAlignment(g2,g3)
    c: InternalAlignment(g4,g3)
    c: InternalAlignment(g5,g3)
    c: Weight(g6) = 1
    c: Equal(g6,g7)
    c: Equal(g6,g8)
    c: InternalAlignment(g6,g9)
    c: InternalAlignment(g7,g9)
    c: InternalAlignment(g8,g9)
    c: InternalAlignment(g10,g9)
    c: InternalAlignment(g11,g9)
    c: Block(g3)
    c: Block(g9)
    c: Coincident(g12,g3)
    c: Coincident(g12,g9)
    c: Vertical(g12)
    c: Weight(g13) = 1
    c: Equal(g13,g14)
    c: Equal(g13,g15)
    c: InternalAlignment(g14,g16)
    c: InternalAlignment(g15,g16)
    c: InternalAlignment(g17,g16)
    c: InternalAlignment(g18,g16)
    c: Block(g71)
    c: Block(g72)
    c: Coincident(g73,g72)
    c: Coincident(g73,g22)
    c: Block(g73)
    c: Coincident(g70,g69)
    c: Coincident(g70,g68)
    c: Coincident(g74,g9)
    c: Block(g74)
    c: Distance(g71) = 2.5
    c: Block(g64)
    c: Block(g46)
    c: Block(g59)
    c: Coincident(g75,g64)
    c: Vertical(g75)
    c: Coincident(g76,g64)
    c: Vertical(g76)
    c: Coincident(g77,g76)
    c: Horizontal(g77)
    c: Coincident(g78,g34)
    c: Coincident(g78,g28)
    c: Horizontal(g78)
    c: Coincident(g79,g28)
    c: Coincident(g79,g46)
    c: Coincident(g80,g40)
    c: Coincident(g80,g46)
    c: Horizontal(g80)
    c: Coincident(g81,g34)
    c: Coincident(g81,g40)
    c: Vertical(g81)
    c: Block(g34)
    c: Block(g40)
    c: Block(g28)
    c: Coincident(g82,g75)
    c: Coincident(g82,g16)
    c: Horizontal(g82)
    c: Coincident(g83,g16)
    c: Block(g82)
    c: Block(g83)
    c: Block(g16)
    c: Coincident(g84,g83)
    c: Block(g84)
    c: Coincident(g85,g84)
    c: Block(g85)
    c: Coincident(g86,g85)
    c: Coincident(g87,g86)
    c: Coincident(g87,g71)
    c: Block(g87)
    c: Coincident(g88,g71)
    c: Coincident(g88,g3)
    c: Block(g88)
    c: Coincident(g89,g74)
    c: Coincident(g89,g68)
    c: Block(g70)
    c: Block(g68)
    c: Block(g69)
    c: Block(g22)
    c: Block(g50)
    c: Block(g56)
    c: Horizontal(g90)
    c: Distance(g90) = 7
    c: Horizontal(g91)
    c: Distance(g91) = 7
    c: Vertical(g92)
    c: Distance(g92) = 4
    c: Vertical(g93)
    c: Distance(g93) = 10
    c: Coincident(g94,g93)
    c: Coincident(g95,g92)
    c: Block(g95)
    c: Block(g94)
    c: Coincident(g96,g94)
    c: Coincident(g96,g90)
    c: Vertical(g96)
    c: Coincident(g97,g95)
    c: Coincident(g97,g91)
    c: Vertical(g97)
    c: Coincident(g98,g92)
    c: Coincident(g98,g93)
    c: Horizontal(g98)
    c: Horizontal(g99)
    c: Distance(g99) = 4
    c: Horizontal(g100)
    c: Distance(g100) = 4
    c: Coincident(g101,g99)
    c: Vertical(g101)
    c: Coincident(g102,g100)
    c: Vertical(g102)
    c: Distance(g101) = 4
    c: Distance(g102) = 4
    c: Coincident(g103,g101)
    c: Coincident(g103,g102)
    c: Block(g103)
    c: Coincident(g104,g56)
    c: Coincident(g104,g90)
    c: Vertical(g104)
    c: Block(g104)
    c: Coincident(g105,g91)
    c: Coincident(g105,g77)
    c: Vertical(g105)
    c: Block(g77)
    c: Block(g105)
    c: Coincident(g106,g100)
    c: Coincident(g106,g50)
    c: Vertical(g106)
    c: Coincident(g107,g22)
    c: Coincident(g107,g99)
    c: Vertical(g107)
FEATURE [Sketcher::SketchObject] Sketch009  label="middleBottom"
  FullyConstrained = true
  sketch-geometry (109):
    g0: Circle CenterX=175.022 CenterY=5.37834 CenterZ=0 NormalX=0 NormalY=0 NormalZ=1 AngleXU=0 Radius=1
    g1: Circle CenterX=179.022 CenterY=7.57463 CenterZ=0 NormalX=0 NormalY=0 NormalZ=1 AngleXU=0 Radius=1
    g2: Circle CenterX=179.022 CenterY=5.34704 CenterZ=0 NormalX=0 NormalY=0 NormalZ=1 AngleXU=0 Radius=1
    g3: BSplineCurve PolesCount=3 KnotsCount=2 Degree=2 IsPeriodic=0
    g4: GeomPoint X=175.022 Y=5.37834 Z=0
    g5: GeomPoint X=179.022 Y=5.34704 Z=0
    g6: Circle CenterX=189.124 CenterY=5.37834 CenterZ=0 NormalX=0 NormalY=0 NormalZ=1 AngleXU=0 Radius=1
    g7: Circle CenterX=185.124 CenterY=7.57463 CenterZ=0 NormalX=0 NormalY=0 NormalZ=1 AngleXU=0 Radius=1
    g8: Circle CenterX=185.124 CenterY=5.34704 CenterZ=0 NormalX=0 NormalY=0 NormalZ=1 AngleXU=0 Radius=1
    g9: BSplineCurve PolesCount=3 KnotsCount=2 Degree=2 IsPeriodic=0
    g10: GeomPoint X=189.124 Y=5.37834 Z=0
    g11: GeomPoint X=185.124 Y=5.34704 Z=0
    g12: Circle CenterX=224.513 CenterY=-14.0532 CenterZ=0 NormalX=0 NormalY=0 NormalZ=1 AngleXU=0 Radius=1
    g13: Circle CenterX=236.584 CenterY=-24.2775 CenterZ=0 NormalX=0 NormalY=0 NormalZ=1 AngleXU=0 Radius=1
    g14: BSplineCurve PolesCount=3 KnotsCount=2 Degree=2 IsPeriodic=0
    g15: GeomPoint X=236.584 Y=-24.2775 Z=0
    g16: Circle CenterX=125.607 CenterY=-21.7539 CenterZ=0 NormalX=0 NormalY=0 NormalZ=1 AngleXU=0 Radius=1
    g17: Circle CenterX=139.632 CenterY=-14.0532 CenterZ=0 NormalX=0 NormalY=0 NormalZ=1 AngleXU=0 Radius=1
    g18: Circle CenterX=127.325 CenterY=-24.2775 CenterZ=0 NormalX=0 NormalY=0 NormalZ=1 AngleXU=0 Radius=1
    g19: BSplineCurve PolesCount=3 KnotsCount=2 Degree=2 IsPeriodic=0
    g20: GeomPoint X=125.607 Y=-21.7539 Z=0
    g21: GeomPoint X=127.325 Y=-24.2775 Z=0
    g22: Circle CenterX=179.022 CenterY=-85.8163 CenterZ=0 NormalX=0 NormalY=0 NormalZ=1 AngleXU=0 Radius=1
    g23: Circle CenterX=179.022 CenterY=-91.7794 CenterZ=0 NormalX=0 NormalY=0 NormalZ=1 AngleXU=0 Radius=1
    g24: Circle CenterX=171.895 CenterY=-91.8014 CenterZ=0 NormalX=0 NormalY=0 NormalZ=1 AngleXU=0 Radius=1
    g25: BSplineCurve PolesCount=3 KnotsCount=2 Degree=2 IsPeriodic=0
    g26: GeomPoint X=179.022 Y=-85.8163 Z=0
    g27: GeomPoint X=171.895 Y=-91.8014 Z=0
    g28: Circle CenterX=185.124 CenterY=-86.2028 CenterZ=0 NormalX=0 NormalY=0 NormalZ=1 AngleXU=0 Radius=1
    g29: Circle CenterX=185.124 CenterY=-91.7794 CenterZ=0 NormalX=0 NormalY=0 NormalZ=1 AngleXU=0 Radius=1
    g30: Circle CenterX=191.747 CenterY=-91.7794 CenterZ=0 NormalX=0 NormalY=0 NormalZ=1 AngleXU=0 Radius=1
    g31: BSplineCurve PolesCount=3 KnotsCount=2 Degree=2 IsPeriodic=0
    g32: GeomPoint X=185.124 Y=-86.2028 Z=0
    g33: GeomPoint X=191.747 Y=-91.7794 Z=0
    g34: BSplineCurve PolesCount=5 KnotsCount=3 Degree=3 IsPeriodic=0
    g35: LineSegment StartX=132.072 StartY=-100.779 StartZ=0 EndX=132.072 EndY=-103.779 EndZ=0
    g36: GeomPoint X=232.072 Y=-94.7794 Z=0
    g37: GeomPoint X=223.072 Y=-97.7794 Z=0
    g38: Circle CenterX=232.072 CenterY=-94.7794 CenterZ=0 NormalX=0 NormalY=0 NormalZ=1 AngleXU=0 Radius=1
    g39: Circle CenterX=232.072 CenterY=-100.779 CenterZ=0 NormalX=0 NormalY=0 NormalZ=1 AngleXU=0 Radius=1
    g40: BSplineCurve PolesCount=5 KnotsCount=3 Degree=3 IsPeriodic=0
    g41: GeomPoint X=232.072 Y=-100.779 Z=0
    g42: LineSegment StartX=123.656 StartY=-37.1092 StartZ=0 EndX=122.136 EndY=-35.2714 EndZ=0
    g43: LineSegment StartX=117.05 StartY=-39.4781 StartZ=0 EndX=115.291 EndY=-37.3514 EndZ=0
    g44: LineSegment StartX=120.377 StartY=-33.1447 StartZ=0 EndX=118.86 EndY=-31.3104 EndZ=0
    g45: ArcOfCircle CenterX=116.562 CenterY=-19.6236 CenterZ=0 NormalX=0 NormalY=0 NormalZ=1 AngleXU=0 Radius=4.24264 StartAngle=1.28753 EndAngle=5.99992
    g46: LineSegment StartX=240.266 StartY=-37.1092 StartZ=0 EndX=189.124 EndY=5.37834 EndZ=0
    g47: LineSegment StartX=191.747 StartY=-91.7794 StartZ=0 EndX=232.072 EndY=-91.7794 EndZ=0
    g48: LineSegment StartX=232.072 StartY=-91.7794 StartZ=0 EndX=232.072 EndY=-94.7794 EndZ=0
    g49: LineSegment StartX=232.072 StartY=-100.779 StartZ=0 EndX=232.072 EndY=-103.779 EndZ=0
    g50: LineSegment StartX=132.072 StartY=-103.779 StartZ=0 EndX=232.072 EndY=-103.779 EndZ=0
    g51: LineSegment StartX=132.072 StartY=-91.8014 StartZ=0 EndX=132.072 EndY=-94.7791 EndZ=0
    g52: LineSegment StartX=132.072 StartY=-91.8014 StartZ=0 EndX=171.895 EndY=-91.8014 EndZ=0
    g53: LineSegment StartX=179.022 StartY=-85.8163 StartZ=0 EndX=179.022 EndY=5.34704 EndZ=0
    g54: LineSegment StartX=175.022 StartY=5.37834 StartZ=0 EndX=123.656 EndY=-37.1092 EndZ=0
    g55: LineSegment StartX=185.124 StartY=5.34704 StartZ=0 EndX=185.124 EndY=-86.2028 EndZ=0
    g56: LineSegment StartX=122.136 StartY=-35.2714 StartZ=0 EndX=117.05 EndY=-39.4781 EndZ=0
    g57: LineSegment StartX=115.291 StartY=-37.3514 StartZ=0 EndX=120.377 EndY=-33.1447 EndZ=0
    g58: LineSegment StartX=118.86 StartY=-31.3104 StartZ=0 EndX=127.325 EndY=-24.2775 EndZ=0
    g59: LineSegment StartX=125.607 StartY=-21.7539 StartZ=0 EndX=124.815 EndY=-22.1887 EndZ=0
    g60: LineSegment StartX=123.265 StartY=-19.3655 StartZ=0 EndX=124.815 EndY=-22.1887 EndZ=0
    g61: LineSegment StartX=120.636 StartY=-20.8094 StartZ=0 EndX=123.265 EndY=-19.3655 EndZ=0
    g62: LineSegment StartX=117.748 StartY=-15.55 StartZ=0 EndX=120.377 EndY=-14.1062 EndZ=0
    g63: LineSegment StartX=120.377 StartY=-14.1062 StartZ=0 EndX=118.934 EndY=-11.4765 EndZ=0
    g64: LineSegment StartX=236.584 StartY=-24.2775 StartZ=0 EndX=245.072 EndY=-31.3037 EndZ=0
    g65: LineSegment StartX=245.072 StartY=-31.3037 StartZ=0 EndX=243.535 EndY=-33.1602 EndZ=0
    g66: LineSegment StartX=243.535 StartY=-33.1602 StartZ=0 EndX=248.619 EndY=-37.3688 EndZ=0
    g67: LineSegment StartX=248.619 StartY=-37.3688 StartZ=0 EndX=246.855 EndY=-39.5064 EndZ=0
    g68: LineSegment StartX=246.855 StartY=-39.5064 StartZ=0 EndX=241.778 EndY=-35.2889 EndZ=0
    g69: LineSegment StartX=241.778 StartY=-35.2889 StartZ=0 EndX=240.266 EndY=-37.1092 EndZ=0
    g70: LineSegment StartX=243.628 StartY=-14.0323 StartZ=0 EndX=246.258 EndY=-15.476 EndZ=0
    g71: LineSegment StartX=240.741 StartY=-19.2917 StartZ=0 EndX=243.37 EndY=-20.7355 EndZ=0
    g72: ArcOfCircle CenterX=247.444 CenterY=-19.5496 CenterZ=0 NormalX=0 NormalY=0 NormalZ=1 AngleXU=0 Radius=4.24264 StartAngle=3.4249 EndAngle=8.13729
    g73: LineSegment StartX=240.741 StartY=-19.2917 StartZ=0 EndX=239.201 EndY=-22.0968 EndZ=0
    g74: LineSegment StartX=238.538 StartY=-21.7516 StartZ=0 EndX=239.201 EndY=-22.0968 EndZ=0
    g75: LineSegment StartX=245.072 StartY=-11.4025 StartZ=0 EndX=243.628 EndY=-14.0323 EndZ=0
    g76-g91: Circle x16 (B-spline internal-alignment scaffolding for g92; pole/knot coordinates omitted)
    g92: BSplineCurve PolesCount=16 KnotsCount=14 Degree=3 IsPeriodic=0
    g93-g106: GeomPoint x14 (B-spline internal-alignment scaffolding for g92; pole/knot coordinates omitted)
    g107: LineSegment StartX=165.871 StartY=14.2956 StartZ=0 EndX=118.934 EndY=-11.4765 EndZ=0
    g108: LineSegment StartX=198.264 StartY=14.2963 StartZ=0 EndX=245.072 EndY=-11.4025 EndZ=0
  constraints (146):
    c: Weight(g0) = 1
    c: Equal(g0,g1)
    c: Equal(g0,g2)
    c: InternalAlignment(g0,g3)
    c: InternalAlignment(g1,g3)
    c: InternalAlignment(g2,g3)
    c: InternalAlignment(g4,g3)
    c: InternalAlignment(g5,g3)
    c: Weight(g6) = 1
    c: Equal(g6,g7)
    c: Equal(g6,g8)
    c: InternalAlignment(g6,g9)
    c: InternalAlignment(g7,g9)
    c: InternalAlignment(g8,g9)
    c: InternalAlignment(g10,g9)
    c: InternalAlignment(g11,g9)
    c: Block(g9)
    c: Block(g3)
    c: InternalAlignment(g12,g14)
    c: InternalAlignment(g13,g14)
    c: InternalAlignment(g15,g14)
    c: Block(g14)
    c: Weight(g16) = 1
    c: Equal(g16,g17)
    c: Equal(g16,g18)
    c: InternalAlignment(g16,g19)
    c: InternalAlignment(g17,g19)
    c: InternalAlignment(g18,g19)
    c: InternalAlignment(g20,g19)
    c: InternalAlignment(g21,g19)
    c: Block(g19)
    c: Weight(g22) = 1
    c: Equal(g22,g23)
    c: Equal(g22,g24)
    c: InternalAlignment(g22,g25)
    c: InternalAlignment(g23,g25)
    c: InternalAlignment(g24,g25)
    c: InternalAlignment(g26,g25)
    c: InternalAlignment(g27,g25)
    c: Weight(g28) = 1
    c: Equal(g28,g29)
    c: Equal(g28,g30)
    c: InternalAlignment(g28,g31)
    c: InternalAlignment(g29,g31)
    c: InternalAlignment(g30,g31)
    c: InternalAlignment(g32,g31)
    c: InternalAlignment(g33,g31)
    c: Block(g31)
    c: Block(g25)
    c: Block(g34)
    c: Coincident(g35,g34)
    c: Vertical(g35)
    c: Block(g35)
    c: Equal(g38,g39)
    c: InternalAlignment(g38,g40)
    c: InternalAlignment(g39,g40)
    c: InternalAlignment(g36,g40)
    c: InternalAlignment(g37,g40)
    c: InternalAlignment(g41,g40)
    c: Block(g40)
    c: Distance(g42) = 2.385
    c: Distance(g43) = 2.76
    c: Parallel(g42,g44)
    c: Block(g45)
    c: Coincident(g46,g9)
    c: Coincident(g47,g31)
    c: Horizontal(g47)
    c: Block(g47)
    c: Coincident(g48,g47)
    c: Coincident(g48,g40)
    c: Vertical(g48)
    c: Block(g48)
    c: Coincident(g49,g40)
    c: Vertical(g49)
    c: Block(g49)
    c: Coincident(g50,g35)
    c: Coincident(g50,g49)
    c: Horizontal(g50)
    c: Block(g50)
    c: Coincident(g51,g34)
    c: Vertical(g51)
    c: Coincident(g52,g51)
    c: Coincident(g52,g25)
    c: Horizontal(g52)
    c: Coincident(g53,g25)
    c: Coincident(g53,g3)
    c: Vertical(g53)
    c: Coincident(g54,g3)
    c: Coincident(g54,g42)
    c: Coincident(g55,g9)
    c: Coincident(g55,g31)
    c: Vertical(g55)
    c: Block(g42)
    c: Coincident(g56,g42)
    c: Coincident(g56,g43)
    c: Coincident(g57,g43)
    c: Coincident(g57,g44)
    c: Block(g57)
    c: Block(g56)
    c: Coincident(g58,g44)
    c: Coincident(g58,g19)
    c: Block(g58)
    c: Coincident(g59,g19)
    c: Block(g59)
    c: Coincident(g60,g59)
    c: Block(g60)
    c: Coincident(g61,g45)
    c: Coincident(g61,g60)
    c: Coincident(g62,g45)
    c: Coincident(g63,g62)
    c: Block(g63)
    c: Coincident(g64,g14)
    c: Block(g64)
    c: Coincident(g65,g64)
    c: Coincident(g66,g65)
    c: Coincident(g67,g66)
    c: Coincident(g68,g67)
    c: Coincident(g69,g68)
    c: Coincident(g69,g46)
    c: Block(g46)
    c: Block(g68)
    c: Block(g66)
    c: Distance(g70) = 3
    c: Distance(g71) = 3
    c: Coincident(g72,g70)
    c: Coincident(g72,g71)
    c: Block(g72)
    c: Coincident(g73,g71)
    c: Distance(g73) = 3.2
    c: Coincident(g74,g14)
    c: Coincident(g74,g73)
    c: Coincident(g75,g70)
    c: Block(g75)
    c: Block(g73)
    c: Distance(g63) = 3
    c: Distance(g60) = 3.22077
    c: Weight(g76) = 1
    c: Equal(g76, g77-g91) x15
    c: InternalAlignment(g76-g91 -> g92) x16
    c: InternalAlignment(g93-g106 -> g92) x14
    c: Coincident(g107,g92)
    c: Coincident(g107,g63)
    c: Block(g107)
    c: Block(g92)
    c: Coincident(g108,g92)
    c: Coincident(g108,g75)
FEATURE [Sketcher::SketchObject] Sketch010  label="legBottom"
  FullyConstrained = true
  MapMode = 4
  Placement = pos=(0,0,0) rot=(0.57735,0.57735,0.57735;2.0944rad)
  sketch-geometry (38):
    g0: BSplineCurve PolesCount=3 KnotsCount=2 Degree=2 IsPeriodic=0
    g1: Circle CenterX=-199.665 CenterY=-138.314 CenterZ=0 NormalX=0 NormalY=0 NormalZ=1 AngleXU=0 Radius=1
    g2: GeomPoint X=-199.665 Y=-138.314 Z=0
    g3: LineSegment StartX=-199.665 StartY=-138.314 StartZ=0 EndX=-200.721 EndY=-141.122 EndZ=0
    g4: Circle CenterX=-17.0256 CenterY=-190.268 CenterZ=0 NormalX=0 NormalY=0 NormalZ=1 AngleXU=0 Radius=10.5072
    g5: Circle CenterX=-37.7758 CenterY=-187.672 CenterZ=0 NormalX=0 NormalY=0 NormalZ=1 AngleXU=0 Radius=5.64388
    g6: Circle CenterX=-51.4606 CenterY=-185.091 CenterZ=0 NormalX=0 NormalY=0 NormalZ=1 AngleXU=0 Radius=3.01653
    g7: Circle CenterX=-60.4835 CenterY=-182.688 CenterZ=0 NormalX=0 NormalY=0 NormalZ=1 AngleXU=0 Radius=2.12826
    g8: Circle CenterX=-3.29005 CenterY=-177.662 CenterZ=0 NormalX=0 NormalY=0 NormalZ=1 AngleXU=0 Radius=3.26661
    g9: ArcOfCircle CenterX=11.0205 CenterY=-198.019 CenterZ=0 NormalX=0 NormalY=0 NormalZ=1 AngleXU=0 Radius=13 StartAngle=2.78068 EndAngle=5.92131
    g10: LineSegment StartX=5.08312 StartY=-176.581 StartZ=0 EndX=-1.14188 EndY=-193.429 EndZ=0
    g11: ArcOfCircle CenterX=17.2475 CenterY=-181.166 CenterZ=0 NormalX=0 NormalY=0 NormalZ=1 AngleXU=0 Radius=13 StartAngle=1.21042 EndAngle=2.78109
    g12: LineSegment StartX=38.8952 StartY=-231.233 StartZ=0 EndX=-200.721 EndY=-141.122 EndZ=0
    g13: LineSegment StartX=38.8952 StartY=-231.233 StartZ=0 EndX=39.9512 EndY=-228.425 EndZ=0
    g14: ArcOfCircle CenterX=46.9911 CenterY=-209.705 CenterZ=0 NormalX=0 NormalY=0 NormalZ=1 AngleXU=0 Radius=20 StartAngle=2.78766 EndAngle=4.35269
    g15: LineSegment StartX=23.7323 StartY=-126.969 StartZ=0 EndX=17.4091 EndY=-143.817 EndZ=0
    g16: ArcOfCircle CenterX=29.5716 CenterY=-148.408 CenterZ=0 NormalX=0 NormalY=0 NormalZ=1 AngleXU=0 Radius=13 StartAngle=2.78068 EndAngle=4.35262
    g17: ArcOfCircle CenterX=35.8967 CenterY=-131.555 CenterZ=0 NormalX=0 NormalY=0 NormalZ=1 AngleXU=0 Radius=13 StartAngle=1.21584 EndAngle=2.78109
    g18: ArcOfCircle CenterX=48.1805 CenterY=-98.7782 CenterZ=0 NormalX=0 NormalY=0 NormalZ=1 AngleXU=0 Radius=13 StartAngle=2.78068 EndAngle=4.35005
    g19: LineSegment StartX=42.354 StartY=-77.3391 StartZ=0 EndX=36.018 EndY=-94.1875 EndZ=0
    g20: ArcOfCircle CenterX=54.5183 CenterY=-81.9247 CenterZ=0 NormalX=0 NormalY=0 NormalZ=1 AngleXU=0 Radius=13 StartAngle=2.42113 EndAngle=2.78109
    g21: ArcOfCircle CenterX=20.184 CenterY=-217.506 CenterZ=0 NormalX=0 NormalY=0 NormalZ=1 AngleXU=0 Radius=3.81084 StartAngle=1.88136 EndAngle=6.80465
    g22: LineSegment StartX=38.4753 StartY=-115.966 StartZ=0 EndX=41.2852 EndY=-117.017 EndZ=0
    g23: ArcOfCircle CenterX=36.3663 CenterY=-113.042 CenterZ=0 NormalX=0 NormalY=0 NormalZ=1 AngleXU=0 Radius=3.60555 StartAngle=0.230024 EndAngle=5.3372
    g24: LineSegment StartX=39.8769 StartY=-112.22 StartZ=0 EndX=42.6867 EndY=-113.271 EndZ=0
    g25: LineSegment StartX=19.9036 StartY=-165.61 StartZ=0 EndX=22.7134 EndY=-166.661 EndZ=0
    g26: ArcOfCircle CenterX=17.7945 CenterY=-162.686 CenterZ=0 NormalX=0 NormalY=0 NormalZ=1 AngleXU=0 Radius=3.60555 StartAngle=0.230024 EndAngle=5.3372
    g27: LineSegment StartX=21.3051 StartY=-161.864 StartZ=0 EndX=24.1149 EndY=-162.915 EndZ=0
    g28: LineSegment StartX=41.085 StartY=-66.3176 StartZ=0 EndX=46.0385 EndY=-62.5254 EndZ=0
    g29: LineSegment StartX=48.9563 StartY=-66.3367 StartZ=0 EndX=44.7488 EndY=-73.3482 EndZ=0
    g30: ArcOfCircle CenterX=49.8795 CenterY=-62.6074 CenterZ=0 NormalX=0 NormalY=0 NormalZ=1 AngleXU=0 Radius=3.84187 StartAngle=4.46973 EndAngle=9.40343
    g31: LineSegment StartX=41.085 StartY=-66.3176 StartZ=0 EndX=8.65492 EndY=-152.553 EndZ=0
    g32: LineSegment StartX=43.5724 StartY=-110.934 StartZ=0 EndX=42.6867 EndY=-113.271 EndZ=0
    g33: LineSegment StartX=40.4148 StartY=-119.365 StartZ=0 EndX=41.2852 EndY=-117.017 EndZ=0
    g34: LineSegment StartX=21.8316 StartY=-169.001 StartZ=0 EndX=22.7134 EndY=-166.661 EndZ=0
    g35: LineSegment StartX=24.9948 StartY=-160.575 StartZ=0 EndX=24.1149 EndY=-162.915 EndZ=0
    g36: LineSegment StartX=23.1786 StartY=-202.622 StartZ=0 EndX=19.0195 EndY=-213.878 EndZ=0
    g37: LineSegment StartX=28.2308 StartY=-202.773 StartZ=0 EndX=23.4884 EndY=-215.608 EndZ=0
  constraints (65):
    c: Block(g9)
    c: Block(g11)
    c: InternalAlignment(g1,g0)
    c: InternalAlignment(g2,g0)
    c: Block(g0)
    c: Block(g4)
    c: Block(g8)
    c: Block(g5)
    c: Block(g6)
    c: Block(g7)
    c: Block(g14)
    c: Coincident(g13,g12)
    c: Coincident(g13,g14)
    c: Block(g13)
    c: Coincident(g3,g0)
    c: Coincident(g3,g12)
    c: Block(g12)
    c: Coincident(g10,g11)
    c: Coincident(g10,g9)
    c: Block(g16)
    c: Block(g17)
    c: Coincident(g15,g17)
    c: Coincident(g15,g16)
    c: Block(g18)
    c: Block(g20)
    c: Coincident(g19,g20)
    c: Coincident(g19,g18)
    c: Block(g21)
    c: Block(g23)
    c: Coincident(g24,g23)
    c: Coincident(g22,g23)
    c: Parallel(g24,g22)
    c: Block(g22)
    c: Block(g24)
    c: Block(g26)
    c: Coincident(g27,g26)
    c: Coincident(g25,g26)
    c: Parallel(g27,g25)
    c: Block(g25)
    c: Block(g27)
    c: Block(g28)
    c: Coincident(g30,g28)
    c: Coincident(g30,g29)
    c: Block(g30)
    c: Coincident(g31,g28)
    c: Coincident(g31,g0)
    c: Block(g29)
    c: Coincident(g32,g24)
    c: Block(g32)
    c: Coincident(g33,g22)
    c: Block(g33)
    c: Coincident(g34,g25)
    c: Coincident(g35,g27)
    c: Block(g35)
    c: Block(g34)
    c: Coincident(g36,g9)
    c: Coincident(g36,g21)
    c: Block(g36)
    c: Coincident(g11,g34)
    c: Coincident(g16,g35)
    c: Coincident(g17,g33)
    c: Coincident(g18,g32)
    c: Coincident(g20,g29)
    c: Coincident(g37,g14)
    c: Coincident(g37,g21)
